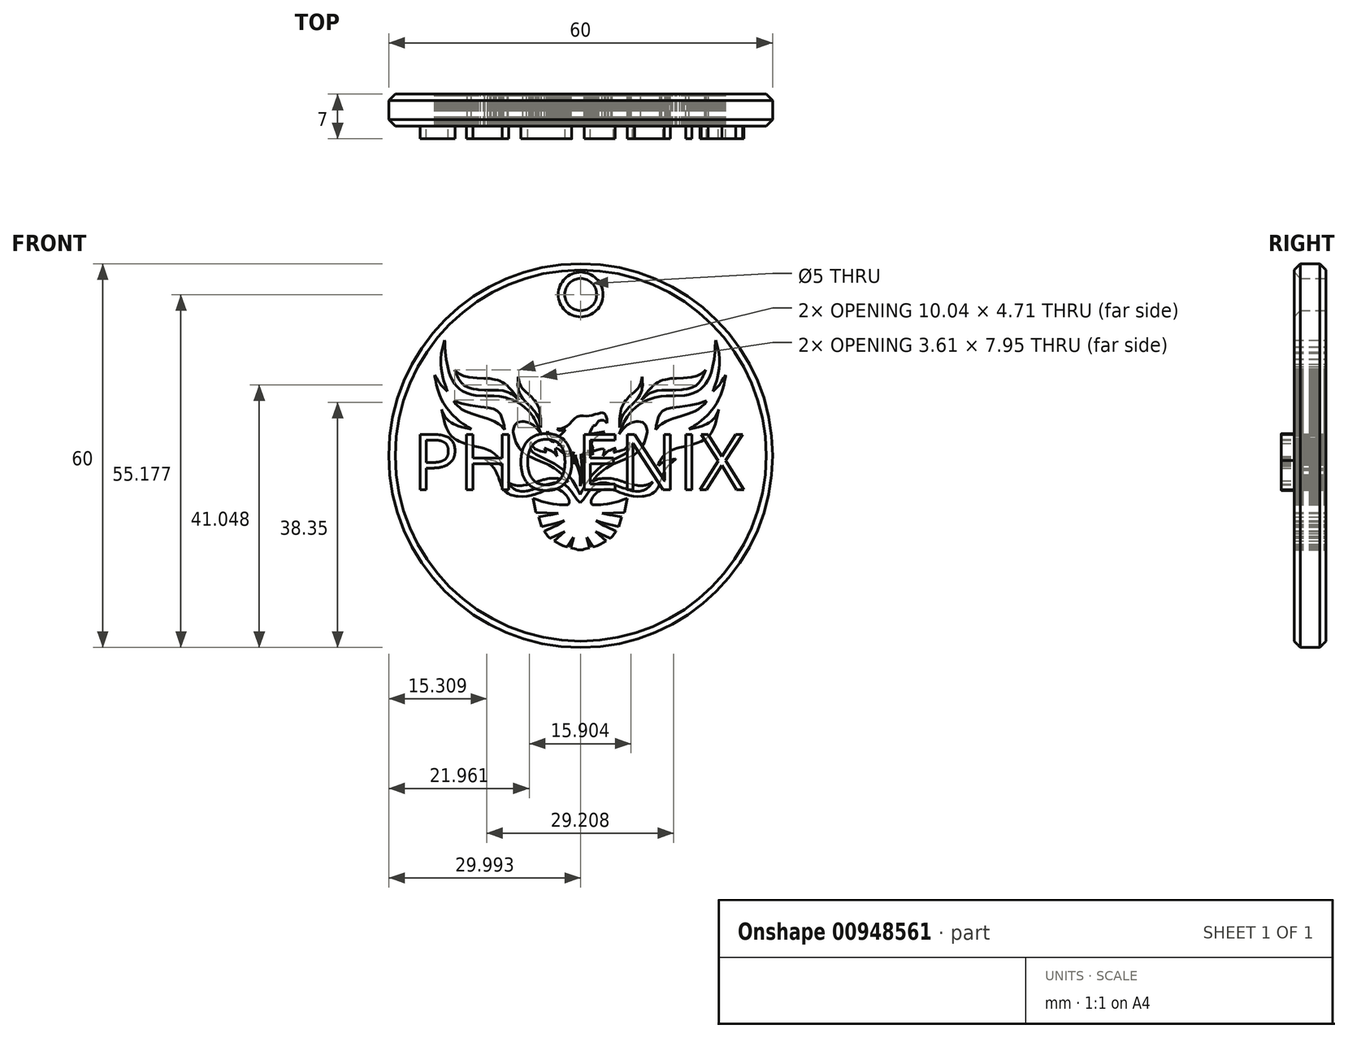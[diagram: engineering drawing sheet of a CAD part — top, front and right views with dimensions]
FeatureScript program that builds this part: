
annotation { "Feature Type Name" : "Feature", "Feature Type Description" : "" }
export const myFeature = defineFeature(function(context is Context, id is Id, definition is map)
    precondition{}
    {
        {
            var Q0;
            Q0=qCreatedBy(makeId("Front.planeOp"),FACE);
            var sketch = newSketch(context, id + "F0", { "sketchPlane" : qUnion([Q0])});
            skLineSegment(sketch, "E0", {"start": v(-23.96, 18.06) * mm, "end": v(23.17, -19.05) * mm});
            skLineSegment(sketch, "E1", {"start": v(-23.96, -19.05) * mm, "end": v(23.17, 18.06) * mm});
            skCircle(sketch, "E2", {"center": v(-0.4, -0.5) * mm, "radius": 30 * mm});
            skSolve(sketch);
        }
        {
            var Q0;
            Q0=makeQuery(id+"F0.imprint","IMPRINT",FACE,{"disambiguationData":[TD([[makeQuery(id+"F0.imprint","IMPRINT",EDGE,{"derivedFrom":sQuery(id+"F0.wireOp",EDGE,"E2")}),1.0]])]});
            extrude(context, id + "F1", {"entities" : qUnion([Q0]), "depth" : 5 * mm, "offsetDistance" : 25 * mm});
        }
        {
            var Q0;
            Q0=qCreatedBy(makeId("Front.planeOp"),FACE);
            var sketch = newSketch(context, id + "F2", { "sketchPlane" : qUnion([Q0])});
            skLineSegment(sketch, "E3", {"start": v(-6.6, 2.87) * mm, "end": v(-6.9, 3.33) * mm});
            skLineSegment(sketch, "E4", {"start": v(-6.9, 3.33) * mm, "end": v(-7.28, 3.78) * mm});
            skLineSegment(sketch, "E5", {"start": v(-7.28, 3.78) * mm, "end": v(-7.8, 4.25) * mm});
            skLineSegment(sketch, "E6", {"start": v(-7.8, 4.25) * mm, "end": v(-8.47, 4.62) * mm});
            skLineSegment(sketch, "E7", {"start": v(-8.47, 4.62) * mm, "end": v(-9.25, 4.84) * mm});
            skLineSegment(sketch, "E8", {"start": v(-9.25, 4.84) * mm, "end": v(-9.57, 4.84) * mm});
            skLineSegment(sketch, "E9", {"start": v(-9.57, 4.84) * mm, "end": v(-10.26, 4.7) * mm});
            skLineSegment(sketch, "E10", {"start": v(-10.26, 4.7) * mm, "end": v(-10.5, 4.48) * mm});
            skLineSegment(sketch, "E11", {"start": v(-10.5, 4.48) * mm, "end": v(-10.7, 4.24) * mm});
            skLineSegment(sketch, "E12", {"start": v(-10.7, 4.24) * mm, "end": v(-10.83, 3.89) * mm});
            skLineSegment(sketch, "E13", {"start": v(-10.83, 3.89) * mm, "end": v(-10.92, 3.46) * mm});
            skLineSegment(sketch, "E14", {"start": v(-10.92, 3.46) * mm, "end": v(-10.92, 3.18) * mm});
            skLineSegment(sketch, "E15", {"start": v(-10.92, 3.18) * mm, "end": v(-10.85, 2.63) * mm});
            skLineSegment(sketch, "E16", {"start": v(-10.85, 2.63) * mm, "end": v(-10.7, 2.18) * mm});
            skLineSegment(sketch, "E17", {"start": v(-10.7, 2.18) * mm, "end": v(-10.48, 1.53) * mm});
            skLineSegment(sketch, "E18", {"start": v(-10.48, 1.53) * mm, "end": v(-10.2, 1.03) * mm});
            skLineSegment(sketch, "E19", {"start": v(-10.2, 1.03) * mm, "end": v(-9.91, 0.57) * mm});
            skLineSegment(sketch, "E20", {"start": v(-9.91, 0.57) * mm, "end": v(-9.44, 0.05) * mm});
            skLineSegment(sketch, "E21", {"start": v(-9.44, 0.05) * mm, "end": v(-8.86, -0.41) * mm});
            skLineSegment(sketch, "E22", {"start": v(-8.86, -0.41) * mm, "end": v(-8.11, -0.78) * mm});
            skLineSegment(sketch, "E23", {"start": v(-8.11, -0.78) * mm, "end": v(-7.45, -1.05) * mm});
            skLineSegment(sketch, "E24", {"start": v(-7.45, -1.05) * mm, "end": v(-6.72, -1.37) * mm});
            skLineSegment(sketch, "E25", {"start": v(-6.72, -1.37) * mm, "end": v(-6.27, -1.55) * mm});
            skLineSegment(sketch, "E26", {"start": v(-6.27, -1.55) * mm, "end": v(-5.77, -1.8) * mm});
            skLineSegment(sketch, "E27", {"start": v(-5.77, -1.8) * mm, "end": v(-5.4, -1.98) * mm});
            skLineSegment(sketch, "E28", {"start": v(-5.4, -1.98) * mm, "end": v(-5, -2.2) * mm});
            skLineSegment(sketch, "E29", {"start": v(-5, -2.2) * mm, "end": v(-4.54, -2.46) * mm});
            skLineSegment(sketch, "E30", {"start": v(-4.54, -2.46) * mm, "end": v(-4.14, -2.74) * mm});
            skLineSegment(sketch, "E31", {"start": v(-4.14, -2.74) * mm, "end": v(-3.7, -3.09) * mm});
            skLineSegment(sketch, "E32", {"start": v(-3.7, -3.09) * mm, "end": v(-3.4, -3.34) * mm});
            skLineSegment(sketch, "E33", {"start": v(-3.4, -3.34) * mm, "end": v(-3.26, -3.48) * mm});
            skLineSegment(sketch, "E34", {"start": v(-3.26, -3.48) * mm, "end": v(-3.1, -3.64) * mm});
            skLineSegment(sketch, "E35", {"start": v(-3.1, -3.64) * mm, "end": v(-2.93, -3.84) * mm});
            skLineSegment(sketch, "E36", {"start": v(-2.93, -3.84) * mm, "end": v(-2.8, -4) * mm});
            skLineSegment(sketch, "E37", {"start": v(-2.8, -4) * mm, "end": v(-2.68, -4.14) * mm});
            skLineSegment(sketch, "E38", {"start": v(-2.68, -4.14) * mm, "end": v(-2.57, -4.28) * mm});
            skLineSegment(sketch, "E39", {"start": v(-2.57, -4.28) * mm, "end": v(-2.48, -4.4) * mm});
            skLineSegment(sketch, "E40", {"start": v(-2.48, -4.4) * mm, "end": v(-2.4, -4.52) * mm});
            skLineSegment(sketch, "E41", {"start": v(-2.4, -4.52) * mm, "end": v(-2.36, -4.59) * mm});
            skLineSegment(sketch, "E42", {"start": v(-2.36, -4.59) * mm, "end": v(-2.44, -4.54) * mm});
            skLineSegment(sketch, "E43", {"start": v(-2.44, -4.54) * mm, "end": v(-2.53, -4.48) * mm});
            skLineSegment(sketch, "E44", {"start": v(-2.53, -4.48) * mm, "end": v(-2.63, -4.44) * mm});
            skLineSegment(sketch, "E45", {"start": v(-2.63, -4.44) * mm, "end": v(-2.7, -4.4) * mm});
            skLineSegment(sketch, "E46", {"start": v(-2.7, -4.4) * mm, "end": v(-2.78, -4.37) * mm});
            skLineSegment(sketch, "E47", {"start": v(-2.78, -4.37) * mm, "end": v(-2.87, -4.33) * mm});
            skLineSegment(sketch, "E48", {"start": v(-2.87, -4.33) * mm, "end": v(-2.98, -4.28) * mm});
            skLineSegment(sketch, "E49", {"start": v(-2.98, -4.28) * mm, "end": v(-3.08, -4.25) * mm});
            skLineSegment(sketch, "E50", {"start": v(-3.08, -4.25) * mm, "end": v(-3.22, -4.2) * mm});
            skLineSegment(sketch, "E51", {"start": v(-3.22, -4.2) * mm, "end": v(-3.4, -4.15) * mm});
            skLineSegment(sketch, "E52", {"start": v(-3.4, -4.15) * mm, "end": v(-3.5, -4.13) * mm});
            skLineSegment(sketch, "E53", {"start": v(-3.5, -4.13) * mm, "end": v(-3.74, -4.1) * mm});
            skLineSegment(sketch, "E54", {"start": v(-3.74, -4.1) * mm, "end": v(-3.97, -4.06) * mm});
            skLineSegment(sketch, "E55", {"start": v(-3.97, -4.06) * mm, "end": v(-4.12, -4.04) * mm});
            skLineSegment(sketch, "E56", {"start": v(-4.12, -4.04) * mm, "end": v(-4.25, -4.03) * mm});
            skLineSegment(sketch, "E57", {"start": v(-4.25, -4.03) * mm, "end": v(-4.4, -4.03) * mm});
            skLineSegment(sketch, "E58", {"start": v(-4.4, -4.03) * mm, "end": v(-4.63, -4.04) * mm});
            skLineSegment(sketch, "E59", {"start": v(-4.63, -4.04) * mm, "end": v(-4.9, -4.06) * mm});
            skLineSegment(sketch, "E60", {"start": v(-4.9, -4.06) * mm, "end": v(-5.29, -4.08) * mm});
            skLineSegment(sketch, "E61", {"start": v(-5.29, -4.08) * mm, "end": v(-5.62, -4.13) * mm});
            skLineSegment(sketch, "E62", {"start": v(-5.62, -4.13) * mm, "end": v(-5.82, -4.18) * mm});
            skLineSegment(sketch, "E63", {"start": v(-5.82, -4.18) * mm, "end": v(-6.06, -4.23) * mm});
            skLineSegment(sketch, "E64", {"start": v(-6.06, -4.23) * mm, "end": v(-6.28, -4.28) * mm});
            skLineSegment(sketch, "E65", {"start": v(-6.28, -4.28) * mm, "end": v(-6.55, -4.37) * mm});
            skLineSegment(sketch, "E66", {"start": v(-6.55, -4.37) * mm, "end": v(-6.77, -4.42) * mm});
            skLineSegment(sketch, "E67", {"start": v(-6.77, -4.42) * mm, "end": v(-6.9, -4.47) * mm});
            skLineSegment(sketch, "E68", {"start": v(-6.9, -4.47) * mm, "end": v(-7.04, -4.5) * mm});
            skLineSegment(sketch, "E69", {"start": v(-7.04, -4.5) * mm, "end": v(-7.17, -4.55) * mm});
            skLineSegment(sketch, "E70", {"start": v(-7.17, -4.55) * mm, "end": v(-7.31, -4.6) * mm});
            skLineSegment(sketch, "E71", {"start": v(-7.31, -4.6) * mm, "end": v(-7.46, -4.66) * mm});
            skLineSegment(sketch, "E72", {"start": v(-7.46, -4.66) * mm, "end": v(-7.65, -4.71) * mm});
            skLineSegment(sketch, "E73", {"start": v(-7.65, -4.71) * mm, "end": v(-7.77, -4.75) * mm});
            skLineSegment(sketch, "E74", {"start": v(-7.77, -4.75) * mm, "end": v(-7.9, -4.79) * mm});
            skLineSegment(sketch, "E75", {"start": v(-7.9, -4.79) * mm, "end": v(-8.04, -4.84) * mm});
            skLineSegment(sketch, "E76", {"start": v(-8.04, -4.84) * mm, "end": v(-8.21, -4.89) * mm});
            skLineSegment(sketch, "E77", {"start": v(-8.21, -4.89) * mm, "end": v(-8.48, -4.97) * mm});
            skLineSegment(sketch, "E78", {"start": v(-8.48, -4.97) * mm, "end": v(-8.79, -5.05) * mm});
            skLineSegment(sketch, "E79", {"start": v(-8.79, -5.05) * mm, "end": v(-9.02, -5.1) * mm});
            skLineSegment(sketch, "E80", {"start": v(-9.02, -5.1) * mm, "end": v(-9.36, -5.15) * mm});
            skLineSegment(sketch, "E81", {"start": v(-9.36, -5.15) * mm, "end": v(-9.6, -5.18) * mm});
            skLineSegment(sketch, "E82", {"start": v(-9.6, -5.18) * mm, "end": v(-9.94, -5.2) * mm});
            skLineSegment(sketch, "E83", {"start": v(-9.94, -5.2) * mm, "end": v(-10.1, -5.2) * mm});
            skLineSegment(sketch, "E84", {"start": v(-10.1, -5.2) * mm, "end": v(-10.34, -5.19) * mm});
            skLineSegment(sketch, "E85", {"start": v(-10.34, -5.19) * mm, "end": v(-10.54, -5.17) * mm});
            skLineSegment(sketch, "E86", {"start": v(-10.54, -5.17) * mm, "end": v(-10.7, -5.13) * mm});
            skLineSegment(sketch, "E87", {"start": v(-10.7, -5.13) * mm, "end": v(-10.82, -5.1) * mm});
            skLineSegment(sketch, "E88", {"start": v(-10.82, -5.1) * mm, "end": v(-10.92, -5.07) * mm});
            skLineSegment(sketch, "E89", {"start": v(-10.92, -5.07) * mm, "end": v(-11.01, -5.03) * mm});
            skLineSegment(sketch, "E90", {"start": v(-11.01, -5.03) * mm, "end": v(-11.1, -5) * mm});
            skLineSegment(sketch, "E91", {"start": v(-11.1, -5) * mm, "end": v(-11.19, -4.97) * mm});
            skLineSegment(sketch, "E92", {"start": v(-11.19, -4.97) * mm, "end": v(-11.28, -4.93) * mm});
            skLineSegment(sketch, "E93", {"start": v(-11.28, -4.93) * mm, "end": v(-11.33, -4.9) * mm});
            skLineSegment(sketch, "E94", {"start": v(-11.33, -4.9) * mm, "end": v(-11.39, -4.87) * mm});
            skLineSegment(sketch, "E95", {"start": v(-11.39, -4.87) * mm, "end": v(-11.45, -4.84) * mm});
            skLineSegment(sketch, "E96", {"start": v(-11.45, -4.84) * mm, "end": v(-11.52, -4.8) * mm});
            skLineSegment(sketch, "E97", {"start": v(-11.52, -4.8) * mm, "end": v(-11.57, -4.77) * mm});
            skLineSegment(sketch, "E98", {"start": v(-11.57, -4.77) * mm, "end": v(-11.68, -4.7) * mm});
            skLineSegment(sketch, "E99", {"start": v(-11.68, -4.7) * mm, "end": v(-11.82, -4.63) * mm});
            skLineSegment(sketch, "E100", {"start": v(-11.82, -4.63) * mm, "end": v(-11.8, -4.69) * mm});
            skLineSegment(sketch, "E101", {"start": v(-11.8, -4.69) * mm, "end": v(-11.75, -4.75) * mm});
            skLineSegment(sketch, "E102", {"start": v(-11.75, -4.75) * mm, "end": v(-11.72, -4.8) * mm});
            skLineSegment(sketch, "E103", {"start": v(-11.72, -4.8) * mm, "end": v(-11.67, -4.86) * mm});
            skLineSegment(sketch, "E104", {"start": v(-11.67, -4.86) * mm, "end": v(-11.64, -4.9) * mm});
            skLineSegment(sketch, "E105", {"start": v(-11.64, -4.9) * mm, "end": v(-11.6, -4.94) * mm});
            skLineSegment(sketch, "E106", {"start": v(-11.6, -4.94) * mm, "end": v(-11.57, -4.98) * mm});
            skLineSegment(sketch, "E107", {"start": v(-11.57, -4.98) * mm, "end": v(-11.54, -5.02) * mm});
            skLineSegment(sketch, "E108", {"start": v(-11.54, -5.02) * mm, "end": v(-11.5, -5.06) * mm});
            skLineSegment(sketch, "E109", {"start": v(-11.5, -5.06) * mm, "end": v(-11.48, -5.1) * mm});
            skLineSegment(sketch, "E110", {"start": v(-11.48, -5.1) * mm, "end": v(-11.44, -5.15) * mm});
            skLineSegment(sketch, "E111", {"start": v(-11.44, -5.15) * mm, "end": v(-11.41, -5.18) * mm});
            skLineSegment(sketch, "E112", {"start": v(-11.41, -5.18) * mm, "end": v(-11.38, -5.2) * mm});
            skLineSegment(sketch, "E113", {"start": v(-11.38, -5.2) * mm, "end": v(-11.35, -5.24) * mm});
            skLineSegment(sketch, "E114", {"start": v(-11.35, -5.24) * mm, "end": v(-11.32, -5.27) * mm});
            skLineSegment(sketch, "E115", {"start": v(-11.32, -5.27) * mm, "end": v(-11.28, -5.3) * mm});
            skLineSegment(sketch, "E116", {"start": v(-11.28, -5.3) * mm, "end": v(-11.25, -5.34) * mm});
            skLineSegment(sketch, "E117", {"start": v(-11.25, -5.34) * mm, "end": v(-11.2, -5.37) * mm});
            skLineSegment(sketch, "E118", {"start": v(-11.2, -5.37) * mm, "end": v(-11.18, -5.4) * mm});
            skLineSegment(sketch, "E119", {"start": v(-11.18, -5.4) * mm, "end": v(-11.15, -5.43) * mm});
            skLineSegment(sketch, "E120", {"start": v(-11.15, -5.43) * mm, "end": v(-11.1, -5.46) * mm});
            skLineSegment(sketch, "E121", {"start": v(-11.1, -5.46) * mm, "end": v(-11.07, -5.5) * mm});
            skLineSegment(sketch, "E122", {"start": v(-11.07, -5.5) * mm, "end": v(-11.03, -5.53) * mm});
            skLineSegment(sketch, "E123", {"start": v(-11.03, -5.53) * mm, "end": v(-11, -5.56) * mm});
            skLineSegment(sketch, "E124", {"start": v(-11, -5.56) * mm, "end": v(-10.92, -5.6) * mm});
            skLineSegment(sketch, "E125", {"start": v(-10.92, -5.6) * mm, "end": v(-10.83, -5.68) * mm});
            skLineSegment(sketch, "E126", {"start": v(-10.83, -5.68) * mm, "end": v(-10.72, -5.75) * mm});
            skLineSegment(sketch, "E127", {"start": v(-10.72, -5.75) * mm, "end": v(-10.6, -5.82) * mm});
            skLineSegment(sketch, "E128", {"start": v(-10.6, -5.82) * mm, "end": v(-10.48, -5.89) * mm});
            skLineSegment(sketch, "E129", {"start": v(-10.48, -5.89) * mm, "end": v(-10.33, -5.94) * mm});
            skLineSegment(sketch, "E130", {"start": v(-10.33, -5.94) * mm, "end": v(-10.2, -5.99) * mm});
            skLineSegment(sketch, "E131", {"start": v(-10.2, -5.99) * mm, "end": v(-10, -6.03) * mm});
            skLineSegment(sketch, "E132", {"start": v(-10, -6.03) * mm, "end": v(-9.77, -6.07) * mm});
            skLineSegment(sketch, "E133", {"start": v(-9.77, -6.07) * mm, "end": v(-9.64, -6.08) * mm});
            skLineSegment(sketch, "E134", {"start": v(-9.64, -6.08) * mm, "end": v(-9.18, -6.07) * mm});
            skLineSegment(sketch, "E135", {"start": v(-9.18, -6.07) * mm, "end": v(-8.83, -6.04) * mm});
            skLineSegment(sketch, "E136", {"start": v(-8.83, -6.04) * mm, "end": v(-8.66, -6) * mm});
            skLineSegment(sketch, "E137", {"start": v(-8.66, -6) * mm, "end": v(-8.52, -5.97) * mm});
            skLineSegment(sketch, "E138", {"start": v(-8.52, -5.97) * mm, "end": v(-8.4, -5.94) * mm});
            skLineSegment(sketch, "E139", {"start": v(-8.4, -5.94) * mm, "end": v(-8.27, -5.91) * mm});
            skLineSegment(sketch, "E140", {"start": v(-8.27, -5.91) * mm, "end": v(-8.17, -5.88) * mm});
            skLineSegment(sketch, "E141", {"start": v(-8.17, -5.88) * mm, "end": v(-8.06, -5.84) * mm});
            skLineSegment(sketch, "E142", {"start": v(-8.06, -5.84) * mm, "end": v(-7.96, -5.8) * mm});
            skLineSegment(sketch, "E143", {"start": v(-7.96, -5.8) * mm, "end": v(-7.85, -5.78) * mm});
            skLineSegment(sketch, "E144", {"start": v(-7.85, -5.78) * mm, "end": v(-7.75, -5.75) * mm});
            skLineSegment(sketch, "E145", {"start": v(-7.75, -5.75) * mm, "end": v(-7.66, -5.72) * mm});
            skLineSegment(sketch, "E146", {"start": v(-7.66, -5.72) * mm, "end": v(-7.57, -5.68) * mm});
            skLineSegment(sketch, "E147", {"start": v(-7.57, -5.68) * mm, "end": v(-7.5, -5.66) * mm});
            skLineSegment(sketch, "E148", {"start": v(-7.5, -5.66) * mm, "end": v(-7.21, -5.56) * mm});
            skLineSegment(sketch, "E149", {"start": v(-7.21, -5.56) * mm, "end": v(-7, -5.49) * mm});
            skLineSegment(sketch, "E150", {"start": v(-7, -5.49) * mm, "end": v(-6.87, -5.43) * mm});
            skLineSegment(sketch, "E151", {"start": v(-6.87, -5.43) * mm, "end": v(-6.7, -5.37) * mm});
            skLineSegment(sketch, "E152", {"start": v(-6.7, -5.37) * mm, "end": v(-6.48, -5.3) * mm});
            skLineSegment(sketch, "E153", {"start": v(-6.48, -5.3) * mm, "end": v(-6.36, -5.25) * mm});
            skLineSegment(sketch, "E154", {"start": v(-6.36, -5.25) * mm, "end": v(-6.19, -5.18) * mm});
            skLineSegment(sketch, "E155", {"start": v(-6.19, -5.18) * mm, "end": v(-6.05, -5.13) * mm});
            skLineSegment(sketch, "E156", {"start": v(-6.05, -5.13) * mm, "end": v(-5.67, -5.02) * mm});
            skLineSegment(sketch, "E157", {"start": v(-5.67, -5.02) * mm, "end": v(-5.39, -4.93) * mm});
            skLineSegment(sketch, "E158", {"start": v(-5.39, -4.93) * mm, "end": v(-5.08, -4.85) * mm});
            skLineSegment(sketch, "E159", {"start": v(-5.08, -4.85) * mm, "end": v(-4.86, -4.8) * mm});
            skLineSegment(sketch, "E160", {"start": v(-4.86, -4.8) * mm, "end": v(-4.57, -4.76) * mm});
            skLineSegment(sketch, "E161", {"start": v(-4.57, -4.76) * mm, "end": v(-4.37, -4.73) * mm});
            skLineSegment(sketch, "E162", {"start": v(-4.37, -4.73) * mm, "end": v(-3.85, -4.74) * mm});
            skLineSegment(sketch, "E163", {"start": v(-3.85, -4.74) * mm, "end": v(-3.63, -4.77) * mm});
            skLineSegment(sketch, "E164", {"start": v(-3.63, -4.77) * mm, "end": v(-3.5, -4.8) * mm});
            skLineSegment(sketch, "E165", {"start": v(-3.5, -4.8) * mm, "end": v(-3.38, -4.84) * mm});
            skLineSegment(sketch, "E166", {"start": v(-3.38, -4.84) * mm, "end": v(-3.21, -4.9) * mm});
            skLineSegment(sketch, "E167", {"start": v(-3.21, -4.9) * mm, "end": v(-3.06, -4.97) * mm});
            skLineSegment(sketch, "E168", {"start": v(-3.06, -4.97) * mm, "end": v(-2.9, -5.06) * mm});
            skLineSegment(sketch, "E169", {"start": v(-2.9, -5.06) * mm, "end": v(-2.83, -5.1) * mm});
            skLineSegment(sketch, "E170", {"start": v(-2.83, -5.1) * mm, "end": v(-2.79, -5.13) * mm});
            skLineSegment(sketch, "E171", {"start": v(-2.79, -5.13) * mm, "end": v(-2.75, -5.16) * mm});
            skLineSegment(sketch, "E172", {"start": v(-2.75, -5.16) * mm, "end": v(-2.71, -5.2) * mm});
            skLineSegment(sketch, "E173", {"start": v(-2.71, -5.2) * mm, "end": v(-2.68, -5.22) * mm});
            skLineSegment(sketch, "E174", {"start": v(-2.68, -5.22) * mm, "end": v(-2.62, -5.26) * mm});
            skLineSegment(sketch, "E175", {"start": v(-2.62, -5.26) * mm, "end": v(-2.4, -5.48) * mm});
            skLineSegment(sketch, "E176", {"start": v(-2.4, -5.48) * mm, "end": v(-2.33, -5.55) * mm});
            skLineSegment(sketch, "E177", {"start": v(-2.33, -5.55) * mm, "end": v(-2.17, -5.73) * mm});
            skLineSegment(sketch, "E178", {"start": v(-2.17, -5.73) * mm, "end": v(-2.11, -5.79) * mm});
            skLineSegment(sketch, "E179", {"start": v(-2.11, -5.79) * mm, "end": v(-1.83, -6.14) * mm});
            skLineSegment(sketch, "E180", {"start": v(-1.83, -6.14) * mm, "end": v(-1.67, -6.36) * mm});
            skLineSegment(sketch, "E181", {"start": v(-1.67, -6.36) * mm, "end": v(-1.57, -6.5) * mm});
            skLineSegment(sketch, "E182", {"start": v(-1.57, -6.5) * mm, "end": v(-1.45, -6.7) * mm});
            skLineSegment(sketch, "E183", {"start": v(-1.45, -6.7) * mm, "end": v(-1.22, -6.99) * mm});
            skLineSegment(sketch, "E184", {"start": v(-1.22, -6.99) * mm, "end": v(-0.98, -7.33) * mm});
            skLineSegment(sketch, "E185", {"start": v(-0.98, -7.33) * mm, "end": v(-0.72, -7.63) * mm});
            skLineSegment(sketch, "E186", {"start": v(-0.72, -7.63) * mm, "end": v(-0.48, -7.87) * mm});
            skLineSegment(sketch, "E187", {"start": v(-0.48, -7.87) * mm, "end": v(-0.48, -15.24) * mm, "construction": true});
            skLineSegment(sketch, "E188", {"start": v(-0.48, -15.24) * mm, "end": v(-0.68, -15.24) * mm});
            skLineSegment(sketch, "E189", {"start": v(-0.68, -15.24) * mm, "end": v(-0.89, -15.2) * mm});
            skLineSegment(sketch, "E190", {"start": v(-0.89, -15.2) * mm, "end": v(-1.13, -15.12) * mm});
            skLineSegment(sketch, "E191", {"start": v(-1.13, -15.12) * mm, "end": v(-1.92, -14.9) * mm});
            skLineSegment(sketch, "E192", {"start": v(-1.92, -14.9) * mm, "end": v(-1.5, -13.24) * mm});
            skLineSegment(sketch, "E193", {"start": v(-1.5, -13.24) * mm, "end": v(-2.45, -14.74) * mm});
            skLineSegment(sketch, "E194", {"start": v(-2.45, -14.74) * mm, "end": v(-2.67, -14.74) * mm});
            skLineSegment(sketch, "E195", {"start": v(-2.67, -14.74) * mm, "end": v(-3.17, -14.6) * mm});
            skLineSegment(sketch, "E196", {"start": v(-3.17, -14.6) * mm, "end": v(-3.63, -14.37) * mm});
            skLineSegment(sketch, "E197", {"start": v(-3.63, -14.37) * mm, "end": v(-4.52, -13.83) * mm});
            skLineSegment(sketch, "E198", {"start": v(-4.52, -13.83) * mm, "end": v(-2.91, -12.4) * mm});
            skLineSegment(sketch, "E199", {"start": v(-2.91, -12.4) * mm, "end": v(-5.13, -13.36) * mm});
            skLineSegment(sketch, "E200", {"start": v(-5.13, -13.36) * mm, "end": v(-5.18, -13.38) * mm});
            skLineSegment(sketch, "E201", {"start": v(-5.18, -13.38) * mm, "end": v(-5.25, -13.36) * mm});
            skLineSegment(sketch, "E202", {"start": v(-5.25, -13.36) * mm, "end": v(-5.4, -13.23) * mm});
            skLineSegment(sketch, "E203", {"start": v(-5.4, -13.23) * mm, "end": v(-5.55, -13.07) * mm});
            skLineSegment(sketch, "E204", {"start": v(-5.55, -13.07) * mm, "end": v(-5.8, -12.72) * mm});
            skLineSegment(sketch, "E205", {"start": v(-5.8, -12.72) * mm, "end": v(-6.06, -12.34) * mm});
            skLineSegment(sketch, "E206", {"start": v(-6.06, -12.34) * mm, "end": v(-6.05, -12.31) * mm});
            skLineSegment(sketch, "E207", {"start": v(-6.05, -12.31) * mm, "end": v(-5.96, -12.28) * mm});
            skLineSegment(sketch, "E208", {"start": v(-5.96, -12.28) * mm, "end": v(-4.72, -11.7) * mm});
            skLineSegment(sketch, "E209", {"start": v(-4.72, -11.7) * mm, "end": v(-4.15, -11.41) * mm});
            skLineSegment(sketch, "E210", {"start": v(-4.15, -11.41) * mm, "end": v(-3.27, -10.87) * mm});
            skLineSegment(sketch, "E211", {"start": v(-3.27, -10.87) * mm, "end": v(-2.93, -10.63) * mm});
            skLineSegment(sketch, "E212", {"start": v(-2.93, -10.63) * mm, "end": v(-3.55, -10.87) * mm});
            skLineSegment(sketch, "E213", {"start": v(-3.55, -10.87) * mm, "end": v(-4.18, -11.05) * mm});
            skLineSegment(sketch, "E214", {"start": v(-4.18, -11.05) * mm, "end": v(-4.93, -11.25) * mm});
            skLineSegment(sketch, "E215", {"start": v(-4.93, -11.25) * mm, "end": v(-5.72, -11.44) * mm});
            skLineSegment(sketch, "E216", {"start": v(-5.72, -11.44) * mm, "end": v(-6.53, -11.64) * mm});
            skLineSegment(sketch, "E217", {"start": v(-6.53, -11.64) * mm, "end": v(-6.96, -10.1) * mm});
            skLineSegment(sketch, "E218", {"start": v(-6.96, -10.1) * mm, "end": v(-6.38, -9.99) * mm});
            skLineSegment(sketch, "E219", {"start": v(-6.38, -9.99) * mm, "end": v(-5.6, -9.85) * mm});
            skLineSegment(sketch, "E220", {"start": v(-5.6, -9.85) * mm, "end": v(-5.1, -9.76) * mm});
            skLineSegment(sketch, "E221", {"start": v(-5.1, -9.76) * mm, "end": v(-3.91, -9.55) * mm});
            skLineSegment(sketch, "E222", {"start": v(-3.91, -9.55) * mm, "end": v(-7.38, -9.41) * mm});
            skLineSegment(sketch, "E223", {"start": v(-7.38, -9.41) * mm, "end": v(-7.83, -7.14) * mm});
            skLineSegment(sketch, "E224", {"start": v(-7.83, -7.14) * mm, "end": v(-7.28, -7.37) * mm});
            skLineSegment(sketch, "E225", {"start": v(-7.28, -7.37) * mm, "end": v(-6.45, -7.67) * mm});
            skLineSegment(sketch, "E226", {"start": v(-6.45, -7.67) * mm, "end": v(-5.36, -7.91) * mm});
            skLineSegment(sketch, "E227", {"start": v(-5.36, -7.91) * mm, "end": v(-4.75, -8.04) * mm});
            skLineSegment(sketch, "E228", {"start": v(-4.75, -8.04) * mm, "end": v(-4.11, -8.14) * mm});
            skLineSegment(sketch, "E229", {"start": v(-4.11, -8.14) * mm, "end": v(-3.69, -8.19) * mm});
            skLineSegment(sketch, "E230", {"start": v(-3.69, -8.19) * mm, "end": v(-3.1, -8.21) * mm});
            skLineSegment(sketch, "E231", {"start": v(-3.1, -8.21) * mm, "end": v(-2.51, -8.2) * mm});
            skLineSegment(sketch, "E232", {"start": v(-2.51, -8.2) * mm, "end": v(-2.4, -8.2) * mm});
            skLineSegment(sketch, "E233", {"start": v(-2.4, -8.2) * mm, "end": v(-2.3, -8.12) * mm});
            skLineSegment(sketch, "E234", {"start": v(-2.3, -8.12) * mm, "end": v(-2.23, -7.98) * mm});
            skLineSegment(sketch, "E235", {"start": v(-2.23, -7.98) * mm, "end": v(-2.2, -7.9) * mm});
            skLineSegment(sketch, "E236", {"start": v(-2.2, -7.9) * mm, "end": v(-2.2, -7.5) * mm});
            skLineSegment(sketch, "E237", {"start": v(-2.2, -7.5) * mm, "end": v(-2.3, -7.2) * mm});
            skLineSegment(sketch, "E238", {"start": v(-2.3, -7.2) * mm, "end": v(-2.43, -6.99) * mm});
            skLineSegment(sketch, "E239", {"start": v(-2.43, -6.99) * mm, "end": v(-2.62, -6.73) * mm});
            skLineSegment(sketch, "E240", {"start": v(-2.62, -6.73) * mm, "end": v(-2.8, -6.52) * mm});
            skLineSegment(sketch, "E241", {"start": v(-2.8, -6.52) * mm, "end": v(-3, -6.33) * mm});
            skLineSegment(sketch, "E242", {"start": v(-3, -6.33) * mm, "end": v(-3.12, -6.23) * mm});
            skLineSegment(sketch, "E243", {"start": v(-3.12, -6.23) * mm, "end": v(-3.23, -6.16) * mm});
            skLineSegment(sketch, "E244", {"start": v(-3.23, -6.16) * mm, "end": v(-3.36, -6.07) * mm});
            skLineSegment(sketch, "E245", {"start": v(-3.36, -6.07) * mm, "end": v(-3.63, -5.9) * mm});
            skLineSegment(sketch, "E246", {"start": v(-3.63, -5.9) * mm, "end": v(-3.89, -5.78) * mm});
            skLineSegment(sketch, "E247", {"start": v(-3.89, -5.78) * mm, "end": v(-4.27, -5.66) * mm});
            skLineSegment(sketch, "E248", {"start": v(-4.27, -5.66) * mm, "end": v(-4.45, -5.63) * mm});
            skLineSegment(sketch, "E249", {"start": v(-4.45, -5.63) * mm, "end": v(-4.93, -5.61) * mm});
            skLineSegment(sketch, "E250", {"start": v(-4.93, -5.61) * mm, "end": v(-5.1, -5.66) * mm});
            skLineSegment(sketch, "E251", {"start": v(-5.1, -5.66) * mm, "end": v(-5.3, -5.73) * mm});
            skLineSegment(sketch, "E252", {"start": v(-5.3, -5.73) * mm, "end": v(-5.49, -5.8) * mm});
            skLineSegment(sketch, "E253", {"start": v(-5.49, -5.8) * mm, "end": v(-5.75, -5.89) * mm});
            skLineSegment(sketch, "E254", {"start": v(-5.75, -5.89) * mm, "end": v(-6.02, -5.99) * mm});
            skLineSegment(sketch, "E255", {"start": v(-6.02, -5.99) * mm, "end": v(-6.32, -6.1) * mm});
            skLineSegment(sketch, "E256", {"start": v(-6.32, -6.1) * mm, "end": v(-6.7, -6.25) * mm});
            skLineSegment(sketch, "E257", {"start": v(-6.7, -6.25) * mm, "end": v(-7.15, -6.4) * mm});
            skLineSegment(sketch, "E258", {"start": v(-7.15, -6.4) * mm, "end": v(-7.64, -6.57) * mm});
            skLineSegment(sketch, "E259", {"start": v(-7.64, -6.57) * mm, "end": v(-7.75, -6.6) * mm});
            skLineSegment(sketch, "E260", {"start": v(-7.75, -6.6) * mm, "end": v(-8.16, -6.72) * mm});
            skLineSegment(sketch, "E261", {"start": v(-8.16, -6.72) * mm, "end": v(-8.81, -6.85) * mm});
            skLineSegment(sketch, "E262", {"start": v(-8.81, -6.85) * mm, "end": v(-9.47, -6.9) * mm});
            skLineSegment(sketch, "E263", {"start": v(-9.47, -6.9) * mm, "end": v(-10.2, -6.87) * mm});
            skLineSegment(sketch, "E264", {"start": v(-10.2, -6.87) * mm, "end": v(-10.45, -6.83) * mm});
            skLineSegment(sketch, "E265", {"start": v(-10.45, -6.83) * mm, "end": v(-10.95, -6.74) * mm});
            skLineSegment(sketch, "E266", {"start": v(-10.95, -6.74) * mm, "end": v(-11.26, -6.65) * mm});
            skLineSegment(sketch, "E267", {"start": v(-11.26, -6.65) * mm, "end": v(-11.44, -6.58) * mm});
            skLineSegment(sketch, "E268", {"start": v(-11.44, -6.58) * mm, "end": v(-11.64, -6.49) * mm});
            skLineSegment(sketch, "E269", {"start": v(-11.64, -6.49) * mm, "end": v(-11.96, -6.3) * mm});
            skLineSegment(sketch, "E270", {"start": v(-11.96, -6.3) * mm, "end": v(-12.12, -6.17) * mm});
            skLineSegment(sketch, "E271", {"start": v(-12.12, -6.17) * mm, "end": v(-12.21, -6.08) * mm});
            skLineSegment(sketch, "E272", {"start": v(-12.21, -6.08) * mm, "end": v(-12.27, -6.01) * mm});
            skLineSegment(sketch, "E273", {"start": v(-12.27, -6.01) * mm, "end": v(-12.37, -5.9) * mm});
            skLineSegment(sketch, "E274", {"start": v(-12.37, -5.9) * mm, "end": v(-12.44, -5.82) * mm});
            skLineSegment(sketch, "E275", {"start": v(-12.44, -5.82) * mm, "end": v(-12.5, -5.72) * mm});
            skLineSegment(sketch, "E276", {"start": v(-12.5, -5.72) * mm, "end": v(-12.59, -5.57) * mm});
            skLineSegment(sketch, "E277", {"start": v(-12.59, -5.57) * mm, "end": v(-12.65, -5.44) * mm});
            skLineSegment(sketch, "E278", {"start": v(-12.65, -5.44) * mm, "end": v(-12.71, -5.32) * mm});
            skLineSegment(sketch, "E279", {"start": v(-12.71, -5.32) * mm, "end": v(-12.78, -5.18) * mm});
            skLineSegment(sketch, "E280", {"start": v(-12.78, -5.18) * mm, "end": v(-12.83, -5.04) * mm});
            skLineSegment(sketch, "E281", {"start": v(-12.83, -5.04) * mm, "end": v(-12.87, -4.92) * mm});
            skLineSegment(sketch, "E282", {"start": v(-12.87, -4.92) * mm, "end": v(-12.93, -4.76) * mm});
            skLineSegment(sketch, "E283", {"start": v(-12.93, -4.76) * mm, "end": v(-13.04, -4.5) * mm});
            skLineSegment(sketch, "E284", {"start": v(-13.04, -4.5) * mm, "end": v(-13.1, -4.3) * mm});
            skLineSegment(sketch, "E285", {"start": v(-13.1, -4.3) * mm, "end": v(-13.17, -4.13) * mm});
            skLineSegment(sketch, "E286", {"start": v(-13.17, -4.13) * mm, "end": v(-13.26, -3.9) * mm});
            skLineSegment(sketch, "E287", {"start": v(-13.26, -3.9) * mm, "end": v(-13.3, -3.82) * mm});
            skLineSegment(sketch, "E288", {"start": v(-13.3, -3.82) * mm, "end": v(-13.32, -3.74) * mm});
            skLineSegment(sketch, "E289", {"start": v(-13.32, -3.74) * mm, "end": v(-13.35, -3.67) * mm});
            skLineSegment(sketch, "E290", {"start": v(-13.35, -3.67) * mm, "end": v(-13.38, -3.58) * mm});
            skLineSegment(sketch, "E291", {"start": v(-13.38, -3.58) * mm, "end": v(-13.47, -3.36) * mm});
            skLineSegment(sketch, "E292", {"start": v(-13.47, -3.36) * mm, "end": v(-13.57, -3.16) * mm});
            skLineSegment(sketch, "E293", {"start": v(-13.57, -3.16) * mm, "end": v(-13.64, -3.03) * mm});
            skLineSegment(sketch, "E294", {"start": v(-13.64, -3.03) * mm, "end": v(-13.77, -2.79) * mm});
            skLineSegment(sketch, "E295", {"start": v(-13.77, -2.79) * mm, "end": v(-13.83, -2.68) * mm});
            skLineSegment(sketch, "E296", {"start": v(-13.83, -2.68) * mm, "end": v(-13.95, -2.49) * mm});
            skLineSegment(sketch, "E297", {"start": v(-13.95, -2.49) * mm, "end": v(-14.38, -1.96) * mm});
            skLineSegment(sketch, "E298", {"start": v(-14.38, -1.96) * mm, "end": v(-15.4, -1.04) * mm});
            skLineSegment(sketch, "E299", {"start": v(-15.4, -1.04) * mm, "end": v(-15.39, -1.03) * mm});
            skLineSegment(sketch, "E300", {"start": v(-15.39, -1.03) * mm, "end": v(-14.96, -1.06) * mm});
            skLineSegment(sketch, "E301", {"start": v(-14.96, -1.06) * mm, "end": v(-14.57, -1.13) * mm});
            skLineSegment(sketch, "E302", {"start": v(-14.57, -1.13) * mm, "end": v(-14.36, -1.18) * mm});
            skLineSegment(sketch, "E303", {"start": v(-14.36, -1.18) * mm, "end": v(-14, -1.27) * mm});
            skLineSegment(sketch, "E304", {"start": v(-14, -1.27) * mm, "end": v(-13.78, -1.36) * mm});
            skLineSegment(sketch, "E305", {"start": v(-13.78, -1.36) * mm, "end": v(-13.53, -1.48) * mm});
            skLineSegment(sketch, "E306", {"start": v(-13.53, -1.48) * mm, "end": v(-13.34, -1.59) * mm});
            skLineSegment(sketch, "E307", {"start": v(-13.34, -1.59) * mm, "end": v(-13.1, -1.72) * mm});
            skLineSegment(sketch, "E308", {"start": v(-13.1, -1.72) * mm, "end": v(-12.97, -1.8) * mm});
            skLineSegment(sketch, "E309", {"start": v(-12.97, -1.8) * mm, "end": v(-12.68, -2) * mm});
            skLineSegment(sketch, "E310", {"start": v(-12.68, -2) * mm, "end": v(-12.67, -1.95) * mm});
            skLineSegment(sketch, "E311", {"start": v(-12.67, -1.95) * mm, "end": v(-12.76, -1.77) * mm});
            skLineSegment(sketch, "E312", {"start": v(-12.76, -1.77) * mm, "end": v(-12.91, -1.43) * mm});
            skLineSegment(sketch, "E313", {"start": v(-12.91, -1.43) * mm, "end": v(-13.04, -1.18) * mm});
            skLineSegment(sketch, "E314", {"start": v(-13.04, -1.18) * mm, "end": v(-13.2, -0.95) * mm});
            skLineSegment(sketch, "E315", {"start": v(-13.2, -0.95) * mm, "end": v(-13.42, -0.64) * mm});
            skLineSegment(sketch, "E316", {"start": v(-13.42, -0.64) * mm, "end": v(-13.57, -0.48) * mm});
            skLineSegment(sketch, "E317", {"start": v(-13.57, -0.48) * mm, "end": v(-13.72, -0.35) * mm});
            skLineSegment(sketch, "E318", {"start": v(-13.72, -0.35) * mm, "end": v(-13.84, -0.25) * mm});
            skLineSegment(sketch, "E319", {"start": v(-13.84, -0.25) * mm, "end": v(-14.2, 0.02) * mm});
            skLineSegment(sketch, "E320", {"start": v(-14.2, 0.02) * mm, "end": v(-14.46, 0.19) * mm});
            skLineSegment(sketch, "E321", {"start": v(-14.46, 0.19) * mm, "end": v(-14.91, 0.4) * mm});
            skLineSegment(sketch, "E322", {"start": v(-14.91, 0.4) * mm, "end": v(-15.5, 0.63) * mm});
            skLineSegment(sketch, "E323", {"start": v(-15.5, 0.63) * mm, "end": v(-16.05, 0.78) * mm});
            skLineSegment(sketch, "E324", {"start": v(-16.05, 0.78) * mm, "end": v(-17.01, 0.99) * mm});
            skLineSegment(sketch, "E325", {"start": v(-17.01, 0.99) * mm, "end": v(-17.5, 1.11) * mm});
            skLineSegment(sketch, "E326", {"start": v(-17.5, 1.11) * mm, "end": v(-18.13, 1.27) * mm});
            skLineSegment(sketch, "E327", {"start": v(-18.13, 1.27) * mm, "end": v(-18.72, 1.45) * mm});
            skLineSegment(sketch, "E328", {"start": v(-18.72, 1.45) * mm, "end": v(-19.4, 1.71) * mm});
            skLineSegment(sketch, "E329", {"start": v(-19.4, 1.71) * mm, "end": v(-19.75, 1.9) * mm});
            skLineSegment(sketch, "E330", {"start": v(-19.75, 1.9) * mm, "end": v(-20, 2.05) * mm});
            skLineSegment(sketch, "E331", {"start": v(-20, 2.05) * mm, "end": v(-20.24, 2.24) * mm});
            skLineSegment(sketch, "E332", {"start": v(-20.24, 2.24) * mm, "end": v(-20.58, 2.52) * mm});
            skLineSegment(sketch, "E333", {"start": v(-20.58, 2.52) * mm, "end": v(-20.82, 2.8) * mm});
            skLineSegment(sketch, "E334", {"start": v(-20.82, 2.8) * mm, "end": v(-20.99, 3.06) * mm});
            skLineSegment(sketch, "E335", {"start": v(-20.99, 3.06) * mm, "end": v(-21.11, 3.3) * mm});
            skLineSegment(sketch, "E336", {"start": v(-21.11, 3.3) * mm, "end": v(-21.38, 3.82) * mm});
            skLineSegment(sketch, "E337", {"start": v(-21.38, 3.82) * mm, "end": v(-21.6, 4.43) * mm});
            skLineSegment(sketch, "E338", {"start": v(-21.6, 4.43) * mm, "end": v(-21.75, 5.02) * mm});
            skLineSegment(sketch, "E339", {"start": v(-21.75, 5.02) * mm, "end": v(-21.87, 5.51) * mm});
            skLineSegment(sketch, "E340", {"start": v(-21.87, 5.51) * mm, "end": v(-22.14, 6.74) * mm});
            skLineSegment(sketch, "E341", {"start": v(-22.14, 6.74) * mm, "end": v(-22.05, 6.5) * mm});
            skLineSegment(sketch, "E342", {"start": v(-22.05, 6.5) * mm, "end": v(-21.86, 6.08) * mm});
            skLineSegment(sketch, "E343", {"start": v(-21.86, 6.08) * mm, "end": v(-21.75, 5.83) * mm});
            skLineSegment(sketch, "E344", {"start": v(-21.75, 5.83) * mm, "end": v(-21.6, 5.6) * mm});
            skLineSegment(sketch, "E345", {"start": v(-21.6, 5.6) * mm, "end": v(-21.43, 5.33) * mm});
            skLineSegment(sketch, "E346", {"start": v(-21.43, 5.33) * mm, "end": v(-21.2, 5.08) * mm});
            skLineSegment(sketch, "E347", {"start": v(-21.2, 5.08) * mm, "end": v(-21, 4.91) * mm});
            skLineSegment(sketch, "E348", {"start": v(-21, 4.91) * mm, "end": v(-20.63, 4.63) * mm});
            skLineSegment(sketch, "E349", {"start": v(-20.63, 4.63) * mm, "end": v(-20.27, 4.42) * mm});
            skLineSegment(sketch, "E350", {"start": v(-20.27, 4.42) * mm, "end": v(-19.85, 4.23) * mm});
            skLineSegment(sketch, "E351", {"start": v(-19.85, 4.23) * mm, "end": v(-19.6, 4.14) * mm});
            skLineSegment(sketch, "E352", {"start": v(-19.6, 4.14) * mm, "end": v(-18.97, 3.93) * mm});
            skLineSegment(sketch, "E353", {"start": v(-18.97, 3.93) * mm, "end": v(-18.38, 3.8) * mm});
            skLineSegment(sketch, "E354", {"start": v(-18.38, 3.8) * mm, "end": v(-17.51, 3.61) * mm});
            skLineSegment(sketch, "E355", {"start": v(-17.51, 3.61) * mm, "end": v(-18.02, 3.95) * mm});
            skLineSegment(sketch, "E356", {"start": v(-18.02, 3.95) * mm, "end": v(-18.34, 4.17) * mm});
            skLineSegment(sketch, "E357", {"start": v(-18.34, 4.17) * mm, "end": v(-18.76, 4.46) * mm});
            skLineSegment(sketch, "E358", {"start": v(-18.76, 4.46) * mm, "end": v(-19.12, 4.72) * mm});
            skLineSegment(sketch, "E359", {"start": v(-19.12, 4.72) * mm, "end": v(-19.43, 4.97) * mm});
            skLineSegment(sketch, "E360", {"start": v(-19.43, 4.97) * mm, "end": v(-19.9, 5.38) * mm});
            skLineSegment(sketch, "E361", {"start": v(-19.9, 5.38) * mm, "end": v(-20.28, 5.72) * mm});
            skLineSegment(sketch, "E362", {"start": v(-20.28, 5.72) * mm, "end": v(-20.56, 6) * mm});
            skLineSegment(sketch, "E363", {"start": v(-20.56, 6) * mm, "end": v(-20.73, 6.2) * mm});
            skLineSegment(sketch, "E364", {"start": v(-20.73, 6.2) * mm, "end": v(-21.38, 6.98) * mm});
            skLineSegment(sketch, "E365", {"start": v(-21.38, 6.98) * mm, "end": v(-21.87, 7.75) * mm});
            skLineSegment(sketch, "E366", {"start": v(-21.87, 7.75) * mm, "end": v(-22.1, 8.18) * mm});
            skLineSegment(sketch, "E367", {"start": v(-22.1, 8.18) * mm, "end": v(-22.44, 8.94) * mm});
            skLineSegment(sketch, "E368", {"start": v(-22.44, 8.94) * mm, "end": v(-22.59, 9.34) * mm});
            skLineSegment(sketch, "E369", {"start": v(-22.59, 9.34) * mm, "end": v(-22.72, 9.75) * mm});
            skLineSegment(sketch, "E370", {"start": v(-22.72, 9.75) * mm, "end": v(-22.94, 10.56) * mm});
            skLineSegment(sketch, "E371", {"start": v(-22.94, 10.56) * mm, "end": v(-23.1, 11.32) * mm});
            skLineSegment(sketch, "E372", {"start": v(-23.1, 11.32) * mm, "end": v(-23.21, 11.89) * mm});
            skLineSegment(sketch, "E373", {"start": v(-23.21, 11.89) * mm, "end": v(-23.23, 12.1) * mm});
            skLineSegment(sketch, "E374", {"start": v(-23.23, 12.1) * mm, "end": v(-23.14, 12) * mm});
            skLineSegment(sketch, "E375", {"start": v(-23.14, 12) * mm, "end": v(-23, 11.77) * mm});
            skLineSegment(sketch, "E376", {"start": v(-23, 11.77) * mm, "end": v(-22.9, 11.6) * mm});
            skLineSegment(sketch, "E377", {"start": v(-22.9, 11.6) * mm, "end": v(-22.6, 11.12) * mm});
            skLineSegment(sketch, "E378", {"start": v(-22.6, 11.12) * mm, "end": v(-22.47, 10.89) * mm});
            skLineSegment(sketch, "E379", {"start": v(-22.47, 10.89) * mm, "end": v(-22.4, 10.74) * mm});
            skLineSegment(sketch, "E380", {"start": v(-22.4, 10.74) * mm, "end": v(-22.27, 10.58) * mm});
            skLineSegment(sketch, "E381", {"start": v(-22.27, 10.58) * mm, "end": v(-22.06, 10.34) * mm});
            skLineSegment(sketch, "E382", {"start": v(-22.06, 10.34) * mm, "end": v(-21.84, 10.12) * mm});
            skLineSegment(sketch, "E383", {"start": v(-21.84, 10.12) * mm, "end": v(-21.57, 9.83) * mm});
            skLineSegment(sketch, "E384", {"start": v(-21.57, 9.83) * mm, "end": v(-21.43, 9.7) * mm});
            skLineSegment(sketch, "E385", {"start": v(-21.43, 9.7) * mm, "end": v(-21.25, 9.5) * mm});
            skLineSegment(sketch, "E386", {"start": v(-21.25, 9.5) * mm, "end": v(-21.3, 9.73) * mm});
            skLineSegment(sketch, "E387", {"start": v(-21.3, 9.73) * mm, "end": v(-21.38, 9.92) * mm});
            skLineSegment(sketch, "E388", {"start": v(-21.38, 9.92) * mm, "end": v(-21.45, 10.17) * mm});
            skLineSegment(sketch, "E389", {"start": v(-21.45, 10.17) * mm, "end": v(-21.8, 11.16) * mm});
            skLineSegment(sketch, "E390", {"start": v(-21.8, 11.16) * mm, "end": v(-21.94, 11.67) * mm});
            skLineSegment(sketch, "E391", {"start": v(-21.94, 11.67) * mm, "end": v(-22.2, 13.07) * mm});
            skLineSegment(sketch, "E392", {"start": v(-22.2, 13.07) * mm, "end": v(-22.28, 13.81) * mm});
            skLineSegment(sketch, "E393", {"start": v(-22.28, 13.81) * mm, "end": v(-22.28, 14.63) * mm});
            skLineSegment(sketch, "E394", {"start": v(-22.28, 14.63) * mm, "end": v(-22.17, 15.47) * mm});
            skLineSegment(sketch, "E395", {"start": v(-22.17, 15.47) * mm, "end": v(-21.97, 16.42) * mm});
            skLineSegment(sketch, "E396", {"start": v(-21.97, 16.42) * mm, "end": v(-21.8, 17.04) * mm});
            skLineSegment(sketch, "E397", {"start": v(-21.8, 17.04) * mm, "end": v(-21.67, 17.54) * mm});
            skLineSegment(sketch, "E398", {"start": v(-21.67, 17.54) * mm, "end": v(-21.65, 17.26) * mm});
            skLineSegment(sketch, "E399", {"start": v(-21.65, 17.26) * mm, "end": v(-21.6, 16.52) * mm});
            skLineSegment(sketch, "E400", {"start": v(-21.6, 16.52) * mm, "end": v(-21.54, 15.72) * mm});
            skLineSegment(sketch, "E401", {"start": v(-21.54, 15.72) * mm, "end": v(-21.4, 14.57) * mm});
            skLineSegment(sketch, "E402", {"start": v(-21.4, 14.57) * mm, "end": v(-21.2, 13.39) * mm});
            skLineSegment(sketch, "E403", {"start": v(-21.2, 13.39) * mm, "end": v(-20.96, 12.52) * mm});
            skLineSegment(sketch, "E404", {"start": v(-20.96, 12.52) * mm, "end": v(-20.78, 12.03) * mm});
            skLineSegment(sketch, "E405", {"start": v(-20.78, 12.03) * mm, "end": v(-20.64, 11.7) * mm});
            skLineSegment(sketch, "E406", {"start": v(-20.64, 11.7) * mm, "end": v(-20.4, 11.23) * mm});
            skLineSegment(sketch, "E407", {"start": v(-20.4, 11.23) * mm, "end": v(-20.1, 10.74) * mm});
            skLineSegment(sketch, "E408", {"start": v(-20.1, 10.74) * mm, "end": v(-19.87, 10.44) * mm});
            skLineSegment(sketch, "E409", {"start": v(-19.87, 10.44) * mm, "end": v(-19.55, 10.1) * mm});
            skLineSegment(sketch, "E410", {"start": v(-19.55, 10.1) * mm, "end": v(-19.27, 9.86) * mm});
            skLineSegment(sketch, "E411", {"start": v(-19.27, 9.86) * mm, "end": v(-18.9, 9.59) * mm});
            skLineSegment(sketch, "E412", {"start": v(-18.9, 9.59) * mm, "end": v(-18.2, 9.25) * mm});
            skLineSegment(sketch, "E413", {"start": v(-18.2, 9.25) * mm, "end": v(-17.45, 9.02) * mm});
            skLineSegment(sketch, "E414", {"start": v(-17.45, 9.02) * mm, "end": v(-16.77, 8.93) * mm});
            skLineSegment(sketch, "E415", {"start": v(-16.77, 8.93) * mm, "end": v(-15.31, 8.86) * mm});
            skLineSegment(sketch, "E416", {"start": v(-15.31, 8.86) * mm, "end": v(-13.93, 8.83) * mm});
            skLineSegment(sketch, "E417", {"start": v(-13.93, 8.83) * mm, "end": v(-13.1, 8.76) * mm});
            skLineSegment(sketch, "E418", {"start": v(-13.1, 8.76) * mm, "end": v(-12.17, 8.57) * mm});
            skLineSegment(sketch, "E419", {"start": v(-12.17, 8.57) * mm, "end": v(-11.43, 8.35) * mm});
            skLineSegment(sketch, "E420", {"start": v(-11.43, 8.35) * mm, "end": v(-11, 8.2) * mm});
            skLineSegment(sketch, "E421", {"start": v(-11, 8.2) * mm, "end": v(-10.6, 8) * mm});
            skLineSegment(sketch, "E422", {"start": v(-10.6, 8) * mm, "end": v(-10.11, 7.73) * mm});
            skLineSegment(sketch, "E423", {"start": v(-10.11, 7.73) * mm, "end": v(-9.53, 7.38) * mm});
            skLineSegment(sketch, "E424", {"start": v(-9.53, 7.38) * mm, "end": v(-9.19, 7.08) * mm});
            skLineSegment(sketch, "E425", {"start": v(-9.19, 7.08) * mm, "end": v(-8.62, 6.55) * mm});
            skLineSegment(sketch, "E426", {"start": v(-8.62, 6.55) * mm, "end": v(-8.23, 6.1) * mm});
            skLineSegment(sketch, "E427", {"start": v(-8.23, 6.1) * mm, "end": v(-8.03, 5.84) * mm});
            skLineSegment(sketch, "E428", {"start": v(-8.03, 5.84) * mm, "end": v(-7.86, 5.58) * mm});
            skLineSegment(sketch, "E429", {"start": v(-7.86, 5.58) * mm, "end": v(-7.68, 5.28) * mm});
            skLineSegment(sketch, "E430", {"start": v(-7.68, 5.28) * mm, "end": v(-7.37, 4.74) * mm});
            skLineSegment(sketch, "E431", {"start": v(-7.37, 4.74) * mm, "end": v(-7.09, 4.1) * mm});
            skLineSegment(sketch, "E432", {"start": v(-7.09, 4.1) * mm, "end": v(-6.84, 3.5) * mm});
            skLineSegment(sketch, "E433", {"start": v(-6.84, 3.5) * mm, "end": v(-6.6, 2.87) * mm});
            skLineSegment(sketch, "E434", {"start": v(-12.28, 3.56) * mm, "end": v(-12.38, 4.19) * mm});
            skLineSegment(sketch, "E435", {"start": v(-12.38, 4.19) * mm, "end": v(-12.52, 4.86) * mm});
            skLineSegment(sketch, "E436", {"start": v(-12.52, 4.86) * mm, "end": v(-12.7, 5.43) * mm});
            skLineSegment(sketch, "E437", {"start": v(-12.7, 5.43) * mm, "end": v(-12.94, 5.97) * mm});
            skLineSegment(sketch, "E438", {"start": v(-12.94, 5.97) * mm, "end": v(-13.4, 6.47) * mm});
            skLineSegment(sketch, "E439", {"start": v(-13.4, 6.47) * mm, "end": v(-14.01, 6.8) * mm});
            skLineSegment(sketch, "E440", {"start": v(-14.01, 6.8) * mm, "end": v(-14.87, 6.99) * mm});
            skLineSegment(sketch, "E441", {"start": v(-14.87, 6.99) * mm, "end": v(-16.03, 7.12) * mm});
            skLineSegment(sketch, "E442", {"start": v(-16.03, 7.12) * mm, "end": v(-17.68, 7.35) * mm});
            skLineSegment(sketch, "E443", {"start": v(-17.68, 7.35) * mm, "end": v(-18.93, 7.6) * mm});
            skLineSegment(sketch, "E444", {"start": v(-18.93, 7.6) * mm, "end": v(-20.23, 8.1) * mm});
            skLineSegment(sketch, "E445", {"start": v(-20.23, 8.1) * mm, "end": v(-19.88, 7.6) * mm});
            skLineSegment(sketch, "E446", {"start": v(-19.88, 7.6) * mm, "end": v(-19.43, 7.17) * mm});
            skLineSegment(sketch, "E447", {"start": v(-19.43, 7.17) * mm, "end": v(-18.98, 6.76) * mm});
            skLineSegment(sketch, "E448", {"start": v(-18.98, 6.76) * mm, "end": v(-18.4, 6.43) * mm});
            skLineSegment(sketch, "E449", {"start": v(-18.4, 6.43) * mm, "end": v(-17.88, 6.2) * mm});
            skLineSegment(sketch, "E450", {"start": v(-17.88, 6.2) * mm, "end": v(-17.38, 6.01) * mm});
            skLineSegment(sketch, "E451", {"start": v(-17.38, 6.01) * mm, "end": v(-16.8, 5.83) * mm});
            skLineSegment(sketch, "E452", {"start": v(-16.8, 5.83) * mm, "end": v(-16.2, 5.66) * mm});
            skLineSegment(sketch, "E453", {"start": v(-16.2, 5.66) * mm, "end": v(-15.61, 5.5) * mm});
            skLineSegment(sketch, "E454", {"start": v(-15.61, 5.5) * mm, "end": v(-14.93, 5.29) * mm});
            skLineSegment(sketch, "E455", {"start": v(-14.93, 5.29) * mm, "end": v(-14.32, 5.05) * mm});
            skLineSegment(sketch, "E456", {"start": v(-14.32, 5.05) * mm, "end": v(-13.87, 4.83) * mm});
            skLineSegment(sketch, "E457", {"start": v(-13.87, 4.83) * mm, "end": v(-13.56, 4.65) * mm});
            skLineSegment(sketch, "E458", {"start": v(-13.56, 4.65) * mm, "end": v(-13.26, 4.46) * mm});
            skLineSegment(sketch, "E459", {"start": v(-13.26, 4.46) * mm, "end": v(-12.83, 4.12) * mm});
            skLineSegment(sketch, "E460", {"start": v(-12.83, 4.12) * mm, "end": v(-12.54, 3.83) * mm});
            skLineSegment(sketch, "E461", {"start": v(-12.54, 3.83) * mm, "end": v(-12.28, 3.56) * mm});
            skLineSegment(sketch, "E462.MirrorCS", {"start": v(7.52, -4.97) * mm, "end": v(7.83, -5.05) * mm});
            skLineSegment(sketch, "E463.MirrorCS", {"start": v(10.8, -4.75) * mm, "end": v(10.76, -4.8) * mm});
            skLineSegment(sketch, "E464.MirrorCS", {"start": v(10.25, -5.37) * mm, "end": v(10.23, -5.4) * mm});
            skLineSegment(sketch, "E465.MirrorCS", {"start": v(11, -6.3) * mm, "end": v(11.16, -6.17) * mm});
            skLineSegment(sketch, "E466.MirrorCS", {"start": v(10.48, -5.15) * mm, "end": v(10.46, -5.18) * mm});
            skLineSegment(sketch, "E467.MirrorCS", {"start": v(9.97, -5.07) * mm, "end": v(10.06, -5.03) * mm});
            skLineSegment(sketch, "E468.MirrorCS", {"start": v(10.12, -5.5) * mm, "end": v(10.07, -5.53) * mm});
            skLineSegment(sketch, "E469.MirrorCS", {"start": v(10.15, -5.46) * mm, "end": v(10.12, -5.5) * mm});
            skLineSegment(sketch, "E470.MirrorCS", {"start": v(10.76, -4.8) * mm, "end": v(10.71, -4.86) * mm});
            skLineSegment(sketch, "E471.MirrorCS", {"start": v(11.16, -6.17) * mm, "end": v(11.26, -6.08) * mm});
            skLineSegment(sketch, "E472.MirrorCS", {"start": v(9.25, -5.99) * mm, "end": v(9.04, -6.03) * mm});
            skLineSegment(sketch, "E473.MirrorCS", {"start": v(10.06, -5.03) * mm, "end": v(10.15, -5) * mm});
            skLineSegment(sketch, "E474.MirrorCS", {"start": v(10.15, -5) * mm, "end": v(10.23, -4.97) * mm});
            skLineSegment(sketch, "E475.MirrorCS", {"start": v(9.86, -5.1) * mm, "end": v(9.97, -5.07) * mm});
            skLineSegment(sketch, "E476.MirrorCS", {"start": v(9.97, -5.6) * mm, "end": v(9.88, -5.68) * mm});
            skLineSegment(sketch, "E477.MirrorCS", {"start": v(10.73, -4.7) * mm, "end": v(10.86, -4.63) * mm});
            skLineSegment(sketch, "E478.MirrorCS", {"start": v(8.99, -5.2) * mm, "end": v(9.15, -5.2) * mm});
            skLineSegment(sketch, "E479.MirrorCS", {"start": v(9.88, -5.68) * mm, "end": v(9.77, -5.75) * mm});
            skLineSegment(sketch, "E480.MirrorCS", {"start": v(10.71, -4.86) * mm, "end": v(10.68, -4.9) * mm});
            skLineSegment(sketch, "E481.MirrorCS", {"start": v(10.3, -5.34) * mm, "end": v(10.25, -5.37) * mm});
            skLineSegment(sketch, "E482.MirrorCS", {"start": v(10.68, -4.9) * mm, "end": v(10.65, -4.94) * mm});
            skLineSegment(sketch, "E483.MirrorCS", {"start": v(11.26, -6.08) * mm, "end": v(11.32, -6.01) * mm});
            skLineSegment(sketch, "E484.MirrorCS", {"start": v(10.46, -5.18) * mm, "end": v(10.42, -5.2) * mm});
            skLineSegment(sketch, "E485.MirrorCS", {"start": v(7.7, -6) * mm, "end": v(7.57, -5.97) * mm});
            skLineSegment(sketch, "E486.MirrorCS", {"start": v(10.84, -4.69) * mm, "end": v(10.8, -4.75) * mm});
            skLineSegment(sketch, "E487.MirrorCS", {"start": v(10.55, -5.06) * mm, "end": v(10.52, -5.1) * mm});
            skLineSegment(sketch, "E488.MirrorCS", {"start": v(10.62, -4.77) * mm, "end": v(10.73, -4.7) * mm});
            skLineSegment(sketch, "E489.MirrorCS", {"start": v(10.56, -4.8) * mm, "end": v(10.62, -4.77) * mm});
            skLineSegment(sketch, "E490.MirrorCS", {"start": v(10.42, -5.2) * mm, "end": v(10.4, -5.24) * mm});
            skLineSegment(sketch, "E491.MirrorCS", {"start": v(10.23, -5.4) * mm, "end": v(10.2, -5.43) * mm});
            skLineSegment(sketch, "E492.MirrorCS", {"start": v(9.77, -5.75) * mm, "end": v(9.64, -5.82) * mm});
            skLineSegment(sketch, "E493.MirrorCS", {"start": v(10.23, -4.97) * mm, "end": v(10.32, -4.93) * mm});
            skLineSegment(sketch, "E494.MirrorCS", {"start": v(10.52, -5.1) * mm, "end": v(10.48, -5.15) * mm});
            skLineSegment(sketch, "E495.MirrorCS", {"start": v(10.07, -5.53) * mm, "end": v(10.04, -5.56) * mm});
            skLineSegment(sketch, "E496.MirrorCS", {"start": v(9.64, -5.82) * mm, "end": v(9.52, -5.89) * mm});
            skLineSegment(sketch, "E497.MirrorCS", {"start": v(10.33, -5.3) * mm, "end": v(10.3, -5.34) * mm});
            skLineSegment(sketch, "E498.MirrorCS", {"start": v(10.4, -5.24) * mm, "end": v(10.36, -5.27) * mm});
            skLineSegment(sketch, "E499.MirrorCS", {"start": v(10.04, -5.56) * mm, "end": v(9.97, -5.6) * mm});
            skLineSegment(sketch, "E500.MirrorCS", {"start": v(10.58, -5.02) * mm, "end": v(10.55, -5.06) * mm});
            skLineSegment(sketch, "E501.MirrorCS", {"start": v(9.74, -5.13) * mm, "end": v(9.86, -5.1) * mm});
            skLineSegment(sketch, "E502.MirrorCS", {"start": v(10.2, -5.43) * mm, "end": v(10.15, -5.46) * mm});
            skLineSegment(sketch, "E503.MirrorCS", {"start": v(8.81, -6.07) * mm, "end": v(8.68, -6.08) * mm});
            skLineSegment(sketch, "E504.MirrorCS", {"start": v(10.5, -4.84) * mm, "end": v(10.56, -4.8) * mm});
            skLineSegment(sketch, "E505.MirrorCS", {"start": v(9.59, -5.17) * mm, "end": v(9.74, -5.13) * mm});
            skLineSegment(sketch, "E506.MirrorCS", {"start": v(10.32, -4.93) * mm, "end": v(10.38, -4.9) * mm});
            skLineSegment(sketch, "E507.MirrorCS", {"start": v(7.57, -5.97) * mm, "end": v(7.45, -5.94) * mm});
            skLineSegment(sketch, "E508.MirrorCS", {"start": v(10.43, -4.87) * mm, "end": v(10.5, -4.84) * mm});
            skLineSegment(sketch, "E509.MirrorCS", {"start": v(9.39, -5.19) * mm, "end": v(9.59, -5.17) * mm});
            skLineSegment(sketch, "E510.MirrorCS", {"start": v(10.62, -4.98) * mm, "end": v(10.58, -5.02) * mm});
            skLineSegment(sketch, "E511.MirrorCS", {"start": v(10.36, -5.27) * mm, "end": v(10.33, -5.3) * mm});
            skLineSegment(sketch, "E512.MirrorCS", {"start": v(10.86, -4.63) * mm, "end": v(10.84, -4.69) * mm});
            skLineSegment(sketch, "E513.MirrorCS", {"start": v(7.88, -6.04) * mm, "end": v(7.7, -6) * mm});
            skLineSegment(sketch, "E514.MirrorCS", {"start": v(10.38, -4.9) * mm, "end": v(10.43, -4.87) * mm});
            skLineSegment(sketch, "E515.MirrorCS", {"start": v(10.65, -4.94) * mm, "end": v(10.62, -4.98) * mm});
            skLineSegment(sketch, "E516.MirrorCS", {"start": v(9.04, -6.03) * mm, "end": v(8.81, -6.07) * mm});
            skLineSegment(sketch, "E517.MirrorCS", {"start": v(8.68, -6.08) * mm, "end": v(8.22, -6.07) * mm});
            skLineSegment(sketch, "E518.MirrorCS", {"start": v(7.83, -5.05) * mm, "end": v(8.06, -5.1) * mm});
            skLineSegment(sketch, "E519.MirrorCS", {"start": v(8.06, -5.1) * mm, "end": v(8.4, -5.15) * mm});
            skLineSegment(sketch, "E520.MirrorCS", {"start": v(8.4, -5.15) * mm, "end": v(8.64, -5.18) * mm});
            skLineSegment(sketch, "E521.MirrorCS", {"start": v(8.22, -6.07) * mm, "end": v(7.88, -6.04) * mm});
            skLineSegment(sketch, "E522.MirrorCS", {"start": v(9.15, -5.2) * mm, "end": v(9.39, -5.19) * mm});
            skLineSegment(sketch, "E523.MirrorCS", {"start": v(9.38, -5.94) * mm, "end": v(9.25, -5.99) * mm});
            skLineSegment(sketch, "E524.MirrorCS", {"start": v(8.64, -5.18) * mm, "end": v(8.99, -5.2) * mm});
            skLineSegment(sketch, "E525.MirrorCS", {"start": v(1.8, -5.16) * mm, "end": v(1.76, -5.2) * mm});
            skLineSegment(sketch, "E526.MirrorCS", {"start": v(11.32, -6.01) * mm, "end": v(11.42, -5.9) * mm});
            skLineSegment(sketch, "E527.MirrorCS", {"start": v(1.68, -4.44) * mm, "end": v(1.74, -4.4) * mm});
            skLineSegment(sketch, "E528.MirrorCS", {"start": v(1.83, -5.13) * mm, "end": v(1.8, -5.16) * mm});
            skLineSegment(sketch, "E529.MirrorCS", {"start": v(1.73, -4.14) * mm, "end": v(1.61, -4.28) * mm});
            skLineSegment(sketch, "E530.MirrorCS", {"start": v(11.42, -5.9) * mm, "end": v(11.49, -5.82) * mm});
            skLineSegment(sketch, "E531.MirrorCS", {"start": v(1.44, -5.48) * mm, "end": v(1.37, -5.55) * mm});
            skLineSegment(sketch, "E532.MirrorCS", {"start": v(2.03, -4.28) * mm, "end": v(2.13, -4.25) * mm});
            skLineSegment(sketch, "E533.MirrorCS", {"start": v(2.1, -4.97) * mm, "end": v(1.94, -5.06) * mm});
            skLineSegment(sketch, "E534.MirrorCS", {"start": v(1.61, -4.28) * mm, "end": v(1.53, -4.4) * mm});
            skLineSegment(sketch, "E535.MirrorCS", {"start": v(2.15, -3.64) * mm, "end": v(1.98, -3.84) * mm});
            skLineSegment(sketch, "E536.MirrorCS", {"start": v(1.76, -5.2) * mm, "end": v(1.73, -5.22) * mm});
            skLineSegment(sketch, "E537.MirrorCS", {"start": v(1.82, -4.37) * mm, "end": v(1.91, -4.33) * mm});
            skLineSegment(sketch, "E538.MirrorCS", {"start": v(1.4, -4.59) * mm, "end": v(1.49, -4.54) * mm});
            skLineSegment(sketch, "E539.MirrorCS", {"start": v(1.57, -4.48) * mm, "end": v(1.68, -4.44) * mm});
            skLineSegment(sketch, "E540.MirrorCS", {"start": v(1.37, -5.55) * mm, "end": v(1.21, -5.73) * mm});
            skLineSegment(sketch, "E541.MirrorCS", {"start": v(2.43, -4.84) * mm, "end": v(2.26, -4.9) * mm});
            skLineSegment(sketch, "E542.MirrorCS", {"start": v(1.21, -5.73) * mm, "end": v(1.16, -5.79) * mm});
            skLineSegment(sketch, "E543.MirrorCS", {"start": v(1.73, -5.22) * mm, "end": v(1.67, -5.26) * mm});
            skLineSegment(sketch, "E544.MirrorCS", {"start": v(2.3, -3.48) * mm, "end": v(2.15, -3.64) * mm});
            skLineSegment(sketch, "E545.MirrorCS", {"start": v(1.74, -4.4) * mm, "end": v(1.82, -4.37) * mm});
            skLineSegment(sketch, "E546.MirrorCS", {"start": v(2.13, -4.25) * mm, "end": v(2.27, -4.2) * mm});
            skLineSegment(sketch, "E547.MirrorCS", {"start": v(1.94, -5.06) * mm, "end": v(1.88, -5.1) * mm});
            skLineSegment(sketch, "E548.MirrorCS", {"start": v(1.45, -4.52) * mm, "end": v(1.4, -4.59) * mm});
            skLineSegment(sketch, "E549.MirrorCS", {"start": v(2.4, -6.07) * mm, "end": v(2.68, -5.9) * mm});
            skLineSegment(sketch, "E550.MirrorCS", {"start": v(9.52, -5.89) * mm, "end": v(9.38, -5.94) * mm});
            skLineSegment(sketch, "E551.MirrorCS", {"start": v(1.49, -4.54) * mm, "end": v(1.57, -4.48) * mm});
            skLineSegment(sketch, "E552.MirrorCS", {"start": v(1.88, -5.1) * mm, "end": v(1.83, -5.13) * mm});
            skLineSegment(sketch, "E553.MirrorCS", {"start": v(11.7, -5.44) * mm, "end": v(11.76, -5.32) * mm});
            skLineSegment(sketch, "E554.MirrorCS", {"start": v(1.53, -4.4) * mm, "end": v(1.45, -4.52) * mm});
            skLineSegment(sketch, "E555.MirrorCS", {"start": v(1.98, -3.84) * mm, "end": v(1.85, -4) * mm});
            skLineSegment(sketch, "E556.MirrorCS", {"start": v(2.44, -4.15) * mm, "end": v(2.55, -4.13) * mm});
            skLineSegment(sketch, "E557.MirrorCS", {"start": v(2.55, -4.8) * mm, "end": v(2.43, -4.84) * mm});
            skLineSegment(sketch, "E558.MirrorCS", {"start": v(2.68, -4.77) * mm, "end": v(2.55, -4.8) * mm});
            skLineSegment(sketch, "E559.MirrorCS", {"start": v(1.85, -4) * mm, "end": v(1.73, -4.14) * mm});
            skLineSegment(sketch, "E560.MirrorCS", {"start": v(1.91, -4.33) * mm, "end": v(2.03, -4.28) * mm});
            skLineSegment(sketch, "E561.MirrorCS", {"start": v(2.27, -4.2) * mm, "end": v(2.44, -4.15) * mm});
            skLineSegment(sketch, "E562.MirrorCS", {"start": v(1.67, -5.26) * mm, "end": v(1.44, -5.48) * mm});
            skLineSegment(sketch, "E563.MirrorCS", {"start": v(2.26, -4.9) * mm, "end": v(2.1, -4.97) * mm});
            skLineSegment(sketch, "E564.MirrorCS", {"start": v(11.76, -5.32) * mm, "end": v(11.83, -5.18) * mm});
            skLineSegment(sketch, "E565.MirrorCS", {"start": v(11.55, -5.72) * mm, "end": v(11.63, -5.57) * mm});
            skLineSegment(sketch, "E566.MirrorCS", {"start": v(11.87, -5.04) * mm, "end": v(11.92, -4.92) * mm});
            skLineSegment(sketch, "E567.MirrorCS", {"start": v(11.63, -5.57) * mm, "end": v(11.7, -5.44) * mm});
            skLineSegment(sketch, "E568.MirrorCS", {"start": v(2.55, -4.13) * mm, "end": v(2.78, -4.1) * mm});
            skLineSegment(sketch, "E569.MirrorCS", {"start": v(11.83, -5.18) * mm, "end": v(11.87, -5.04) * mm});
            skLineSegment(sketch, "E570.MirrorCS", {"start": v(3.01, -4.06) * mm, "end": v(3.17, -4.04) * mm});
            skLineSegment(sketch, "E571.MirrorCS", {"start": v(2.9, -4.74) * mm, "end": v(2.68, -4.77) * mm});
            skLineSegment(sketch, "E572.MirrorCS", {"start": v(3.41, -4.73) * mm, "end": v(2.9, -4.74) * mm});
            skLineSegment(sketch, "E573.MirrorCS", {"start": v(3.3, -4.03) * mm, "end": v(3.45, -4.03) * mm});
            skLineSegment(sketch, "E574.MirrorCS", {"start": v(4.35, -5.73) * mm, "end": v(4.53, -5.8) * mm});
            skLineSegment(sketch, "E575.MirrorCS", {"start": v(2.78, -4.1) * mm, "end": v(3.01, -4.06) * mm});
            skLineSegment(sketch, "E576.MirrorCS", {"start": v(3.17, -4.04) * mm, "end": v(3.3, -4.03) * mm});
            skLineSegment(sketch, "E577.MirrorCS", {"start": v(7.22, -5.88) * mm, "end": v(7.1, -5.84) * mm});
            skLineSegment(sketch, "E578.MirrorCS", {"start": v(5.81, -4.42) * mm, "end": v(5.95, -4.47) * mm});
            skLineSegment(sketch, "E579.MirrorCS", {"start": v(4.8, -5.89) * mm, "end": v(5.06, -5.99) * mm});
            skLineSegment(sketch, "E580.MirrorCS", {"start": v(5.6, -4.37) * mm, "end": v(5.81, -4.42) * mm});
            skLineSegment(sketch, "E581.MirrorCS", {"start": v(5.53, -5.3) * mm, "end": v(5.4, -5.25) * mm});
            skLineSegment(sketch, "E582.MirrorCS", {"start": v(6.05, -5.49) * mm, "end": v(5.91, -5.43) * mm});
            skLineSegment(sketch, "E583.MirrorCS", {"start": v(5.91, -5.43) * mm, "end": v(5.74, -5.37) * mm});
            skLineSegment(sketch, "E584.MirrorCS", {"start": v(12.3, -3.9) * mm, "end": v(12.34, -3.82) * mm});
            skLineSegment(sketch, "E585.MirrorCS", {"start": v(4.53, -5.8) * mm, "end": v(4.8, -5.89) * mm});
            skLineSegment(sketch, "E586.MirrorCS", {"start": v(4.72, -5.02) * mm, "end": v(4.44, -4.93) * mm});
            skLineSegment(sketch, "E587.MirrorCS", {"start": v(6.08, -4.5) * mm, "end": v(6.22, -4.55) * mm});
            skLineSegment(sketch, "E588.MirrorCS", {"start": v(6.36, -4.6) * mm, "end": v(6.5, -4.66) * mm});
            skLineSegment(sketch, "E589.MirrorCS", {"start": v(6.8, -5.75) * mm, "end": v(6.7, -5.72) * mm});
            skLineSegment(sketch, "E590.MirrorCS", {"start": v(5.32, -4.28) * mm, "end": v(5.6, -4.37) * mm});
            skLineSegment(sketch, "E591.MirrorCS", {"start": v(5.4, -5.25) * mm, "end": v(5.23, -5.18) * mm});
            skLineSegment(sketch, "E592.MirrorCS", {"start": v(7, -5.8) * mm, "end": v(6.9, -5.78) * mm});
            skLineSegment(sketch, "E593.MirrorCS", {"start": v(6.81, -4.75) * mm, "end": v(6.95, -4.79) * mm});
            skLineSegment(sketch, "E594.MirrorCS", {"start": v(4.14, -5.66) * mm, "end": v(4.35, -5.73) * mm});
            skLineSegment(sketch, "E595.MirrorCS", {"start": v(5.1, -5.13) * mm, "end": v(4.72, -5.02) * mm});
            skLineSegment(sketch, "E596.MirrorCS", {"start": v(5.74, -5.37) * mm, "end": v(5.53, -5.3) * mm});
            skLineSegment(sketch, "E597.MirrorCS", {"start": v(5.95, -4.47) * mm, "end": v(6.08, -4.5) * mm});
            skLineSegment(sketch, "E598.MirrorCS", {"start": v(7.32, -5.91) * mm, "end": v(7.22, -5.88) * mm});
            skLineSegment(sketch, "E599.MirrorCS", {"start": v(5.1, -4.23) * mm, "end": v(5.32, -4.28) * mm});
            skLineSegment(sketch, "E600.MirrorCS", {"start": v(3.45, -4.03) * mm, "end": v(3.67, -4.04) * mm});
            skLineSegment(sketch, "E601.MirrorCS", {"start": v(6.62, -5.68) * mm, "end": v(6.54, -5.66) * mm});
            skLineSegment(sketch, "E602.MirrorCS", {"start": v(5.23, -5.18) * mm, "end": v(5.1, -5.13) * mm});
            skLineSegment(sketch, "E603.MirrorCS", {"start": v(6.7, -5.72) * mm, "end": v(6.62, -5.68) * mm});
            skLineSegment(sketch, "E604.MirrorCS", {"start": v(7.1, -5.84) * mm, "end": v(7, -5.8) * mm});
            skLineSegment(sketch, "E605.MirrorCS", {"start": v(4.44, -4.93) * mm, "end": v(4.12, -4.85) * mm});
            skLineSegment(sketch, "E606.MirrorCS", {"start": v(3.5, -5.63) * mm, "end": v(3.98, -5.61) * mm});
            skLineSegment(sketch, "E607.MirrorCS", {"start": v(3.98, -5.61) * mm, "end": v(4.14, -5.66) * mm});
            skLineSegment(sketch, "E608.MirrorCS", {"start": v(12.68, -3.03) * mm, "end": v(12.81, -2.79) * mm});
            skLineSegment(sketch, "E609.MirrorCS", {"start": v(12.34, -3.82) * mm, "end": v(12.36, -3.74) * mm});
            skLineSegment(sketch, "E610.MirrorCS", {"start": v(6.54, -5.66) * mm, "end": v(6.26, -5.56) * mm});
            skLineSegment(sketch, "E611.MirrorCS", {"start": v(6.9, -5.78) * mm, "end": v(6.8, -5.75) * mm});
            skLineSegment(sketch, "E612.MirrorCS", {"start": v(11.72, -2) * mm, "end": v(11.71, -1.95) * mm});
            skLineSegment(sketch, "E613.MirrorCS", {"start": v(6.22, -4.55) * mm, "end": v(6.36, -4.6) * mm});
            skLineSegment(sketch, "E614.MirrorCS", {"start": v(6.68, -6.57) * mm, "end": v(6.8, -6.6) * mm});
            skLineSegment(sketch, "E615.MirrorCS", {"start": v(7.09, -4.84) * mm, "end": v(7.26, -4.89) * mm});
            skLineSegment(sketch, "E616.MirrorCS", {"start": v(12.08, -4.5) * mm, "end": v(12.15, -4.3) * mm});
            skLineSegment(sketch, "E617.MirrorCS", {"start": v(3.9, -4.8) * mm, "end": v(3.62, -4.76) * mm});
            skLineSegment(sketch, "E618.MirrorCS", {"start": v(4.12, -4.85) * mm, "end": v(3.9, -4.8) * mm});
            skLineSegment(sketch, "E619.MirrorCS", {"start": v(3.62, -4.76) * mm, "end": v(3.41, -4.73) * mm});
            skLineSegment(sketch, "E620.MirrorCS", {"start": v(3.31, -5.66) * mm, "end": v(3.5, -5.63) * mm});
            skLineSegment(sketch, "E621.MirrorCS", {"start": v(6.26, -5.56) * mm, "end": v(6.05, -5.49) * mm});
            skLineSegment(sketch, "E622.MirrorCS", {"start": v(3.67, -4.04) * mm, "end": v(3.94, -4.06) * mm});
            skLineSegment(sketch, "E623.MirrorCS", {"start": v(7.45, -5.94) * mm, "end": v(7.32, -5.91) * mm});
            skLineSegment(sketch, "E624.MirrorCS", {"start": v(5.06, -5.99) * mm, "end": v(5.37, -6.1) * mm});
            skLineSegment(sketch, "E625.MirrorCS", {"start": v(3.94, -4.06) * mm, "end": v(4.33, -4.08) * mm});
            skLineSegment(sketch, "E626.MirrorCS", {"start": v(6.5, -4.66) * mm, "end": v(6.7, -4.71) * mm});
            skLineSegment(sketch, "E627.MirrorCS", {"start": v(4.33, -4.08) * mm, "end": v(4.66, -4.13) * mm});
            skLineSegment(sketch, "E628.MirrorCS", {"start": v(6.2, -6.4) * mm, "end": v(6.68, -6.57) * mm});
            skLineSegment(sketch, "E629.MirrorCS", {"start": v(6.7, -4.71) * mm, "end": v(6.81, -4.75) * mm});
            skLineSegment(sketch, "E630.MirrorCS", {"start": v(10.48, -6.58) * mm, "end": v(10.69, -6.49) * mm});
            skLineSegment(sketch, "E631.MirrorCS", {"start": v(12.15, -4.3) * mm, "end": v(12.22, -4.13) * mm});
            skLineSegment(sketch, "E632.MirrorCS", {"start": v(12.52, -3.36) * mm, "end": v(12.61, -3.16) * mm});
            skLineSegment(sketch, "E633.MirrorCS", {"start": v(12.43, -3.58) * mm, "end": v(12.52, -3.36) * mm});
            skLineSegment(sketch, "E634.MirrorCS", {"start": v(12.4, -3.67) * mm, "end": v(12.43, -3.58) * mm});
            skLineSegment(sketch, "E635.MirrorCS", {"start": v(12.36, -3.74) * mm, "end": v(12.4, -3.67) * mm});
            skLineSegment(sketch, "E636.MirrorCS", {"start": v(6.95, -4.79) * mm, "end": v(7.09, -4.84) * mm});
            skLineSegment(sketch, "E637.MirrorCS", {"start": v(10.3, -6.65) * mm, "end": v(10.48, -6.58) * mm});
            skLineSegment(sketch, "E638.MirrorCS", {"start": v(2.68, -5.9) * mm, "end": v(2.93, -5.78) * mm});
            skLineSegment(sketch, "E639.MirrorCS", {"start": v(12.15, -1.72) * mm, "end": v(12.01, -1.8) * mm});
            skLineSegment(sketch, "E640.MirrorCS", {"start": v(4.87, -4.18) * mm, "end": v(5.1, -4.23) * mm});
            skLineSegment(sketch, "E641.MirrorCS", {"start": v(12.81, -2.79) * mm, "end": v(12.87, -2.68) * mm});
            skLineSegment(sketch, "E642.MirrorCS", {"start": v(11.71, -1.95) * mm, "end": v(11.8, -1.77) * mm});
            skLineSegment(sketch, "E643.MirrorCS", {"start": v(12.22, -4.13) * mm, "end": v(12.3, -3.9) * mm});
            skLineSegment(sketch, "E644.MirrorCS", {"start": v(5.37, -6.1) * mm, "end": v(5.75, -6.25) * mm});
            skLineSegment(sketch, "E645.MirrorCS", {"start": v(11.98, -4.76) * mm, "end": v(12.08, -4.5) * mm});
            skLineSegment(sketch, "E646.MirrorCS", {"start": v(2.45, -3.34) * mm, "end": v(2.3, -3.48) * mm});
            skLineSegment(sketch, "E647.MirrorCS", {"start": v(12.61, -3.16) * mm, "end": v(12.68, -3.03) * mm});
            skLineSegment(sketch, "E648.MirrorCS", {"start": v(4.66, -4.13) * mm, "end": v(4.87, -4.18) * mm});
            skLineSegment(sketch, "E649.MirrorCS", {"start": v(9.5, -6.83) * mm, "end": v(10, -6.74) * mm});
            skLineSegment(sketch, "E650.MirrorCS", {"start": v(12.01, -1.8) * mm, "end": v(11.72, -2) * mm});
            skLineSegment(sketch, "E651.MirrorCS", {"start": v(5.75, -6.25) * mm, "end": v(6.2, -6.4) * mm});
            skLineSegment(sketch, "E652.MirrorCS", {"start": v(8.51, -6.9) * mm, "end": v(9.24, -6.87) * mm});
            skLineSegment(sketch, "E653.MirrorCS", {"start": v(21.32, 10.58) * mm, "end": v(21.1, 10.34) * mm});
            skLineSegment(sketch, "E654.MirrorCS", {"start": v(20.35, 9.73) * mm, "end": v(20.42, 9.92) * mm});
            skLineSegment(sketch, "E655.MirrorCS", {"start": v(13.05, -1.27) * mm, "end": v(12.82, -1.36) * mm});
            skLineSegment(sketch, "E656.MirrorCS", {"start": v(12.82, -1.36) * mm, "end": v(12.58, -1.48) * mm});
            skLineSegment(sketch, "E657.MirrorCS", {"start": v(1.67, -6.73) * mm, "end": v(1.85, -6.52) * mm});
            skLineSegment(sketch, "E658.MirrorCS", {"start": v(11.92, -4.92) * mm, "end": v(11.98, -4.76) * mm});
            skLineSegment(sketch, "E659.MirrorCS", {"start": v(11.96, -1.43) * mm, "end": v(12.08, -1.18) * mm});
            skLineSegment(sketch, "E660.MirrorCS", {"start": v(1.16, -5.79) * mm, "end": v(0.87, -6.14) * mm});
            skLineSegment(sketch, "E661.MirrorCS", {"start": v(12.39, -1.59) * mm, "end": v(12.15, -1.72) * mm});
            skLineSegment(sketch, "E662.MirrorCS", {"start": v(12.08, -1.18) * mm, "end": v(12.24, -0.95) * mm});
            skLineSegment(sketch, "E663.MirrorCS", {"start": v(2.93, -5.78) * mm, "end": v(3.31, -5.66) * mm});
            skLineSegment(sketch, "E664.MirrorCS", {"start": v(12.58, -1.48) * mm, "end": v(12.39, -1.59) * mm});
            skLineSegment(sketch, "E665.MirrorCS", {"start": v(10, -6.74) * mm, "end": v(10.3, -6.65) * mm});
            skLineSegment(sketch, "E666.MirrorCS", {"start": v(20.61, 9.83) * mm, "end": v(20.48, 9.7) * mm});
            skLineSegment(sketch, "E667.MirrorCS", {"start": v(9.24, -6.87) * mm, "end": v(9.5, -6.83) * mm});
            skLineSegment(sketch, "E668.MirrorCS", {"start": v(22.26, 11.89) * mm, "end": v(22.27, 12.1) * mm});
            skLineSegment(sketch, "E669.MirrorCS", {"start": v(22.27, 12.1) * mm, "end": v(22.19, 12) * mm});
            skLineSegment(sketch, "E670.MirrorCS", {"start": v(2.17, -6.23) * mm, "end": v(2.28, -6.16) * mm});
            skLineSegment(sketch, "E671.MirrorCS", {"start": v(12.87, -2.68) * mm, "end": v(13, -2.49) * mm});
            skLineSegment(sketch, "E672.MirrorCS", {"start": v(11.8, -1.77) * mm, "end": v(11.96, -1.43) * mm});
            skLineSegment(sketch, "E673.MirrorCS", {"start": v(11.49, -5.82) * mm, "end": v(11.55, -5.72) * mm});
            skLineSegment(sketch, "E674.MirrorCS", {"start": v(4.3, -13.36) * mm, "end": v(4.45, -13.23) * mm});
            skLineSegment(sketch, "E675.MirrorCS", {"start": v(2.05, -6.33) * mm, "end": v(2.17, -6.23) * mm});
            skLineSegment(sketch, "E676.MirrorCS", {"start": v(4.23, -13.38) * mm, "end": v(4.3, -13.36) * mm});
            skLineSegment(sketch, "E677.MirrorCS", {"start": v(21.94, 11.6) * mm, "end": v(21.65, 11.12) * mm});
            skLineSegment(sketch, "E678.MirrorCS", {"start": v(20.89, 10.12) * mm, "end": v(20.61, 9.83) * mm});
            skLineSegment(sketch, "E679.MirrorCS", {"start": v(21.76, 9.75) * mm, "end": v(21.98, 10.56) * mm});
            skLineSegment(sketch, "E680.MirrorCS", {"start": v(4.17, -13.36) * mm, "end": v(4.23, -13.38) * mm});
            skLineSegment(sketch, "E681.MirrorCS", {"start": v(20.5, 10.17) * mm, "end": v(20.84, 11.16) * mm});
            skLineSegment(sketch, "E682.MirrorCS", {"start": v(22.15, 11.32) * mm, "end": v(22.26, 11.89) * mm});
            skLineSegment(sketch, "E683.MirrorCS", {"start": v(1.35, -8.12) * mm, "end": v(1.27, -7.98) * mm});
            skLineSegment(sketch, "E684.MirrorCS", {"start": v(20.42, 9.92) * mm, "end": v(20.5, 10.17) * mm});
            skLineSegment(sketch, "E685.MirrorCS", {"start": v(21.44, 10.74) * mm, "end": v(21.32, 10.58) * mm});
            skLineSegment(sketch, "E686.MirrorCS", {"start": v(2.28, -6.16) * mm, "end": v(2.4, -6.07) * mm});
            skLineSegment(sketch, "E687.MirrorCS", {"start": v(4.6, -13.07) * mm, "end": v(4.84, -12.72) * mm});
            skLineSegment(sketch, "E688.MirrorCS", {"start": v(12.47, -0.64) * mm, "end": v(12.62, -0.48) * mm});
            skLineSegment(sketch, "E689.MirrorCS", {"start": v(20.84, 11.16) * mm, "end": v(20.98, 11.67) * mm});
            skLineSegment(sketch, "E690.MirrorCS", {"start": v(21.98, 10.56) * mm, "end": v(22.15, 11.32) * mm});
            skLineSegment(sketch, "E691.MirrorCS", {"start": v(18.9, 4.23) * mm, "end": v(18.65, 4.14) * mm});
            skLineSegment(sketch, "E692.MirrorCS", {"start": v(21.65, 11.12) * mm, "end": v(21.51, 10.89) * mm});
            skLineSegment(sketch, "E693.MirrorCS", {"start": v(20.3, 9.5) * mm, "end": v(20.35, 9.73) * mm});
            skLineSegment(sketch, "E694.MirrorCS", {"start": v(22.04, 11.77) * mm, "end": v(21.94, 11.6) * mm});
            skLineSegment(sketch, "E695.MirrorCS", {"start": v(10.69, -6.49) * mm, "end": v(11, -6.3) * mm});
            skLineSegment(sketch, "E696.MirrorCS", {"start": v(4.45, -13.23) * mm, "end": v(4.6, -13.07) * mm});
            skLineSegment(sketch, "E697.MirrorCS", {"start": v(21.1, 10.34) * mm, "end": v(20.89, 10.12) * mm});
            skLineSegment(sketch, "E698.MirrorCS", {"start": v(0.72, -6.36) * mm, "end": v(0.61, -6.5) * mm});
            skLineSegment(sketch, "E699.MirrorCS", {"start": v(21.51, 10.89) * mm, "end": v(21.44, 10.74) * mm});
            skLineSegment(sketch, "E700.MirrorCS", {"start": v(1.85, -6.52) * mm, "end": v(2.05, -6.33) * mm});
            skLineSegment(sketch, "E701.MirrorCS", {"start": v(13.4, -1.18) * mm, "end": v(13.05, -1.27) * mm});
            skLineSegment(sketch, "E702.MirrorCS", {"start": v(0.87, -6.14) * mm, "end": v(0.72, -6.36) * mm});
            skLineSegment(sketch, "E703.MirrorCS", {"start": v(20.48, 9.7) * mm, "end": v(20.3, 9.5) * mm});
            skLineSegment(sketch, "E704.MirrorCS", {"start": v(20.65, 5.6) * mm, "end": v(20.48, 5.33) * mm});
            skLineSegment(sketch, "E705.MirrorCS", {"start": v(7.26, -4.89) * mm, "end": v(7.52, -4.97) * mm});
            skLineSegment(sketch, "E706.MirrorCS", {"start": v(22.19, 12) * mm, "end": v(22.04, 11.77) * mm});
            skLineSegment(sketch, "E707.MirrorCS", {"start": v(1.35, -7.2) * mm, "end": v(1.48, -6.99) * mm});
            skLineSegment(sketch, "E708.MirrorCS", {"start": v(13, -2.49) * mm, "end": v(13.42, -1.96) * mm});
            skLineSegment(sketch, "E709.MirrorCS", {"start": v(20.42, 3.82) * mm, "end": v(20.65, 4.43) * mm});
            skLineSegment(sketch, "E710.MirrorCS", {"start": v(12.76, -0.35) * mm, "end": v(12.89, -0.25) * mm});
            skLineSegment(sketch, "E711.MirrorCS", {"start": v(20.03, 3.06) * mm, "end": v(20.16, 3.3) * mm});
            skLineSegment(sketch, "E712.MirrorCS", {"start": v(20.65, 4.43) * mm, "end": v(20.8, 5.02) * mm});
            skLineSegment(sketch, "E713.MirrorCS", {"start": v(20.8, 5.83) * mm, "end": v(20.65, 5.6) * mm});
            skLineSegment(sketch, "E714.MirrorCS", {"start": v(7.2, -6.72) * mm, "end": v(7.86, -6.85) * mm});
            skLineSegment(sketch, "E715.MirrorCS", {"start": v(19.68, 4.63) * mm, "end": v(19.31, 4.42) * mm});
            skLineSegment(sketch, "E716.MirrorCS", {"start": v(12.62, -0.48) * mm, "end": v(12.76, -0.35) * mm});
            skLineSegment(sketch, "E717.MirrorCS", {"start": v(20.24, 5.08) * mm, "end": v(20.04, 4.91) * mm});
            skLineSegment(sketch, "E718.MirrorCS", {"start": v(6.8, -6.6) * mm, "end": v(7.2, -6.72) * mm});
            skLineSegment(sketch, "E719.MirrorCS", {"start": v(20.8, 5.02) * mm, "end": v(20.91, 5.51) * mm});
            skLineSegment(sketch, "E720.MirrorCS", {"start": v(20.9, 6.08) * mm, "end": v(20.8, 5.83) * mm});
            skLineSegment(sketch, "E721.MirrorCS", {"start": v(20.04, 4.91) * mm, "end": v(19.68, 4.63) * mm});
            skLineSegment(sketch, "E722.MirrorCS", {"start": v(19.33, 5.72) * mm, "end": v(19.6, 6) * mm});
            skLineSegment(sketch, "E723.MirrorCS", {"start": v(19.31, 4.42) * mm, "end": v(18.9, 4.23) * mm});
            skLineSegment(sketch, "E724.MirrorCS", {"start": v(12.24, -0.95) * mm, "end": v(12.47, -0.64) * mm});
            skLineSegment(sketch, "E725.MirrorCS", {"start": v(19.6, 6) * mm, "end": v(19.78, 6.2) * mm});
            skLineSegment(sketch, "E726.MirrorCS", {"start": v(1.24, -7.5) * mm, "end": v(1.35, -7.2) * mm});
            skLineSegment(sketch, "E727.MirrorCS", {"start": v(5.1, -12.31) * mm, "end": v(5, -12.28) * mm});
            skLineSegment(sketch, "E728.MirrorCS", {"start": v(18.95, 5.38) * mm, "end": v(19.33, 5.72) * mm});
            skLineSegment(sketch, "E729.MirrorCS", {"start": v(1.48, -6.99) * mm, "end": v(1.67, -6.73) * mm});
            skLineSegment(sketch, "E730.MirrorCS", {"start": v(1.24, -7.9) * mm, "end": v(1.24, -7.5) * mm});
            skLineSegment(sketch, "E731.MirrorCS", {"start": v(0.61, -6.5) * mm, "end": v(0.5, -6.7) * mm});
            skLineSegment(sketch, "E732.MirrorCS", {"start": v(-0.48, -15.24) * mm, "end": v(-0.27, -15.24) * mm});
            skLineSegment(sketch, "E733.MirrorCS", {"start": v(13.62, -1.13) * mm, "end": v(13.4, -1.18) * mm});
            skLineSegment(sketch, "E734.MirrorCS", {"start": v(1.27, -7.98) * mm, "end": v(1.24, -7.9) * mm});
            skLineSegment(sketch, "E735.MirrorCS", {"start": v(20.48, 5.33) * mm, "end": v(20.24, 5.08) * mm});
            skLineSegment(sketch, "E736.MirrorCS", {"start": v(7.86, -6.85) * mm, "end": v(8.51, -6.9) * mm});
            skLineSegment(sketch, "E737.MirrorCS", {"start": v(12.89, -0.25) * mm, "end": v(13.24, 0.02) * mm});
            skLineSegment(sketch, "E738.MirrorCS", {"start": v(13.24, 0.02) * mm, "end": v(13.5, 0.19) * mm});
            skLineSegment(sketch, "E739.MirrorCS", {"start": v(5.1, -12.34) * mm, "end": v(5.1, -12.31) * mm});
            skLineSegment(sketch, "E740.MirrorCS", {"start": v(-0.07, -15.2) * mm, "end": v(0.18, -15.12) * mm});
            skLineSegment(sketch, "E741.MirrorCS", {"start": v(1.44, -8.2) * mm, "end": v(1.35, -8.12) * mm});
            skLineSegment(sketch, "E742.MirrorCS", {"start": v(6.72, 5.28) * mm, "end": v(6.41, 4.74) * mm});
            skLineSegment(sketch, "E743.MirrorCS", {"start": v(21.63, 9.34) * mm, "end": v(21.76, 9.75) * mm});
            skLineSegment(sketch, "E744.MirrorCS", {"start": v(2.16, -8.21) * mm, "end": v(1.56, -8.2) * mm});
            skLineSegment(sketch, "E745.MirrorCS", {"start": v(17.8, 4.46) * mm, "end": v(18.16, 4.72) * mm});
            skLineSegment(sketch, "E746.MirrorCS", {"start": v(18.02, 3.93) * mm, "end": v(17.43, 3.8) * mm});
            skLineSegment(sketch, "E747.MirrorCS", {"start": v(20.91, 5.51) * mm, "end": v(21.19, 6.74) * mm});
            skLineSegment(sketch, "E748.MirrorCS", {"start": v(18.16, 4.72) * mm, "end": v(18.47, 4.97) * mm});
            skLineSegment(sketch, "E749.MirrorCS", {"start": v(4.84, -12.72) * mm, "end": v(5.1, -12.34) * mm});
            skLineSegment(sketch, "E750.MirrorCS", {"start": v(7.27, 6.1) * mm, "end": v(7.08, 5.84) * mm});
            skLineSegment(sketch, "E751.MirrorCS", {"start": v(21.1, 6.5) * mm, "end": v(20.9, 6.08) * mm});
            skLineSegment(sketch, "E752.MirrorCS", {"start": v(6.33, 3.78) * mm, "end": v(6.85, 4.25) * mm});
            skLineSegment(sketch, "E753.MirrorCS", {"start": v(19.04, 2.05) * mm, "end": v(19.29, 2.24) * mm});
            skLineSegment(sketch, "E754.MirrorCS", {"start": v(18.47, 4.97) * mm, "end": v(18.95, 5.38) * mm});
            skLineSegment(sketch, "E755.MirrorCS", {"start": v(6.41, 4.74) * mm, "end": v(6.13, 4.1) * mm});
            skLineSegment(sketch, "E756.MirrorCS", {"start": v(6.13, 4.1) * mm, "end": v(5.89, 3.5) * mm});
            skLineSegment(sketch, "E757.MirrorCS", {"start": v(19.29, 2.24) * mm, "end": v(19.62, 2.52) * mm});
            skLineSegment(sketch, "E758.MirrorCS", {"start": v(1.56, -8.2) * mm, "end": v(1.44, -8.2) * mm});
            skLineSegment(sketch, "E759.MirrorCS", {"start": v(19.86, 2.8) * mm, "end": v(20.03, 3.06) * mm});
            skLineSegment(sketch, "E760.MirrorCS", {"start": v(18.92, 10.44) * mm, "end": v(18.6, 10.1) * mm});
            skLineSegment(sketch, "E761.MirrorCS", {"start": v(19.62, 2.52) * mm, "end": v(19.86, 2.8) * mm});
            skLineSegment(sketch, "E762.MirrorCS", {"start": v(7.66, 6.55) * mm, "end": v(7.27, 6.1) * mm});
            skLineSegment(sketch, "E763.MirrorCS", {"start": v(0.5, -6.7) * mm, "end": v(0.27, -6.99) * mm});
            skLineSegment(sketch, "E764.MirrorCS", {"start": v(5.95, 3.33) * mm, "end": v(6.33, 3.78) * mm});
            skLineSegment(sketch, "E765.MirrorCS", {"start": v(18.6, 10.1) * mm, "end": v(18.32, 9.86) * mm});
            skLineSegment(sketch, "E766.MirrorCS", {"start": v(-0.27, -15.24) * mm, "end": v(-0.07, -15.2) * mm});
            skLineSegment(sketch, "E767.MirrorCS", {"start": v(18.32, 9.86) * mm, "end": v(17.95, 9.59) * mm});
            skLineSegment(sketch, "E768.MirrorCS", {"start": v(19.15, 10.74) * mm, "end": v(18.92, 10.44) * mm});
            skLineSegment(sketch, "E769.MirrorCS", {"start": v(7.08, 5.84) * mm, "end": v(6.9, 5.58) * mm});
            skLineSegment(sketch, "E770.MirrorCS", {"start": v(6.87, -7.14) * mm, "end": v(6.32, -7.37) * mm});
            skLineSegment(sketch, "E771.MirrorCS", {"start": v(18.65, 4.14) * mm, "end": v(18.02, 3.93) * mm});
            skLineSegment(sketch, "E772.MirrorCS", {"start": v(0.27, -6.99) * mm, "end": v(0.02, -7.33) * mm});
            skLineSegment(sketch, "E773.MirrorCS", {"start": v(6.9, 5.58) * mm, "end": v(6.72, 5.28) * mm});
            skLineSegment(sketch, "E774.MirrorCS", {"start": v(2.31, -10.87) * mm, "end": v(1.98, -10.63) * mm});
            skLineSegment(sketch, "E775.MirrorCS", {"start": v(20.16, 3.3) * mm, "end": v(20.42, 3.82) * mm});
            skLineSegment(sketch, "E776.MirrorCS", {"start": v(3.2, -11.41) * mm, "end": v(2.31, -10.87) * mm});
            skLineSegment(sketch, "E777.MirrorCS", {"start": v(1.5, -14.74) * mm, "end": v(1.72, -14.74) * mm});
            skLineSegment(sketch, "E778.MirrorCS", {"start": v(0.02, -7.33) * mm, "end": v(-0.24, -7.63) * mm});
            skLineSegment(sketch, "E779.MirrorCS", {"start": v(5.57, -11.64) * mm, "end": v(6, -10.1) * mm});
            skLineSegment(sketch, "E780.MirrorCS", {"start": v(11.32, 3.56) * mm, "end": v(11.42, 4.19) * mm});
            skLineSegment(sketch, "E781.MirrorCS", {"start": v(16.93, 6.2) * mm, "end": v(16.43, 6.01) * mm});
            skLineSegment(sketch, "E782.MirrorCS", {"start": v(4.76, -11.44) * mm, "end": v(5.57, -11.64) * mm});
            skLineSegment(sketch, "E783.MirrorCS", {"start": v(20.85, 17.04) * mm, "end": v(20.71, 17.54) * mm});
            skLineSegment(sketch, "E784.MirrorCS", {"start": v(1.98, -10.63) * mm, "end": v(2.6, -10.87) * mm});
            skLineSegment(sketch, "E785.MirrorCS", {"start": v(5, -12.28) * mm, "end": v(3.77, -11.7) * mm});
            skLineSegment(sketch, "E786.MirrorCS", {"start": v(3.19, -2.74) * mm, "end": v(2.75, -3.09) * mm});
            skLineSegment(sketch, "E787.MirrorCS", {"start": v(19.78, 6.2) * mm, "end": v(20.43, 6.98) * mm});
            skLineSegment(sketch, "E788.MirrorCS", {"start": v(2.75, -3.09) * mm, "end": v(2.45, -3.34) * mm});
            skLineSegment(sketch, "E789.MirrorCS", {"start": v(17.45, 6.43) * mm, "end": v(16.93, 6.2) * mm});
            skLineSegment(sketch, "E790.MirrorCS", {"start": v(9.3, 4.7) * mm, "end": v(9.54, 4.48) * mm});
            skLineSegment(sketch, "E791.MirrorCS", {"start": v(16.56, 3.61) * mm, "end": v(17.06, 3.95) * mm});
            skLineSegment(sketch, "E792.MirrorCS", {"start": v(21.32, 14.63) * mm, "end": v(21.22, 15.47) * mm});
            skLineSegment(sketch, "E793.MirrorCS", {"start": v(11.42, 4.19) * mm, "end": v(11.57, 4.86) * mm});
            skLineSegment(sketch, "E794.MirrorCS", {"start": v(3.98, -11.25) * mm, "end": v(4.76, -11.44) * mm});
            skLineSegment(sketch, "E795.MirrorCS", {"start": v(9.88, 3.89) * mm, "end": v(9.97, 3.46) * mm});
            skLineSegment(sketch, "E796.MirrorCS", {"start": v(9.75, 4.24) * mm, "end": v(9.88, 3.89) * mm});
            skLineSegment(sketch, "E797.MirrorCS", {"start": v(11.87, 4.12) * mm, "end": v(11.6, 3.83) * mm});
            skLineSegment(sketch, "E798.MirrorCS", {"start": v(-0.24, -7.63) * mm, "end": v(-0.48, -7.87) * mm});
            skLineSegment(sketch, "E799.MirrorCS", {"start": v(20.64, 16.52) * mm, "end": v(20.58, 15.72) * mm});
            skLineSegment(sketch, "E800.MirrorCS", {"start": v(12.3, 4.46) * mm, "end": v(11.87, 4.12) * mm});
            skLineSegment(sketch, "E801.MirrorCS", {"start": v(6.85, 4.25) * mm, "end": v(7.52, 4.62) * mm});
            skLineSegment(sketch, "E802.MirrorCS", {"start": v(5.43, -9.99) * mm, "end": v(4.65, -9.85) * mm});
            skLineSegment(sketch, "E803.MirrorCS", {"start": v(9.54, 4.48) * mm, "end": v(9.75, 4.24) * mm});
            skLineSegment(sketch, "E804.MirrorCS", {"start": v(20.58, 15.72) * mm, "end": v(20.45, 14.57) * mm});
            skLineSegment(sketch, "E805.MirrorCS", {"start": v(18.03, 6.76) * mm, "end": v(17.45, 6.43) * mm});
            skLineSegment(sketch, "E806.MirrorCS", {"start": v(3.23, -11.05) * mm, "end": v(3.98, -11.25) * mm});
            skLineSegment(sketch, "E807.MirrorCS", {"start": v(8.62, 4.84) * mm, "end": v(9.3, 4.7) * mm});
            skLineSegment(sketch, "E808.MirrorCS", {"start": v(13.36, 5.05) * mm, "end": v(12.91, 4.83) * mm});
            skLineSegment(sketch, "E809.MirrorCS", {"start": v(0.18, -15.12) * mm, "end": v(0.96, -14.9) * mm});
            skLineSegment(sketch, "E810.MirrorCS", {"start": v(11.6, 3.83) * mm, "end": v(11.32, 3.56) * mm});
            skLineSegment(sketch, "E811.MirrorCS", {"start": v(17.43, 3.8) * mm, "end": v(16.56, 3.61) * mm});
            skLineSegment(sketch, "E812.MirrorCS", {"start": v(20.98, 11.67) * mm, "end": v(21.25, 13.07) * mm});
            skLineSegment(sketch, "E813.MirrorCS", {"start": v(12.91, 4.83) * mm, "end": v(12.6, 4.65) * mm});
            skLineSegment(sketch, "E814.MirrorCS", {"start": v(21.22, 15.47) * mm, "end": v(21.01, 16.42) * mm});
            skLineSegment(sketch, "E815.MirrorCS", {"start": v(6, -10.1) * mm, "end": v(5.43, -9.99) * mm});
            skLineSegment(sketch, "E816.MirrorCS", {"start": v(12.6, 4.65) * mm, "end": v(12.3, 4.46) * mm});
            skLineSegment(sketch, "E817.MirrorCS", {"start": v(8.3, 4.84) * mm, "end": v(8.62, 4.84) * mm});
            skLineSegment(sketch, "E818.MirrorCS", {"start": v(11.57, 4.86) * mm, "end": v(11.75, 5.43) * mm});
            skLineSegment(sketch, "E819.MirrorCS", {"start": v(21.25, 13.07) * mm, "end": v(21.32, 13.81) * mm});
            skLineSegment(sketch, "E820.MirrorCS", {"start": v(9.97, 3.18) * mm, "end": v(9.9, 2.63) * mm});
            skLineSegment(sketch, "E821.MirrorCS", {"start": v(7.52, 4.62) * mm, "end": v(8.3, 4.84) * mm});
            skLineSegment(sketch, "E822.MirrorCS", {"start": v(9.9, 2.63) * mm, "end": v(9.75, 2.18) * mm});
            skLineSegment(sketch, "E823.MirrorCS", {"start": v(21.14, 8.18) * mm, "end": v(21.49, 8.94) * mm});
            skLineSegment(sketch, "E824.MirrorCS", {"start": v(20, 12.52) * mm, "end": v(19.83, 12.03) * mm});
            skLineSegment(sketch, "E825.MirrorCS", {"start": v(17.06, 3.95) * mm, "end": v(17.38, 4.17) * mm});
            skLineSegment(sketch, "E826.MirrorCS", {"start": v(9.97, 3.46) * mm, "end": v(9.97, 3.18) * mm});
            skLineSegment(sketch, "E827.MirrorCS", {"start": v(21.19, 6.74) * mm, "end": v(21.1, 6.5) * mm});
            skLineSegment(sketch, "E828.MirrorCS", {"start": v(20.7, 17.26) * mm, "end": v(20.64, 16.52) * mm});
            skLineSegment(sketch, "E829.MirrorCS", {"start": v(21.32, 13.81) * mm, "end": v(21.32, 14.63) * mm});
            skLineSegment(sketch, "E830.MirrorCS", {"start": v(21.01, 16.42) * mm, "end": v(20.85, 17.04) * mm});
            skLineSegment(sketch, "E831.MirrorCS", {"start": v(5.64, 2.87) * mm, "end": v(5.95, 3.33) * mm});
            skLineSegment(sketch, "E832.MirrorCS", {"start": v(20.43, 6.98) * mm, "end": v(20.92, 7.75) * mm});
            skLineSegment(sketch, "E833.MirrorCS", {"start": v(20.25, 13.39) * mm, "end": v(20, 12.52) * mm});
            skLineSegment(sketch, "E834.MirrorCS", {"start": v(3.77, -11.7) * mm, "end": v(3.2, -11.41) * mm});
            skLineSegment(sketch, "E835.MirrorCS", {"start": v(2.6, -10.87) * mm, "end": v(3.23, -11.05) * mm});
            skLineSegment(sketch, "E836.MirrorCS", {"start": v(17.38, 4.17) * mm, "end": v(17.8, 4.46) * mm});
            skLineSegment(sketch, "E837.MirrorCS", {"start": v(15.85, 5.83) * mm, "end": v(15.25, 5.66) * mm});
            skLineSegment(sketch, "E838.MirrorCS", {"start": v(20.92, 7.75) * mm, "end": v(21.14, 8.18) * mm});
            skLineSegment(sketch, "E839.MirrorCS", {"start": v(16.43, 6.01) * mm, "end": v(15.85, 5.83) * mm});
            skLineSegment(sketch, "E840.MirrorCS", {"start": v(11.75, 5.43) * mm, "end": v(11.98, 5.97) * mm});
            skLineSegment(sketch, "E841.MirrorCS", {"start": v(5.5, -7.67) * mm, "end": v(4.4, -7.91) * mm});
            skLineSegment(sketch, "E842.MirrorCS", {"start": v(2.96, -9.55) * mm, "end": v(6.43, -9.41) * mm});
            skLineSegment(sketch, "E843.MirrorCS", {"start": v(9.53, 1.53) * mm, "end": v(9.25, 1.03) * mm});
            skLineSegment(sketch, "E844.MirrorCS", {"start": v(3.59, -2.46) * mm, "end": v(3.19, -2.74) * mm});
            skLineSegment(sketch, "E845.MirrorCS", {"start": v(18.93, 7.6) * mm, "end": v(18.48, 7.17) * mm});
            skLineSegment(sketch, "E846.MirrorCS", {"start": v(5.77, -1.37) * mm, "end": v(5.31, -1.55) * mm});
            skLineSegment(sketch, "E847.MirrorCS", {"start": v(12.15, 8.76) * mm, "end": v(11.22, 8.57) * mm});
            skLineSegment(sketch, "E848.MirrorCS", {"start": v(20.45, 14.57) * mm, "end": v(20.25, 13.39) * mm});
            skLineSegment(sketch, "E849.MirrorCS", {"start": v(4.15, -9.76) * mm, "end": v(2.96, -9.55) * mm});
            skLineSegment(sketch, "E850.MirrorCS", {"start": v(6.43, -9.41) * mm, "end": v(6.87, -7.14) * mm});
            skLineSegment(sketch, "E851.MirrorCS", {"start": v(8.58, 7.38) * mm, "end": v(8.23, 7.08) * mm});
            skLineSegment(sketch, "E852.MirrorCS", {"start": v(18.8, 1.9) * mm, "end": v(19.04, 2.05) * mm});
            skLineSegment(sketch, "E853.MirrorCS", {"start": v(19.27, 8.1) * mm, "end": v(18.93, 7.6) * mm});
            skLineSegment(sketch, "E854.MirrorCS", {"start": v(4.44, -1.98) * mm, "end": v(4.05, -2.2) * mm});
            skLineSegment(sketch, "E855.MirrorCS", {"start": v(5.89, 3.5) * mm, "end": v(5.64, 2.87) * mm});
            skLineSegment(sketch, "E856.MirrorCS", {"start": v(13.06, 6.8) * mm, "end": v(13.92, 6.99) * mm});
            skLineSegment(sketch, "E857.MirrorCS", {"start": v(18.44, 1.71) * mm, "end": v(18.8, 1.9) * mm});
            skLineSegment(sketch, "E858.MirrorCS", {"start": v(15.81, 8.93) * mm, "end": v(14.36, 8.86) * mm});
            skLineSegment(sketch, "E859.MirrorCS", {"start": v(8.23, 7.08) * mm, "end": v(7.66, 6.55) * mm});
            skLineSegment(sketch, "E860.MirrorCS", {"start": v(14.45, -1.04) * mm, "end": v(14.43, -1.03) * mm});
            skLineSegment(sketch, "E861.MirrorCS", {"start": v(17.18, 1.27) * mm, "end": v(17.77, 1.45) * mm});
            skLineSegment(sketch, "E862.MirrorCS", {"start": v(2.22, -14.6) * mm, "end": v(2.67, -14.37) * mm});
            skLineSegment(sketch, "E863.MirrorCS", {"start": v(13.97, 5.29) * mm, "end": v(13.36, 5.05) * mm});
            skLineSegment(sketch, "E864.MirrorCS", {"start": v(3.16, -8.14) * mm, "end": v(2.73, -8.19) * mm});
            skLineSegment(sketch, "E865.MirrorCS", {"start": v(4.82, -1.8) * mm, "end": v(4.44, -1.98) * mm});
            skLineSegment(sketch, "E866.MirrorCS", {"start": v(19.45, 11.23) * mm, "end": v(19.15, 10.74) * mm});
            skLineSegment(sketch, "E867.MirrorCS", {"start": v(17.95, 9.59) * mm, "end": v(17.24, 9.25) * mm});
            skLineSegment(sketch, "E868.MirrorCS", {"start": v(14.36, 8.86) * mm, "end": v(12.97, 8.83) * mm});
            skLineSegment(sketch, "E869.MirrorCS", {"start": v(17.24, 9.25) * mm, "end": v(16.5, 9.02) * mm});
            skLineSegment(sketch, "E870.MirrorCS", {"start": v(11.98, 5.97) * mm, "end": v(12.45, 6.47) * mm});
            skLineSegment(sketch, "E871.MirrorCS", {"start": v(8.49, 0.05) * mm, "end": v(7.9, -0.41) * mm});
            skLineSegment(sketch, "E872.MirrorCS", {"start": v(9.75, 2.18) * mm, "end": v(9.53, 1.53) * mm});
            skLineSegment(sketch, "E873.MirrorCS", {"start": v(6.32, -7.37) * mm, "end": v(5.5, -7.67) * mm});
            skLineSegment(sketch, "E874.MirrorCS", {"start": v(18.48, 7.17) * mm, "end": v(18.03, 6.76) * mm});
            skLineSegment(sketch, "E875.MirrorCS", {"start": v(19.83, 12.03) * mm, "end": v(19.69, 11.7) * mm});
            skLineSegment(sketch, "E876.MirrorCS", {"start": v(20.71, 17.54) * mm, "end": v(20.7, 17.26) * mm});
            skLineSegment(sketch, "E877.MirrorCS", {"start": v(13.42, -1.96) * mm, "end": v(14.45, -1.04) * mm});
            skLineSegment(sketch, "E878.MirrorCS", {"start": v(1.72, -14.74) * mm, "end": v(2.22, -14.6) * mm});
            skLineSegment(sketch, "E879.MirrorCS", {"start": v(10.47, 8.35) * mm, "end": v(10.05, 8.2) * mm});
            skLineSegment(sketch, "E880.MirrorCS", {"start": v(2.73, -8.19) * mm, "end": v(2.16, -8.21) * mm});
            skLineSegment(sketch, "E881.MirrorCS", {"start": v(12.45, 6.47) * mm, "end": v(13.06, 6.8) * mm});
            skLineSegment(sketch, "E882.MirrorCS", {"start": v(14, -1.06) * mm, "end": v(13.62, -1.13) * mm});
            skLineSegment(sketch, "E883.MirrorCS", {"start": v(7.9, -0.41) * mm, "end": v(7.16, -0.78) * mm});
            skLineSegment(sketch, "E884.MirrorCS", {"start": v(13.92, 6.99) * mm, "end": v(15.07, 7.12) * mm});
            skLineSegment(sketch, "E885.MirrorCS", {"start": v(14.43, -1.03) * mm, "end": v(14, -1.06) * mm});
            skLineSegment(sketch, "E886.MirrorCS", {"start": v(11.22, 8.57) * mm, "end": v(10.47, 8.35) * mm});
            skLineSegment(sketch, "E887.MirrorCS", {"start": v(12.97, 8.83) * mm, "end": v(12.15, 8.76) * mm});
            skLineSegment(sketch, "E888.MirrorCS", {"start": v(15.07, 7.12) * mm, "end": v(16.72, 7.35) * mm});
            skLineSegment(sketch, "E889.MirrorCS", {"start": v(16.54, 1.11) * mm, "end": v(17.18, 1.27) * mm});
            skLineSegment(sketch, "E890.MirrorCS", {"start": v(6.5, -1.05) * mm, "end": v(5.77, -1.37) * mm});
            skLineSegment(sketch, "E891.MirrorCS", {"start": v(15.25, 5.66) * mm, "end": v(14.66, 5.5) * mm});
            skLineSegment(sketch, "E892.MirrorCS", {"start": v(10.05, 8.2) * mm, "end": v(9.64, 8) * mm});
            skLineSegment(sketch, "E893.MirrorCS", {"start": v(4.4, -7.91) * mm, "end": v(3.8, -8.04) * mm});
            skLineSegment(sketch, "E894.MirrorCS", {"start": v(13.96, 0.4) * mm, "end": v(14.54, 0.63) * mm});
            skLineSegment(sketch, "E895.MirrorCS", {"start": v(4.05, -2.2) * mm, "end": v(3.59, -2.46) * mm});
            skLineSegment(sketch, "E896.MirrorCS", {"start": v(21.49, 8.94) * mm, "end": v(21.63, 9.34) * mm});
            skLineSegment(sketch, "E897.MirrorCS", {"start": v(7.16, -0.78) * mm, "end": v(6.5, -1.05) * mm});
            skLineSegment(sketch, "E898.MirrorCS", {"start": v(13.5, 0.19) * mm, "end": v(13.96, 0.4) * mm});
            skLineSegment(sketch, "E899.MirrorCS", {"start": v(5.31, -1.55) * mm, "end": v(4.82, -1.8) * mm});
            skLineSegment(sketch, "E900.MirrorCS", {"start": v(16.72, 7.35) * mm, "end": v(17.97, 7.6) * mm});
            skLineSegment(sketch, "E901.MirrorCS", {"start": v(1.96, -12.4) * mm, "end": v(4.17, -13.36) * mm});
            skLineSegment(sketch, "E902.MirrorCS", {"start": v(9.64, 8) * mm, "end": v(9.16, 7.73) * mm});
            skLineSegment(sketch, "E903.MirrorCS", {"start": v(14.66, 5.5) * mm, "end": v(13.97, 5.29) * mm});
            skLineSegment(sketch, "E904.MirrorCS", {"start": v(8.96, 0.57) * mm, "end": v(8.49, 0.05) * mm});
            skLineSegment(sketch, "E905.MirrorCS", {"start": v(17.97, 7.6) * mm, "end": v(19.27, 8.1) * mm});
            skLineSegment(sketch, "E906.MirrorCS", {"start": v(4.65, -9.85) * mm, "end": v(4.15, -9.76) * mm});
            skLineSegment(sketch, "E907.MirrorCS", {"start": v(9.16, 7.73) * mm, "end": v(8.58, 7.38) * mm});
            skLineSegment(sketch, "E908.MirrorCS", {"start": v(15.1, 0.78) * mm, "end": v(16.06, 0.99) * mm});
            skLineSegment(sketch, "E909.MirrorCS", {"start": v(16.5, 9.02) * mm, "end": v(15.81, 8.93) * mm});
            skLineSegment(sketch, "E910.MirrorCS", {"start": v(3.8, -8.04) * mm, "end": v(3.16, -8.14) * mm});
            skLineSegment(sketch, "E911.MirrorCS", {"start": v(17.77, 1.45) * mm, "end": v(18.44, 1.71) * mm});
            skLineSegment(sketch, "E912.MirrorCS", {"start": v(14.54, 0.63) * mm, "end": v(15.1, 0.78) * mm});
            skLineSegment(sketch, "E913.MirrorCS", {"start": v(19.69, 11.7) * mm, "end": v(19.45, 11.23) * mm});
            skLineSegment(sketch, "E914.MirrorCS", {"start": v(16.06, 0.99) * mm, "end": v(16.54, 1.11) * mm});
            skLineSegment(sketch, "E915.MirrorCS", {"start": v(9.25, 1.03) * mm, "end": v(8.96, 0.57) * mm});
            skLineSegment(sketch, "E916.MirrorCS", {"start": v(3.57, -13.83) * mm, "end": v(1.96, -12.4) * mm});
            skLineSegment(sketch, "E917.MirrorCS", {"start": v(2.67, -14.37) * mm, "end": v(3.57, -13.83) * mm});
            skLineSegment(sketch, "E918.MirrorCS", {"start": v(0.55, -13.24) * mm, "end": v(1.5, -14.74) * mm});
            skLineSegment(sketch, "E919.MirrorCS", {"start": v(0.96, -14.9) * mm, "end": v(0.55, -13.24) * mm});
            skLineSegment(sketch, "E920", {"start": v(-6.62, 3.88) * mm, "end": v(-6.74, 4.72) * mm});
            skLineSegment(sketch, "E921", {"start": v(-6.74, 4.72) * mm, "end": v(-6.96, 5.39) * mm});
            skLineSegment(sketch, "E922", {"start": v(-6.96, 5.39) * mm, "end": v(-7.3, 6.02) * mm});
            skLineSegment(sketch, "E923", {"start": v(-7.3, 6.02) * mm, "end": v(-7.6, 6.44) * mm});
            skLineSegment(sketch, "E924", {"start": v(-7.6, 6.44) * mm, "end": v(-7.81, 6.69) * mm});
            skLineSegment(sketch, "E925", {"start": v(-7.81, 6.69) * mm, "end": v(-8.18, 7.1) * mm});
            skLineSegment(sketch, "E926", {"start": v(-8.18, 7.1) * mm, "end": v(-8.47, 7.4) * mm});
            skLineSegment(sketch, "E927", {"start": v(-8.47, 7.4) * mm, "end": v(-8.91, 7.83) * mm});
            skLineSegment(sketch, "E928", {"start": v(-8.91, 7.83) * mm, "end": v(-9.48, 8.47) * mm});
            skLineSegment(sketch, "E929", {"start": v(-9.48, 8.47) * mm, "end": v(-9.8, 8.93) * mm});
            skLineSegment(sketch, "E930", {"start": v(-9.8, 8.93) * mm, "end": v(-10, 9.42) * mm});
            skLineSegment(sketch, "E931", {"start": v(-10, 9.42) * mm, "end": v(-10.1, 9.73) * mm});
            skLineSegment(sketch, "E932", {"start": v(-10.1, 9.73) * mm, "end": v(-10.16, 9.96) * mm});
            skLineSegment(sketch, "E933", {"start": v(-10.16, 9.96) * mm, "end": v(-10.24, 10.52) * mm});
            skLineSegment(sketch, "E934", {"start": v(-10.24, 10.52) * mm, "end": v(-10.22, 11.18) * mm});
            skLineSegment(sketch, "E935", {"start": v(-10.22, 11.18) * mm, "end": v(-10.16, 11.67) * mm});
            skLineSegment(sketch, "E936", {"start": v(-10.16, 11.67) * mm, "end": v(-10.12, 11.83) * mm});
            skLineSegment(sketch, "E937", {"start": v(-10.12, 11.83) * mm, "end": v(-10.08, 11.3) * mm});
            skLineSegment(sketch, "E938", {"start": v(-10.08, 11.3) * mm, "end": v(-10.02, 10.99) * mm});
            skLineSegment(sketch, "E939", {"start": v(-10.02, 10.99) * mm, "end": v(-9.91, 10.69) * mm});
            skLineSegment(sketch, "E940", {"start": v(-9.91, 10.69) * mm, "end": v(-9.78, 10.39) * mm});
            skLineSegment(sketch, "E941", {"start": v(-9.78, 10.39) * mm, "end": v(-9.5, 10) * mm});
            skLineSegment(sketch, "E942", {"start": v(-9.5, 10) * mm, "end": v(-9.28, 9.77) * mm});
            skLineSegment(sketch, "E943", {"start": v(-9.28, 9.77) * mm, "end": v(-8.92, 9.44) * mm});
            skLineSegment(sketch, "E944", {"start": v(-8.92, 9.44) * mm, "end": v(-8.65, 9.18) * mm});
            skLineSegment(sketch, "E945", {"start": v(-8.65, 9.18) * mm, "end": v(-8.38, 8.94) * mm});
            skLineSegment(sketch, "E946", {"start": v(-8.38, 8.94) * mm, "end": v(-8.12, 8.68) * mm});
            skLineSegment(sketch, "E947", {"start": v(-8.12, 8.68) * mm, "end": v(-7.9, 8.45) * mm});
            skLineSegment(sketch, "E948", {"start": v(-7.9, 8.45) * mm, "end": v(-7.75, 8.27) * mm});
            skLineSegment(sketch, "E949", {"start": v(-7.75, 8.27) * mm, "end": v(-7.6, 8.11) * mm});
            skLineSegment(sketch, "E950", {"start": v(-7.6, 8.11) * mm, "end": v(-7.42, 7.83) * mm});
            skLineSegment(sketch, "E951", {"start": v(-7.42, 7.83) * mm, "end": v(-7.28, 7.61) * mm});
            skLineSegment(sketch, "E952", {"start": v(-7.28, 7.61) * mm, "end": v(-7.14, 7.4) * mm});
            skLineSegment(sketch, "E953", {"start": v(-7.14, 7.4) * mm, "end": v(-7, 7.1) * mm});
            skLineSegment(sketch, "E954", {"start": v(-7, 7.1) * mm, "end": v(-6.91, 6.84) * mm});
            skLineSegment(sketch, "E955", {"start": v(-6.91, 6.84) * mm, "end": v(-6.81, 6.46) * mm});
            skLineSegment(sketch, "E956", {"start": v(-6.81, 6.46) * mm, "end": v(-6.75, 6.1) * mm});
            skLineSegment(sketch, "E957", {"start": v(-6.75, 6.1) * mm, "end": v(-6.7, 5.66) * mm});
            skLineSegment(sketch, "E958", {"start": v(-6.7, 5.66) * mm, "end": v(-6.66, 5.3) * mm});
            skLineSegment(sketch, "E959", {"start": v(-6.66, 5.3) * mm, "end": v(-6.63, 4.77) * mm});
            skLineSegment(sketch, "E960", {"start": v(-6.63, 4.77) * mm, "end": v(-6.62, 3.88) * mm});
            skLineSegment(sketch, "E961", {"start": v(-20.1, 12.9) * mm, "end": v(-19.97, 12.58) * mm});
            skLineSegment(sketch, "E962", {"start": v(-19.97, 12.58) * mm, "end": v(-19.9, 12.37) * mm});
            skLineSegment(sketch, "E963", {"start": v(-19.9, 12.37) * mm, "end": v(-19.79, 12.13) * mm});
            skLineSegment(sketch, "E964", {"start": v(-19.79, 12.13) * mm, "end": v(-19.68, 11.89) * mm});
            skLineSegment(sketch, "E965", {"start": v(-19.68, 11.89) * mm, "end": v(-19.52, 11.58) * mm});
            skLineSegment(sketch, "E966", {"start": v(-19.52, 11.58) * mm, "end": v(-19.39, 11.36) * mm});
            skLineSegment(sketch, "E967", {"start": v(-19.39, 11.36) * mm, "end": v(-19.22, 11.1) * mm});
            skLineSegment(sketch, "E968", {"start": v(-19.22, 11.1) * mm, "end": v(-19.02, 10.84) * mm});
            skLineSegment(sketch, "E969", {"start": v(-19.02, 10.84) * mm, "end": v(-18.84, 10.67) * mm});
            skLineSegment(sketch, "E970", {"start": v(-18.84, 10.67) * mm, "end": v(-18.68, 10.53) * mm});
            skLineSegment(sketch, "E971", {"start": v(-18.68, 10.53) * mm, "end": v(-18.55, 10.45) * mm});
            skLineSegment(sketch, "E972", {"start": v(-18.55, 10.45) * mm, "end": v(-18.41, 10.37) * mm});
            skLineSegment(sketch, "E973", {"start": v(-18.41, 10.37) * mm, "end": v(-18.25, 10.29) * mm});
            skLineSegment(sketch, "E974", {"start": v(-18.25, 10.29) * mm, "end": v(-18.03, 10.18) * mm});
            skLineSegment(sketch, "E975", {"start": v(-18.03, 10.18) * mm, "end": v(-17.8, 10.1) * mm});
            skLineSegment(sketch, "E976", {"start": v(-17.8, 10.1) * mm, "end": v(-17.42, 9.97) * mm});
            skLineSegment(sketch, "E977", {"start": v(-17.42, 9.97) * mm, "end": v(-17.17, 9.92) * mm});
            skLineSegment(sketch, "E978", {"start": v(-17.17, 9.92) * mm, "end": v(-16.63, 9.83) * mm});
            skLineSegment(sketch, "E979", {"start": v(-16.63, 9.83) * mm, "end": v(-16.35, 9.8) * mm});
            skLineSegment(sketch, "E980", {"start": v(-16.35, 9.8) * mm, "end": v(-15.4, 9.75) * mm});
            skLineSegment(sketch, "E981", {"start": v(-15.4, 9.75) * mm, "end": v(-13.69, 9.75) * mm});
            skLineSegment(sketch, "E982", {"start": v(-13.69, 9.75) * mm, "end": v(-13.23, 9.72) * mm});
            skLineSegment(sketch, "E983", {"start": v(-13.23, 9.72) * mm, "end": v(-12.56, 9.63) * mm});
            skLineSegment(sketch, "E984", {"start": v(-12.56, 9.63) * mm, "end": v(-12.14, 9.53) * mm});
            skLineSegment(sketch, "E985", {"start": v(-12.14, 9.53) * mm, "end": v(-11.77, 9.4) * mm});
            skLineSegment(sketch, "E986", {"start": v(-11.77, 9.4) * mm, "end": v(-11.43, 9.25) * mm});
            skLineSegment(sketch, "E987", {"start": v(-11.43, 9.25) * mm, "end": v(-11.15, 9.08) * mm});
            skLineSegment(sketch, "E988", {"start": v(-11.15, 9.08) * mm, "end": v(-10.95, 8.94) * mm});
            skLineSegment(sketch, "E989", {"start": v(-10.95, 8.94) * mm, "end": v(-10.71, 8.76) * mm});
            skLineSegment(sketch, "E990", {"start": v(-10.71, 8.76) * mm, "end": v(-10.6, 8.66) * mm});
            skLineSegment(sketch, "E991", {"start": v(-10.6, 8.66) * mm, "end": v(-10.38, 8.48) * mm});
            skLineSegment(sketch, "E992", {"start": v(-10.38, 8.48) * mm, "end": v(-10.06, 8.2) * mm});
            skLineSegment(sketch, "E993", {"start": v(-10.06, 8.2) * mm, "end": v(-10.11, 8.3) * mm});
            skLineSegment(sketch, "E994", {"start": v(-10.11, 8.3) * mm, "end": v(-10.3, 8.55) * mm});
            skLineSegment(sketch, "E995", {"start": v(-10.3, 8.55) * mm, "end": v(-10.53, 8.85) * mm});
            skLineSegment(sketch, "E996", {"start": v(-10.53, 8.85) * mm, "end": v(-10.75, 9.18) * mm});
            skLineSegment(sketch, "E997", {"start": v(-10.75, 9.18) * mm, "end": v(-10.9, 9.37) * mm});
            skLineSegment(sketch, "E998", {"start": v(-10.9, 9.37) * mm, "end": v(-11.06, 9.58) * mm});
            skLineSegment(sketch, "E999", {"start": v(-11.06, 9.58) * mm, "end": v(-11.2, 9.75) * mm});
            skLineSegment(sketch, "E1000", {"start": v(-11.2, 9.75) * mm, "end": v(-11.45, 10) * mm});
            skLineSegment(sketch, "E1001", {"start": v(-11.45, 10) * mm, "end": v(-11.63, 10.19) * mm});
            skLineSegment(sketch, "E1002", {"start": v(-11.63, 10.19) * mm, "end": v(-11.87, 10.41) * mm});
            skLineSegment(sketch, "E1003", {"start": v(-11.87, 10.41) * mm, "end": v(-12.1, 10.6) * mm});
            skLineSegment(sketch, "E1004", {"start": v(-12.1, 10.6) * mm, "end": v(-12.3, 10.76) * mm});
            skLineSegment(sketch, "E1005", {"start": v(-12.3, 10.76) * mm, "end": v(-12.62, 10.96) * mm});
            skLineSegment(sketch, "E1006", {"start": v(-12.62, 10.96) * mm, "end": v(-13.03, 11.16) * mm});
            skLineSegment(sketch, "E1007", {"start": v(-13.03, 11.16) * mm, "end": v(-13.34, 11.28) * mm});
            skLineSegment(sketch, "E1008", {"start": v(-13.34, 11.28) * mm, "end": v(-13.8, 11.4) * mm});
            skLineSegment(sketch, "E1009", {"start": v(-13.8, 11.4) * mm, "end": v(-14.1, 11.46) * mm});
            skLineSegment(sketch, "E1010", {"start": v(-14.1, 11.46) * mm, "end": v(-14.65, 11.54) * mm});
            skLineSegment(sketch, "E1011", {"start": v(-14.65, 11.54) * mm, "end": v(-15.55, 11.6) * mm});
            skLineSegment(sketch, "E1012", {"start": v(-15.55, 11.6) * mm, "end": v(-16.62, 11.64) * mm});
            skLineSegment(sketch, "E1013", {"start": v(-16.62, 11.64) * mm, "end": v(-17.86, 11.78) * mm});
            skLineSegment(sketch, "E1014", {"start": v(-17.86, 11.78) * mm, "end": v(-18.7, 11.96) * mm});
            skLineSegment(sketch, "E1015", {"start": v(-18.7, 11.96) * mm, "end": v(-18.97, 12.08) * mm});
            skLineSegment(sketch, "E1016", {"start": v(-18.97, 12.08) * mm, "end": v(-19.32, 12.26) * mm});
            skLineSegment(sketch, "E1017", {"start": v(-19.32, 12.26) * mm, "end": v(-19.6, 12.47) * mm});
            skLineSegment(sketch, "E1018", {"start": v(-19.6, 12.47) * mm, "end": v(-19.93, 12.73) * mm});
            skLineSegment(sketch, "E1019", {"start": v(-19.93, 12.73) * mm, "end": v(-20.1, 12.9) * mm});
            skLineSegment(sketch, "E1020.MirrorCS", {"start": v(5.7, 5.3) * mm, "end": v(5.67, 4.77) * mm});
            skLineSegment(sketch, "E1021.MirrorCS", {"start": v(5.74, 5.66) * mm, "end": v(5.7, 5.3) * mm});
            skLineSegment(sketch, "E1022.MirrorCS", {"start": v(5.79, 4.72) * mm, "end": v(6.01, 5.39) * mm});
            skLineSegment(sketch, "E1023.MirrorCS", {"start": v(5.67, 4.77) * mm, "end": v(5.67, 3.88) * mm});
            skLineSegment(sketch, "E1024.MirrorCS", {"start": v(5.67, 3.88) * mm, "end": v(5.79, 4.72) * mm});
            skLineSegment(sketch, "E1025.MirrorCS", {"start": v(5.8, 6.1) * mm, "end": v(5.74, 5.66) * mm});
            skLineSegment(sketch, "E1026.MirrorCS", {"start": v(5.86, 6.46) * mm, "end": v(5.8, 6.1) * mm});
            skLineSegment(sketch, "E1027.MirrorCS", {"start": v(9.2, 11.67) * mm, "end": v(9.17, 11.83) * mm});
            skLineSegment(sketch, "E1028.MirrorCS", {"start": v(10.91, 10.41) * mm, "end": v(11.14, 10.6) * mm});
            skLineSegment(sketch, "E1029.MirrorCS", {"start": v(10.82, 9.4) * mm, "end": v(10.48, 9.25) * mm});
            skLineSegment(sketch, "E1030.MirrorCS", {"start": v(10.25, 9.75) * mm, "end": v(10.5, 10) * mm});
            skLineSegment(sketch, "E1031.MirrorCS", {"start": v(11.6, 9.63) * mm, "end": v(11.19, 9.53) * mm});
            skLineSegment(sketch, "E1032.MirrorCS", {"start": v(11.67, 10.96) * mm, "end": v(12.07, 11.16) * mm});
            skLineSegment(sketch, "E1033.MirrorCS", {"start": v(9.05, 9.42) * mm, "end": v(9.15, 9.73) * mm});
            skLineSegment(sketch, "E1034.MirrorCS", {"start": v(12.84, 11.4) * mm, "end": v(13.15, 11.46) * mm});
            skLineSegment(sketch, "E1035.MirrorCS", {"start": v(9.2, 9.96) * mm, "end": v(9.28, 10.52) * mm});
            skLineSegment(sketch, "E1036.MirrorCS", {"start": v(9.17, 11.83) * mm, "end": v(9.13, 11.3) * mm});
            skLineSegment(sketch, "E1037.MirrorCS", {"start": v(10.1, 9.58) * mm, "end": v(10.25, 9.75) * mm});
            skLineSegment(sketch, "E1038.MirrorCS", {"start": v(9.94, 9.37) * mm, "end": v(10.1, 9.58) * mm});
            skLineSegment(sketch, "E1039.MirrorCS", {"start": v(11.19, 9.53) * mm, "end": v(10.82, 9.4) * mm});
            skLineSegment(sketch, "E1040.MirrorCS", {"start": v(8.54, 10) * mm, "end": v(8.32, 9.77) * mm});
            skLineSegment(sketch, "E1041.MirrorCS", {"start": v(11.14, 10.6) * mm, "end": v(11.35, 10.76) * mm});
            skLineSegment(sketch, "E1042.MirrorCS", {"start": v(9.15, 9.73) * mm, "end": v(9.2, 9.96) * mm});
            skLineSegment(sketch, "E1043.MirrorCS", {"start": v(9.27, 11.18) * mm, "end": v(9.2, 11.67) * mm});
            skLineSegment(sketch, "E1044.MirrorCS", {"start": v(9.06, 10.99) * mm, "end": v(8.96, 10.69) * mm});
            skLineSegment(sketch, "E1045.MirrorCS", {"start": v(10.67, 10.19) * mm, "end": v(10.91, 10.41) * mm});
            skLineSegment(sketch, "E1046.MirrorCS", {"start": v(8.82, 10.39) * mm, "end": v(8.54, 10) * mm});
            skLineSegment(sketch, "E1047.MirrorCS", {"start": v(11.35, 10.76) * mm, "end": v(11.67, 10.96) * mm});
            skLineSegment(sketch, "E1048.MirrorCS", {"start": v(8.96, 10.69) * mm, "end": v(8.82, 10.39) * mm});
            skLineSegment(sketch, "E1049.MirrorCS", {"start": v(12.07, 11.16) * mm, "end": v(12.38, 11.28) * mm});
            skLineSegment(sketch, "E1050.MirrorCS", {"start": v(10.5, 10) * mm, "end": v(10.67, 10.19) * mm});
            skLineSegment(sketch, "E1051.MirrorCS", {"start": v(12.38, 11.28) * mm, "end": v(12.84, 11.4) * mm});
            skLineSegment(sketch, "E1052.MirrorCS", {"start": v(8.32, 9.77) * mm, "end": v(7.97, 9.44) * mm});
            skLineSegment(sketch, "E1053.MirrorCS", {"start": v(12.73, 9.75) * mm, "end": v(12.27, 9.72) * mm});
            skLineSegment(sketch, "E1054.MirrorCS", {"start": v(9.28, 10.52) * mm, "end": v(9.27, 11.18) * mm});
            skLineSegment(sketch, "E1055.MirrorCS", {"start": v(9.13, 11.3) * mm, "end": v(9.06, 10.99) * mm});
            skLineSegment(sketch, "E1056.MirrorCS", {"start": v(12.27, 9.72) * mm, "end": v(11.6, 9.63) * mm});
            skLineSegment(sketch, "E1057.MirrorCS", {"start": v(9.1, 8.2) * mm, "end": v(9.16, 8.3) * mm});
            skLineSegment(sketch, "E1058.MirrorCS", {"start": v(6.8, 8.27) * mm, "end": v(6.66, 8.11) * mm});
            skLineSegment(sketch, "E1059.MirrorCS", {"start": v(6.94, 8.45) * mm, "end": v(6.8, 8.27) * mm});
            skLineSegment(sketch, "E1060.MirrorCS", {"start": v(9.16, 8.3) * mm, "end": v(9.34, 8.55) * mm});
            skLineSegment(sketch, "E1061.MirrorCS", {"start": v(7.43, 8.94) * mm, "end": v(7.17, 8.68) * mm});
            skLineSegment(sketch, "E1062.MirrorCS", {"start": v(9.43, 8.48) * mm, "end": v(9.1, 8.2) * mm});
            skLineSegment(sketch, "E1063.MirrorCS", {"start": v(7.7, 9.18) * mm, "end": v(7.43, 8.94) * mm});
            skLineSegment(sketch, "E1064.MirrorCS", {"start": v(8.84, 8.93) * mm, "end": v(9.05, 9.42) * mm});
            skLineSegment(sketch, "E1065.MirrorCS", {"start": v(9.34, 8.55) * mm, "end": v(9.57, 8.85) * mm});
            skLineSegment(sketch, "E1066.MirrorCS", {"start": v(7.17, 8.68) * mm, "end": v(6.94, 8.45) * mm});
            skLineSegment(sketch, "E1067.MirrorCS", {"start": v(8.53, 8.47) * mm, "end": v(8.84, 8.93) * mm});
            skLineSegment(sketch, "E1068.MirrorCS", {"start": v(7.97, 9.44) * mm, "end": v(7.7, 9.18) * mm});
            skLineSegment(sketch, "E1069.MirrorCS", {"start": v(10, 8.94) * mm, "end": v(9.76, 8.76) * mm});
            skLineSegment(sketch, "E1070.MirrorCS", {"start": v(9.64, 8.66) * mm, "end": v(9.43, 8.48) * mm});
            skLineSegment(sketch, "E1071.MirrorCS", {"start": v(9.76, 8.76) * mm, "end": v(9.64, 8.66) * mm});
            skLineSegment(sketch, "E1072.MirrorCS", {"start": v(18.65, 12.47) * mm, "end": v(18.97, 12.73) * mm});
            skLineSegment(sketch, "E1073.MirrorCS", {"start": v(19.15, 12.9) * mm, "end": v(19.02, 12.58) * mm});
            skLineSegment(sketch, "E1074.MirrorCS", {"start": v(19.02, 12.58) * mm, "end": v(18.94, 12.37) * mm});
            skLineSegment(sketch, "E1075.MirrorCS", {"start": v(18.94, 12.37) * mm, "end": v(18.83, 12.13) * mm});
            skLineSegment(sketch, "E1076.MirrorCS", {"start": v(18.97, 12.73) * mm, "end": v(19.15, 12.9) * mm});
            skLineSegment(sketch, "E1077.MirrorCS", {"start": v(9.57, 8.85) * mm, "end": v(9.8, 9.18) * mm});
            skLineSegment(sketch, "E1078.MirrorCS", {"start": v(17.46, 10.37) * mm, "end": v(17.3, 10.29) * mm});
            skLineSegment(sketch, "E1079.MirrorCS", {"start": v(6.35, 6.02) * mm, "end": v(6.65, 6.44) * mm});
            skLineSegment(sketch, "E1080.MirrorCS", {"start": v(13.7, 11.54) * mm, "end": v(14.6, 11.6) * mm});
            skLineSegment(sketch, "E1081.MirrorCS", {"start": v(6.19, 7.4) * mm, "end": v(6.05, 7.1) * mm});
            skLineSegment(sketch, "E1082.MirrorCS", {"start": v(5.96, 6.84) * mm, "end": v(5.86, 6.46) * mm});
            skLineSegment(sketch, "E1083.MirrorCS", {"start": v(16.85, 10.1) * mm, "end": v(16.47, 9.97) * mm});
            skLineSegment(sketch, "E1084.MirrorCS", {"start": v(18.01, 12.08) * mm, "end": v(18.37, 12.26) * mm});
            skLineSegment(sketch, "E1085.MirrorCS", {"start": v(15.68, 9.83) * mm, "end": v(15.4, 9.8) * mm});
            skLineSegment(sketch, "E1086.MirrorCS", {"start": v(18.72, 11.89) * mm, "end": v(18.57, 11.58) * mm});
            skLineSegment(sketch, "E1087.MirrorCS", {"start": v(9.8, 9.18) * mm, "end": v(9.94, 9.37) * mm});
            skLineSegment(sketch, "E1088.MirrorCS", {"start": v(16.22, 9.92) * mm, "end": v(15.68, 9.83) * mm});
            skLineSegment(sketch, "E1089.MirrorCS", {"start": v(17.75, 11.96) * mm, "end": v(18.01, 12.08) * mm});
            skLineSegment(sketch, "E1090.MirrorCS", {"start": v(7.96, 7.83) * mm, "end": v(8.53, 8.47) * mm});
            skLineSegment(sketch, "E1091.MirrorCS", {"start": v(13.15, 11.46) * mm, "end": v(13.7, 11.54) * mm});
            skLineSegment(sketch, "E1092.MirrorCS", {"start": v(6.01, 5.39) * mm, "end": v(6.35, 6.02) * mm});
            skLineSegment(sketch, "E1093.MirrorCS", {"start": v(18.27, 11.1) * mm, "end": v(18.06, 10.84) * mm});
            skLineSegment(sketch, "E1094.MirrorCS", {"start": v(17.07, 10.18) * mm, "end": v(16.85, 10.1) * mm});
            skLineSegment(sketch, "E1095.MirrorCS", {"start": v(18.06, 10.84) * mm, "end": v(17.89, 10.67) * mm});
            skLineSegment(sketch, "E1096.MirrorCS", {"start": v(17.73, 10.53) * mm, "end": v(17.6, 10.45) * mm});
            skLineSegment(sketch, "E1097.MirrorCS", {"start": v(6.86, 6.69) * mm, "end": v(7.23, 7.1) * mm});
            skLineSegment(sketch, "E1098.MirrorCS", {"start": v(17.89, 10.67) * mm, "end": v(17.73, 10.53) * mm});
            skLineSegment(sketch, "E1099.MirrorCS", {"start": v(16.47, 9.97) * mm, "end": v(16.22, 9.92) * mm});
            skLineSegment(sketch, "E1100.MirrorCS", {"start": v(17.3, 10.29) * mm, "end": v(17.07, 10.18) * mm});
            skLineSegment(sketch, "E1101.MirrorCS", {"start": v(6.66, 8.11) * mm, "end": v(6.47, 7.83) * mm});
            skLineSegment(sketch, "E1102.MirrorCS", {"start": v(10.48, 9.25) * mm, "end": v(10.2, 9.08) * mm});
            skLineSegment(sketch, "E1103.MirrorCS", {"start": v(6.05, 7.1) * mm, "end": v(5.96, 6.84) * mm});
            skLineSegment(sketch, "E1104.MirrorCS", {"start": v(7.23, 7.1) * mm, "end": v(7.52, 7.4) * mm});
            skLineSegment(sketch, "E1105.MirrorCS", {"start": v(18.43, 11.36) * mm, "end": v(18.27, 11.1) * mm});
            skLineSegment(sketch, "E1106.MirrorCS", {"start": v(10.2, 9.08) * mm, "end": v(10, 8.94) * mm});
            skLineSegment(sketch, "E1107.MirrorCS", {"start": v(6.65, 6.44) * mm, "end": v(6.86, 6.69) * mm});
            skLineSegment(sketch, "E1108.MirrorCS", {"start": v(18.83, 12.13) * mm, "end": v(18.72, 11.89) * mm});
            skLineSegment(sketch, "E1109.MirrorCS", {"start": v(18.57, 11.58) * mm, "end": v(18.43, 11.36) * mm});
            skLineSegment(sketch, "E1110.MirrorCS", {"start": v(7.52, 7.4) * mm, "end": v(7.96, 7.83) * mm});
            skLineSegment(sketch, "E1111.MirrorCS", {"start": v(6.32, 7.61) * mm, "end": v(6.19, 7.4) * mm});
            skLineSegment(sketch, "E1112.MirrorCS", {"start": v(16.9, 11.78) * mm, "end": v(17.75, 11.96) * mm});
            skLineSegment(sketch, "E1113.MirrorCS", {"start": v(6.47, 7.83) * mm, "end": v(6.32, 7.61) * mm});
            skLineSegment(sketch, "E1114.MirrorCS", {"start": v(18.37, 12.26) * mm, "end": v(18.65, 12.47) * mm});
            skLineSegment(sketch, "E1115.MirrorCS", {"start": v(17.6, 10.45) * mm, "end": v(17.46, 10.37) * mm});
            skLineSegment(sketch, "E1116.MirrorCS", {"start": v(14.45, 9.75) * mm, "end": v(12.73, 9.75) * mm});
            skLineSegment(sketch, "E1117.MirrorCS", {"start": v(14.6, 11.6) * mm, "end": v(15.67, 11.64) * mm});
            skLineSegment(sketch, "E1118.MirrorCS", {"start": v(15.4, 9.8) * mm, "end": v(14.45, 9.75) * mm});
            skLineSegment(sketch, "E1119.MirrorCS", {"start": v(15.67, 11.64) * mm, "end": v(16.9, 11.78) * mm});
            skLineSegment(sketch, "E1120", {"start": v(-0.5, -6.58) * mm, "end": v(-1.07, -5.43) * mm});
            skLineSegment(sketch, "E1121", {"start": v(-1.07, -5.43) * mm, "end": v(-1.7, -4.38) * mm});
            skLineSegment(sketch, "E1122", {"start": v(-1.7, -4.38) * mm, "end": v(-2.37, -3.49) * mm});
            skLineSegment(sketch, "E1123", {"start": v(-2.37, -3.49) * mm, "end": v(-3.21, -2.66) * mm});
            skLineSegment(sketch, "E1124", {"start": v(-3.21, -2.66) * mm, "end": v(-4.5, -1.75) * mm});
            skLineSegment(sketch, "E1125", {"start": v(-4.5, -1.75) * mm, "end": v(-6.38, -0.8) * mm});
            skLineSegment(sketch, "E1126", {"start": v(-6.38, -0.8) * mm, "end": v(-7.36, -0.33) * mm});
            skLineSegment(sketch, "E1127", {"start": v(-7.36, -0.33) * mm, "end": v(-7.76, -0.09) * mm});
            skLineSegment(sketch, "E1128", {"start": v(-7.76, -0.09) * mm, "end": v(-8, 0.16) * mm});
            skLineSegment(sketch, "E1129", {"start": v(-8, 0.16) * mm, "end": v(-8.11, 0.31) * mm});
            skLineSegment(sketch, "E1130", {"start": v(-8.11, 0.31) * mm, "end": v(-8.2, 0.52) * mm});
            skLineSegment(sketch, "E1131", {"start": v(-8.2, 0.52) * mm, "end": v(-8.23, 0.65) * mm});
            skLineSegment(sketch, "E1132", {"start": v(-8.23, 0.65) * mm, "end": v(-8.27, 0.81) * mm});
            skLineSegment(sketch, "E1133", {"start": v(-8.27, 0.81) * mm, "end": v(-8.28, 1.21) * mm});
            skLineSegment(sketch, "E1134", {"start": v(-8.28, 1.21) * mm, "end": v(-8.2, 1.66) * mm});
            skLineSegment(sketch, "E1135", {"start": v(-8.2, 1.66) * mm, "end": v(-8.1, 1.44) * mm});
            skLineSegment(sketch, "E1136", {"start": v(-8.1, 1.44) * mm, "end": v(-7.94, 1.08) * mm});
            skLineSegment(sketch, "E1137", {"start": v(-7.94, 1.08) * mm, "end": v(-7.8, 0.86) * mm});
            skLineSegment(sketch, "E1138", {"start": v(-7.8, 0.86) * mm, "end": v(-7.67, 0.69) * mm});
            skLineSegment(sketch, "E1139", {"start": v(-7.67, 0.69) * mm, "end": v(-7.53, 0.54) * mm});
            skLineSegment(sketch, "E1140", {"start": v(-7.53, 0.54) * mm, "end": v(-7.3, 0.42) * mm});
            skLineSegment(sketch, "E1141", {"start": v(-7.3, 0.42) * mm, "end": v(-6.72, 0.23) * mm});
            skLineSegment(sketch, "E1142", {"start": v(-6.72, 0.23) * mm, "end": v(-5.77, 0.02) * mm});
            skLineSegment(sketch, "E1143", {"start": v(-5.77, 0.02) * mm, "end": v(-5.85, 0.18) * mm});
            skLineSegment(sketch, "E1144", {"start": v(-5.85, 0.18) * mm, "end": v(-5.92, 0.34) * mm});
            skLineSegment(sketch, "E1145", {"start": v(-5.92, 0.34) * mm, "end": v(-6.01, 0.49) * mm});
            skLineSegment(sketch, "E1146", {"start": v(-6.01, 0.49) * mm, "end": v(-6.1, 0.64) * mm});
            skLineSegment(sketch, "E1147", {"start": v(-6.1, 0.64) * mm, "end": v(-5.96, 0.62) * mm});
            skLineSegment(sketch, "E1148", {"start": v(-5.96, 0.62) * mm, "end": v(-5.66, 0.5) * mm});
            skLineSegment(sketch, "E1149", {"start": v(-5.66, 0.5) * mm, "end": v(-5.15, 0.32) * mm});
            skLineSegment(sketch, "E1150", {"start": v(-5.15, 0.32) * mm, "end": v(-4.9, 0.2) * mm});
            skLineSegment(sketch, "E1151", {"start": v(-4.9, 0.2) * mm, "end": v(-4.72, 0.06) * mm});
            skLineSegment(sketch, "E1152", {"start": v(-4.72, 0.06) * mm, "end": v(-4.5, -0.14) * mm});
            skLineSegment(sketch, "E1153", {"start": v(-4.5, -0.14) * mm, "end": v(-4.27, -0.37) * mm});
            skLineSegment(sketch, "E1154", {"start": v(-4.27, -0.37) * mm, "end": v(-4.07, -0.62) * mm});
            skLineSegment(sketch, "E1155", {"start": v(-4.07, -0.62) * mm, "end": v(-4.14, -0.32) * mm});
            skLineSegment(sketch, "E1156", {"start": v(-4.14, -0.32) * mm, "end": v(-4.23, 0.02) * mm});
            skLineSegment(sketch, "E1157", {"start": v(-4.23, 0.02) * mm, "end": v(-4.32, 0.33) * mm});
            skLineSegment(sketch, "E1158", {"start": v(-4.32, 0.33) * mm, "end": v(-4.34, 0.54) * mm});
            skLineSegment(sketch, "E1159", {"start": v(-4.34, 0.54) * mm, "end": v(-4.28, 0.62) * mm});
            skLineSegment(sketch, "E1160", {"start": v(-4.28, 0.62) * mm, "end": v(-4.11, 0.62) * mm});
            skLineSegment(sketch, "E1161", {"start": v(-4.11, 0.62) * mm, "end": v(-3.9, 0.51) * mm});
            skLineSegment(sketch, "E1162", {"start": v(-3.9, 0.51) * mm, "end": v(-3.74, 0.4) * mm});
            skLineSegment(sketch, "E1163", {"start": v(-3.74, 0.4) * mm, "end": v(-3.6, 0.27) * mm});
            skLineSegment(sketch, "E1164", {"start": v(-3.6, 0.27) * mm, "end": v(-3.39, 0.07) * mm});
            skLineSegment(sketch, "E1165", {"start": v(-3.39, 0.07) * mm, "end": v(-3.22, -0.03) * mm});
            skLineSegment(sketch, "E1166", {"start": v(-3.22, -0.03) * mm, "end": v(-3, -0.12) * mm});
            skLineSegment(sketch, "E1167", {"start": v(-3, -0.12) * mm, "end": v(-2.68, -0.15) * mm});
            skLineSegment(sketch, "E1168", {"start": v(-2.68, -0.15) * mm, "end": v(-2.56, -0.14) * mm});
            skLineSegment(sketch, "E1169", {"start": v(-2.56, -0.14) * mm, "end": v(-2.68, -0.26) * mm});
            skLineSegment(sketch, "E1170", {"start": v(-2.68, -0.26) * mm, "end": v(-3.02, -0.65) * mm});
            skLineSegment(sketch, "E1171", {"start": v(-3.02, -0.65) * mm, "end": v(-2.29, -0.59) * mm});
            skLineSegment(sketch, "E1172", {"start": v(-2.29, -0.59) * mm, "end": v(-1.87, -0.5) * mm});
            skLineSegment(sketch, "E1173", {"start": v(-1.87, -0.5) * mm, "end": v(-1.76, -0.45) * mm});
            skLineSegment(sketch, "E1174", {"start": v(-1.76, -0.45) * mm, "end": v(-1.78, -0.62) * mm});
            skLineSegment(sketch, "E1175", {"start": v(-1.78, -0.62) * mm, "end": v(-1.77, -0.85) * mm});
            skLineSegment(sketch, "E1176", {"start": v(-1.77, -0.85) * mm, "end": v(-1.73, -1.13) * mm});
            skLineSegment(sketch, "E1177", {"start": v(-1.73, -1.13) * mm, "end": v(-1.63, -1.4) * mm});
            skLineSegment(sketch, "E1178", {"start": v(-1.63, -1.4) * mm, "end": v(-1.45, -1.82) * mm});
            skLineSegment(sketch, "E1179", {"start": v(-1.45, -1.82) * mm, "end": v(-1.25, -1.22) * mm});
            skLineSegment(sketch, "E1180", {"start": v(-1.25, -1.22) * mm, "end": v(-1.22, -1.27) * mm});
            skLineSegment(sketch, "E1181", {"start": v(-1.22, -1.27) * mm, "end": v(-1.1, -1.77) * mm});
            skLineSegment(sketch, "E1182", {"start": v(-1.1, -1.77) * mm, "end": v(-0.86, -2.33) * mm});
            skLineSegment(sketch, "E1183", {"start": v(-0.86, -2.33) * mm, "end": v(-0.69, -2.88) * mm});
            skLineSegment(sketch, "E1184", {"start": v(-0.69, -2.88) * mm, "end": v(-0.57, -3.37) * mm});
            skLineSegment(sketch, "E1185", {"start": v(-0.57, -3.37) * mm, "end": v(-0.5, -3.83) * mm});
            skLineSegment(sketch, "E1186", {"start": v(-0.5, -3.83) * mm, "end": v(-0.49, -4.37) * mm});
            skLineSegment(sketch, "E1187", {"start": v(-0.49, -4.37) * mm, "end": v(-0.49, -5.24) * mm});
            skLineSegment(sketch, "E1188", {"start": v(-0.49, -5.24) * mm, "end": v(-0.3, -4.67) * mm});
            skLineSegment(sketch, "E1189", {"start": v(-0.3, -4.67) * mm, "end": v(-0.12, -4) * mm});
            skLineSegment(sketch, "E1190", {"start": v(-0.12, -4) * mm, "end": v(-0.01, -3.47) * mm});
            skLineSegment(sketch, "E1191", {"start": v(-0.01, -3.47) * mm, "end": v(0.03, -3.18) * mm});
            skLineSegment(sketch, "E1192", {"start": v(0.03, -3.18) * mm, "end": v(0.05, -2.7) * mm});
            skLineSegment(sketch, "E1193", {"start": v(0.05, -2.7) * mm, "end": v(-0.04, -1.62) * mm});
            skLineSegment(sketch, "E1194", {"start": v(-0.04, -1.62) * mm, "end": v(-0.08, -1) * mm});
            skLineSegment(sketch, "E1195", {"start": v(-0.08, -1) * mm, "end": v(0.06, -1.16) * mm});
            skLineSegment(sketch, "E1196", {"start": v(0.06, -1.16) * mm, "end": v(0.18, -1.35) * mm});
            skLineSegment(sketch, "E1197", {"start": v(0.18, -1.35) * mm, "end": v(0.4, -1.65) * mm});
            skLineSegment(sketch, "E1198", {"start": v(0.4, -1.65) * mm, "end": v(0.38, -1) * mm});
            skLineSegment(sketch, "E1199", {"start": v(0.38, -1) * mm, "end": v(0.33, -0.33) * mm});
            skLineSegment(sketch, "E1200", {"start": v(0.33, -0.33) * mm, "end": v(0.8, -0.4) * mm});
            skLineSegment(sketch, "E1201", {"start": v(0.8, -0.4) * mm, "end": v(1.17, -0.34) * mm});
            skLineSegment(sketch, "E1202", {"start": v(1.17, -0.34) * mm, "end": v(1.47, -0.22) * mm});
            skLineSegment(sketch, "E1203", {"start": v(1.47, -0.22) * mm, "end": v(1.63, -0.12) * mm});
            skLineSegment(sketch, "E1204", {"start": v(1.63, -0.12) * mm, "end": v(1.3, 0.07) * mm});
            skLineSegment(sketch, "E1205", {"start": v(1.3, 0.07) * mm, "end": v(1.8, 0.26) * mm});
            skLineSegment(sketch, "E1206", {"start": v(1.8, 0.26) * mm, "end": v(2.19, 0.4) * mm});
            skLineSegment(sketch, "E1207", {"start": v(2.19, 0.4) * mm, "end": v(2.67, 0.53) * mm});
            skLineSegment(sketch, "E1208", {"start": v(2.67, 0.53) * mm, "end": v(2.97, 0.56) * mm});
            skLineSegment(sketch, "E1209", {"start": v(2.97, 0.56) * mm, "end": v(3.2, 0.51) * mm});
            skLineSegment(sketch, "E1210", {"start": v(3.2, 0.51) * mm, "end": v(3.28, 0.4) * mm});
            skLineSegment(sketch, "E1211", {"start": v(3.28, 0.4) * mm, "end": v(3.3, 0.24) * mm});
            skLineSegment(sketch, "E1212", {"start": v(3.3, 0.24) * mm, "end": v(3.28, 0.04) * mm});
            skLineSegment(sketch, "E1213", {"start": v(3.28, 0.04) * mm, "end": v(3.18, -0.25) * mm});
            skLineSegment(sketch, "E1214", {"start": v(3.18, -0.25) * mm, "end": v(3.07, -0.58) * mm});
            skLineSegment(sketch, "E1215", {"start": v(3.07, -0.58) * mm, "end": v(3.26, -0.35) * mm});
            skLineSegment(sketch, "E1216", {"start": v(3.26, -0.35) * mm, "end": v(3.5, -0.1) * mm});
            skLineSegment(sketch, "E1217", {"start": v(3.5, -0.1) * mm, "end": v(3.76, 0.11) * mm});
            skLineSegment(sketch, "E1218", {"start": v(3.76, 0.11) * mm, "end": v(4, 0.26) * mm});
            skLineSegment(sketch, "E1219", {"start": v(4, 0.26) * mm, "end": v(4.2, 0.35) * mm});
            skLineSegment(sketch, "E1220", {"start": v(4.2, 0.35) * mm, "end": v(4.58, 0.5) * mm});
            skLineSegment(sketch, "E1221", {"start": v(4.58, 0.5) * mm, "end": v(4.93, 0.61) * mm});
            skLineSegment(sketch, "E1222", {"start": v(4.93, 0.61) * mm, "end": v(5.08, 0.67) * mm});
            skLineSegment(sketch, "E1223", {"start": v(5.08, 0.67) * mm, "end": v(5.03, 0.55) * mm});
            skLineSegment(sketch, "E1224", {"start": v(5.03, 0.55) * mm, "end": v(4.96, 0.41) * mm});
            skLineSegment(sketch, "E1225", {"start": v(4.96, 0.41) * mm, "end": v(4.8, 0.12) * mm});
            skLineSegment(sketch, "E1226", {"start": v(4.8, 0.12) * mm, "end": v(4.74, 0.02) * mm});
            skLineSegment(sketch, "E1227", {"start": v(4.74, 0.02) * mm, "end": v(4.89, 0.03) * mm});
            skLineSegment(sketch, "E1228", {"start": v(4.89, 0.03) * mm, "end": v(5.05, 0.08) * mm});
            skLineSegment(sketch, "E1229", {"start": v(5.05, 0.08) * mm, "end": v(5.23, 0.1) * mm});
            skLineSegment(sketch, "E1230", {"start": v(5.23, 0.1) * mm, "end": v(5.62, 0.2) * mm});
            skLineSegment(sketch, "E1231", {"start": v(5.62, 0.2) * mm, "end": v(6, 0.33) * mm});
            skLineSegment(sketch, "E1232", {"start": v(6, 0.33) * mm, "end": v(6.42, 0.48) * mm});
            skLineSegment(sketch, "E1233", {"start": v(6.42, 0.48) * mm, "end": v(6.64, 0.66) * mm});
            skLineSegment(sketch, "E1234", {"start": v(6.64, 0.66) * mm, "end": v(6.83, 0.93) * mm});
            skLineSegment(sketch, "E1235", {"start": v(6.83, 0.93) * mm, "end": v(7, 1.26) * mm});
            skLineSegment(sketch, "E1236", {"start": v(7, 1.26) * mm, "end": v(7.14, 1.66) * mm});
            skLineSegment(sketch, "E1237", {"start": v(7.14, 1.66) * mm, "end": v(7.2, 1.5) * mm});
            skLineSegment(sketch, "E1238", {"start": v(7.2, 1.5) * mm, "end": v(7.24, 1.26) * mm});
            skLineSegment(sketch, "E1239", {"start": v(7.24, 1.26) * mm, "end": v(7.25, 0.92) * mm});
            skLineSegment(sketch, "E1240", {"start": v(7.25, 0.92) * mm, "end": v(7.18, 0.5) * mm});
            skLineSegment(sketch, "E1241", {"start": v(7.18, 0.5) * mm, "end": v(7.1, 0.32) * mm});
            skLineSegment(sketch, "E1242", {"start": v(7.1, 0.32) * mm, "end": v(6.98, 0.15) * mm});
            skLineSegment(sketch, "E1243", {"start": v(6.98, 0.15) * mm, "end": v(6.86, 0.03) * mm});
            skLineSegment(sketch, "E1244", {"start": v(6.86, 0.03) * mm, "end": v(6.7, -0.11) * mm});
            skLineSegment(sketch, "E1245", {"start": v(6.7, -0.11) * mm, "end": v(6.28, -0.35) * mm});
            skLineSegment(sketch, "E1246", {"start": v(6.28, -0.35) * mm, "end": v(5.74, -0.62) * mm});
            skLineSegment(sketch, "E1247", {"start": v(5.74, -0.62) * mm, "end": v(5.09, -0.93) * mm});
            skLineSegment(sketch, "E1248", {"start": v(5.09, -0.93) * mm, "end": v(4.57, -1.18) * mm});
            skLineSegment(sketch, "E1249", {"start": v(4.57, -1.18) * mm, "end": v(3.81, -1.56) * mm});
            skLineSegment(sketch, "E1250", {"start": v(3.81, -1.56) * mm, "end": v(3.22, -1.92) * mm});
            skLineSegment(sketch, "E1251", {"start": v(3.22, -1.92) * mm, "end": v(2.78, -2.24) * mm});
            skLineSegment(sketch, "E1252", {"start": v(2.78, -2.24) * mm, "end": v(2.24, -2.65) * mm});
            skLineSegment(sketch, "E1253", {"start": v(2.24, -2.65) * mm, "end": v(2, -2.88) * mm});
            skLineSegment(sketch, "E1254", {"start": v(2, -2.88) * mm, "end": v(1.66, -3.23) * mm});
            skLineSegment(sketch, "E1255", {"start": v(1.66, -3.23) * mm, "end": v(1.46, -3.48) * mm});
            skLineSegment(sketch, "E1256", {"start": v(1.46, -3.48) * mm, "end": v(1.2, -3.78) * mm});
            skLineSegment(sketch, "E1257", {"start": v(1.2, -3.78) * mm, "end": v(0.77, -4.37) * mm});
            skLineSegment(sketch, "E1258", {"start": v(0.77, -4.37) * mm, "end": v(0.5, -4.77) * mm});
            skLineSegment(sketch, "E1259", {"start": v(0.5, -4.77) * mm, "end": v(0.16, -5.36) * mm});
            skLineSegment(sketch, "E1260", {"start": v(0.16, -5.36) * mm, "end": v(0.02, -5.64) * mm});
            skLineSegment(sketch, "E1261", {"start": v(0.02, -5.64) * mm, "end": v(-0.13, -5.9) * mm});
            skLineSegment(sketch, "E1262", {"start": v(-0.13, -5.9) * mm, "end": v(-0.47, -6.59) * mm});
            skLineSegment(sketch, "E1263", {"start": v(-0.47, -6.59) * mm, "end": v(-0.5, -6.58) * mm});
            skLineSegment(sketch, "E1264", {"start": v(-0.3, -3.72) * mm, "end": v(-0.35, -3.41) * mm});
            skLineSegment(sketch, "E1265", {"start": v(-0.35, -3.41) * mm, "end": v(-0.4, -3.08) * mm});
            skLineSegment(sketch, "E1266", {"start": v(-0.4, -3.08) * mm, "end": v(-0.49, -2.77) * mm});
            skLineSegment(sketch, "E1267", {"start": v(-0.49, -2.77) * mm, "end": v(-0.6, -2.44) * mm});
            skLineSegment(sketch, "E1268", {"start": v(-0.6, -2.44) * mm, "end": v(-0.72, -2.12) * mm});
            skLineSegment(sketch, "E1269", {"start": v(-0.72, -2.12) * mm, "end": v(-0.83, -1.86) * mm});
            skLineSegment(sketch, "E1270", {"start": v(-0.83, -1.86) * mm, "end": v(-0.92, -1.56) * mm});
            skLineSegment(sketch, "E1271", {"start": v(-0.92, -1.56) * mm, "end": v(-1.01, -1.26) * mm});
            skLineSegment(sketch, "E1272", {"start": v(-1.01, -1.26) * mm, "end": v(-1.1, -0.92) * mm});
            skLineSegment(sketch, "E1273", {"start": v(-1.1, -0.92) * mm, "end": v(-1.15, -0.58) * mm});
            skLineSegment(sketch, "E1274", {"start": v(-1.15, -0.58) * mm, "end": v(-1.2, -0.38) * mm});
            skLineSegment(sketch, "E1275", {"start": v(-1.2, -0.38) * mm, "end": v(-1.28, -0.65) * mm});
            skLineSegment(sketch, "E1276", {"start": v(-1.28, -0.65) * mm, "end": v(-1.35, -0.87) * mm});
            skLineSegment(sketch, "E1277", {"start": v(-1.35, -0.87) * mm, "end": v(-1.44, -1.12) * mm});
            skLineSegment(sketch, "E1278", {"start": v(-1.44, -1.12) * mm, "end": v(-1.49, -1.17) * mm});
            skLineSegment(sketch, "E1279", {"start": v(-1.49, -1.17) * mm, "end": v(-1.56, -0.96) * mm});
            skLineSegment(sketch, "E1280", {"start": v(-1.56, -0.96) * mm, "end": v(-1.56, -0.45) * mm});
            skLineSegment(sketch, "E1281", {"start": v(-1.56, -0.45) * mm, "end": v(-1.51, 0.07) * mm});
            skLineSegment(sketch, "E1282", {"start": v(-1.51, 0.07) * mm, "end": v(-1.68, -0.1) * mm});
            skLineSegment(sketch, "E1283", {"start": v(-1.68, -0.1) * mm, "end": v(-2, -0.29) * mm});
            skLineSegment(sketch, "E1284", {"start": v(-2, -0.29) * mm, "end": v(-2.44, -0.36) * mm});
            skLineSegment(sketch, "E1285", {"start": v(-2.44, -0.36) * mm, "end": v(-2.26, -0.15) * mm});
            skLineSegment(sketch, "E1286", {"start": v(-2.26, -0.15) * mm, "end": v(-2.09, 0.07) * mm});
            skLineSegment(sketch, "E1287", {"start": v(-2.09, 0.07) * mm, "end": v(-1.84, 0.32) * mm});
            skLineSegment(sketch, "E1288", {"start": v(-1.84, 0.32) * mm, "end": v(-2.15, 0.22) * mm});
            skLineSegment(sketch, "E1289", {"start": v(-2.15, 0.22) * mm, "end": v(-2.5, 0.12) * mm});
            skLineSegment(sketch, "E1290", {"start": v(-2.5, 0.12) * mm, "end": v(-2.81, 0.13) * mm});
            skLineSegment(sketch, "E1291", {"start": v(-2.81, 0.13) * mm, "end": v(-3.03, 0.21) * mm});
            skLineSegment(sketch, "E1292", {"start": v(-3.03, 0.21) * mm, "end": v(-3.23, 0.38) * mm});
            skLineSegment(sketch, "E1293", {"start": v(-3.23, 0.38) * mm, "end": v(-3.16, 0.52) * mm});
            skLineSegment(sketch, "E1294", {"start": v(-3.16, 0.52) * mm, "end": v(-3.02, 0.83) * mm});
            skLineSegment(sketch, "E1295", {"start": v(-3.02, 0.83) * mm, "end": v(-2.95, 1.05) * mm});
            skLineSegment(sketch, "E1296", {"start": v(-2.95, 1.05) * mm, "end": v(-3.32, 1.08) * mm});
            skLineSegment(sketch, "E1297", {"start": v(-3.32, 1.08) * mm, "end": v(-3.65, 1.15) * mm});
            skLineSegment(sketch, "E1298", {"start": v(-3.65, 1.15) * mm, "end": v(-3.97, 1.25) * mm});
            skLineSegment(sketch, "E1299", {"start": v(-3.97, 1.25) * mm, "end": v(-3.57, 1.4) * mm});
            skLineSegment(sketch, "E1300", {"start": v(-3.57, 1.4) * mm, "end": v(-3.38, 1.53) * mm});
            skLineSegment(sketch, "E1301", {"start": v(-3.38, 1.53) * mm, "end": v(-3.18, 1.83) * mm});
            skLineSegment(sketch, "E1302", {"start": v(-3.18, 1.83) * mm, "end": v(-2.96, 2.23) * mm});
            skLineSegment(sketch, "E1303", {"start": v(-2.96, 2.23) * mm, "end": v(-3.14, 2.1) * mm});
            skLineSegment(sketch, "E1304", {"start": v(-3.14, 2.1) * mm, "end": v(-3.42, 1.99) * mm});
            skLineSegment(sketch, "E1305", {"start": v(-3.42, 1.99) * mm, "end": v(-3.77, 1.99) * mm});
            skLineSegment(sketch, "E1306", {"start": v(-3.77, 1.99) * mm, "end": v(-3.54, 1.84) * mm});
            skLineSegment(sketch, "E1307", {"start": v(-3.54, 1.84) * mm, "end": v(-3.76, 1.74) * mm});
            skLineSegment(sketch, "E1308", {"start": v(-3.76, 1.74) * mm, "end": v(-4.07, 1.69) * mm});
            skLineSegment(sketch, "E1309", {"start": v(-4.07, 1.69) * mm, "end": v(-4.38, 1.72) * mm});
            skLineSegment(sketch, "E1310", {"start": v(-4.38, 1.72) * mm, "end": v(-4.68, 1.89) * mm});
            skLineSegment(sketch, "E1311", {"start": v(-4.68, 1.89) * mm, "end": v(-4.55, 1.65) * mm});
            skLineSegment(sketch, "E1312", {"start": v(-4.55, 1.65) * mm, "end": v(-4.67, 1.64) * mm});
            skLineSegment(sketch, "E1313", {"start": v(-4.67, 1.64) * mm, "end": v(-4.9, 1.71) * mm});
            skLineSegment(sketch, "E1314", {"start": v(-4.9, 1.71) * mm, "end": v(-5.14, 1.87) * mm});
            skLineSegment(sketch, "E1315", {"start": v(-5.14, 1.87) * mm, "end": v(-5.4, 2.16) * mm});
            skLineSegment(sketch, "E1316", {"start": v(-5.4, 2.16) * mm, "end": v(-5.63, 2.55) * mm});
            skLineSegment(sketch, "E1317", {"start": v(-5.63, 2.55) * mm, "end": v(-5.66, 2.86) * mm});
            skLineSegment(sketch, "E1318", {"start": v(-5.66, 2.86) * mm, "end": v(-5.64, 3.14) * mm});
            skLineSegment(sketch, "E1319", {"start": v(-5.64, 3.14) * mm, "end": v(-5.57, 3.31) * mm});
            skLineSegment(sketch, "E1320", {"start": v(-5.57, 3.31) * mm, "end": v(-5.47, 3.05) * mm});
            skLineSegment(sketch, "E1321", {"start": v(-5.47, 3.05) * mm, "end": v(-5.4, 2.87) * mm});
            skLineSegment(sketch, "E1322", {"start": v(-5.4, 2.87) * mm, "end": v(-5.28, 2.71) * mm});
            skLineSegment(sketch, "E1323", {"start": v(-5.28, 2.71) * mm, "end": v(-5.14, 2.58) * mm});
            skLineSegment(sketch, "E1324", {"start": v(-5.14, 2.58) * mm, "end": v(-4.9, 2.45) * mm});
            skLineSegment(sketch, "E1325", {"start": v(-4.9, 2.45) * mm, "end": v(-4.62, 2.4) * mm});
            skLineSegment(sketch, "E1326", {"start": v(-4.62, 2.4) * mm, "end": v(-4.25, 2.36) * mm});
            skLineSegment(sketch, "E1327", {"start": v(-4.25, 2.36) * mm, "end": v(-4, 2.43) * mm});
            skLineSegment(sketch, "E1328", {"start": v(-4, 2.43) * mm, "end": v(-3.67, 2.59) * mm});
            skLineSegment(sketch, "E1329", {"start": v(-3.67, 2.59) * mm, "end": v(-3.43, 2.78) * mm});
            skLineSegment(sketch, "E1330", {"start": v(-3.43, 2.78) * mm, "end": v(-3.18, 3.04) * mm});
            skLineSegment(sketch, "E1331", {"start": v(-3.18, 3.04) * mm, "end": v(-2.93, 3.33) * mm});
            skLineSegment(sketch, "E1332", {"start": v(-2.93, 3.33) * mm, "end": v(-2.76, 3.56) * mm});
            skLineSegment(sketch, "E1333", {"start": v(-2.76, 3.56) * mm, "end": v(-2.82, 3.57) * mm});
            skLineSegment(sketch, "E1334", {"start": v(-2.82, 3.57) * mm, "end": v(-3, 3.48) * mm});
            skLineSegment(sketch, "E1335", {"start": v(-3, 3.48) * mm, "end": v(-3.3, 3.4) * mm});
            skLineSegment(sketch, "E1336", {"start": v(-3.3, 3.4) * mm, "end": v(-3.67, 3.4) * mm});
            skLineSegment(sketch, "E1337", {"start": v(-3.67, 3.4) * mm, "end": v(-3.85, 3.46) * mm});
            skLineSegment(sketch, "E1338", {"start": v(-3.85, 3.46) * mm, "end": v(-3.98, 3.55) * mm});
            skLineSegment(sketch, "E1339", {"start": v(-3.98, 3.55) * mm, "end": v(-4.08, 3.69) * mm});
            skLineSegment(sketch, "E1340", {"start": v(-4.08, 3.69) * mm, "end": v(-3.73, 3.7) * mm});
            skLineSegment(sketch, "E1341", {"start": v(-3.73, 3.7) * mm, "end": v(-3.35, 3.77) * mm});
            skLineSegment(sketch, "E1342", {"start": v(-3.35, 3.77) * mm, "end": v(-2.89, 3.93) * mm});
            skLineSegment(sketch, "E1343", {"start": v(-2.89, 3.93) * mm, "end": v(-2.5, 4.16) * mm});
            skLineSegment(sketch, "E1344", {"start": v(-2.5, 4.16) * mm, "end": v(-2.16, 4.46) * mm});
            skLineSegment(sketch, "E1345", {"start": v(-2.16, 4.46) * mm, "end": v(-1.74, 4.9) * mm});
            skLineSegment(sketch, "E1346", {"start": v(-1.74, 4.9) * mm, "end": v(-1.28, 5.32) * mm});
            skLineSegment(sketch, "E1347", {"start": v(-1.28, 5.32) * mm, "end": v(-0.9, 5.57) * mm});
            skLineSegment(sketch, "E1348", {"start": v(-0.9, 5.57) * mm, "end": v(-0.41, 5.7) * mm});
            skLineSegment(sketch, "E1349", {"start": v(-0.41, 5.7) * mm, "end": v(0.02, 5.72) * mm});
            skLineSegment(sketch, "E1350", {"start": v(0.02, 5.72) * mm, "end": v(0.53, 5.65) * mm});
            skLineSegment(sketch, "E1351", {"start": v(0.53, 5.65) * mm, "end": v(0.94, 5.7) * mm});
            skLineSegment(sketch, "E1352", {"start": v(0.94, 5.7) * mm, "end": v(1.35, 5.8) * mm});
            skLineSegment(sketch, "E1353", {"start": v(1.35, 5.8) * mm, "end": v(1.88, 6) * mm});
            skLineSegment(sketch, "E1354", {"start": v(1.88, 6) * mm, "end": v(2.29, 6.07) * mm});
            skLineSegment(sketch, "E1355", {"start": v(2.29, 6.07) * mm, "end": v(2.67, 6.16) * mm});
            skLineSegment(sketch, "E1356", {"start": v(2.67, 6.16) * mm, "end": v(2.88, 6.2) * mm});
            skLineSegment(sketch, "E1357", {"start": v(2.88, 6.2) * mm, "end": v(3.09, 6.19) * mm});
            skLineSegment(sketch, "E1358", {"start": v(3.09, 6.19) * mm, "end": v(3.25, 6.11) * mm});
            skLineSegment(sketch, "E1359", {"start": v(3.25, 6.11) * mm, "end": v(3.4, 5.99) * mm});
            skLineSegment(sketch, "E1360", {"start": v(3.4, 5.99) * mm, "end": v(3.51, 5.8) * mm});
            skLineSegment(sketch, "E1361", {"start": v(3.51, 5.8) * mm, "end": v(3.6, 5.6) * mm});
            skLineSegment(sketch, "E1362", {"start": v(3.6, 5.6) * mm, "end": v(3.7, 5.24) * mm});
            skLineSegment(sketch, "E1363", {"start": v(3.7, 5.24) * mm, "end": v(3.71, 4.93) * mm});
            skLineSegment(sketch, "E1364", {"start": v(3.71, 4.93) * mm, "end": v(3.69, 4.59) * mm});
            skLineSegment(sketch, "E1365", {"start": v(3.69, 4.59) * mm, "end": v(3.53, 4.74) * mm});
            skLineSegment(sketch, "E1366", {"start": v(3.53, 4.74) * mm, "end": v(3.38, 4.9) * mm});
            skLineSegment(sketch, "E1367", {"start": v(3.38, 4.9) * mm, "end": v(3.19, 5) * mm});
            skLineSegment(sketch, "E1368", {"start": v(3.19, 5) * mm, "end": v(3.06, 5.04) * mm});
            skLineSegment(sketch, "E1369", {"start": v(3.06, 5.04) * mm, "end": v(2.76, 5.05) * mm});
            skLineSegment(sketch, "E1370", {"start": v(2.76, 5.05) * mm, "end": v(2.57, 4.97) * mm});
            skLineSegment(sketch, "E1371", {"start": v(2.57, 4.97) * mm, "end": v(2.41, 4.87) * mm});
            skLineSegment(sketch, "E1372", {"start": v(2.41, 4.87) * mm, "end": v(2.29, 4.73) * mm});
            skLineSegment(sketch, "E1373", {"start": v(2.29, 4.73) * mm, "end": v(2.13, 4.51) * mm});
            skLineSegment(sketch, "E1374", {"start": v(2.13, 4.51) * mm, "end": v(2, 4.35) * mm});
            skLineSegment(sketch, "E1375", {"start": v(2, 4.35) * mm, "end": v(1.91, 4.26) * mm});
            skLineSegment(sketch, "E1376", {"start": v(1.91, 4.26) * mm, "end": v(1.81, 4.23) * mm});
            skLineSegment(sketch, "E1377", {"start": v(1.81, 4.23) * mm, "end": v(1.7, 4.22) * mm});
            skLineSegment(sketch, "E1378", {"start": v(1.7, 4.22) * mm, "end": v(1.57, 4.15) * mm});
            skLineSegment(sketch, "E1379", {"start": v(1.57, 4.15) * mm, "end": v(1.48, 4.04) * mm});
            skLineSegment(sketch, "E1380", {"start": v(1.48, 4.04) * mm, "end": v(1.37, 3.85) * mm});
            skLineSegment(sketch, "E1381", {"start": v(1.37, 3.85) * mm, "end": v(1.13, 3.25) * mm});
            skLineSegment(sketch, "E1382", {"start": v(1.13, 3.25) * mm, "end": v(1, 2.84) * mm});
            skLineSegment(sketch, "E1383", {"start": v(1, 2.84) * mm, "end": v(3.3, 3.24) * mm});
            skLineSegment(sketch, "E1384", {"start": v(3.3, 3.24) * mm, "end": v(3.34, 3.23) * mm});
            skLineSegment(sketch, "E1385", {"start": v(3.34, 3.23) * mm, "end": v(3.18, 3.1) * mm});
            skLineSegment(sketch, "E1386", {"start": v(3.18, 3.1) * mm, "end": v(3.05, 3.01) * mm});
            skLineSegment(sketch, "E1387", {"start": v(3.05, 3.01) * mm, "end": v(2.78, 2.85) * mm});
            skLineSegment(sketch, "E1388", {"start": v(2.78, 2.85) * mm, "end": v(2.45, 2.66) * mm});
            skLineSegment(sketch, "E1389", {"start": v(2.45, 2.66) * mm, "end": v(2.23, 2.52) * mm});
            skLineSegment(sketch, "E1390", {"start": v(2.23, 2.52) * mm, "end": v(1.8, 2.16) * mm});
            skLineSegment(sketch, "E1391", {"start": v(1.8, 2.16) * mm, "end": v(1.55, 1.91) * mm});
            skLineSegment(sketch, "E1392", {"start": v(1.55, 1.91) * mm, "end": v(1.4, 1.67) * mm});
            skLineSegment(sketch, "E1393", {"start": v(1.4, 1.67) * mm, "end": v(1.3, 1.43) * mm});
            skLineSegment(sketch, "E1394", {"start": v(1.3, 1.43) * mm, "end": v(1.32, 1.18) * mm});
            skLineSegment(sketch, "E1395", {"start": v(1.32, 1.18) * mm, "end": v(1.45, 0.88) * mm});
            skLineSegment(sketch, "E1396", {"start": v(1.45, 0.88) * mm, "end": v(1.62, 0.64) * mm});
            skLineSegment(sketch, "E1397", {"start": v(1.62, 0.64) * mm, "end": v(1.33, 0.42) * mm});
            skLineSegment(sketch, "E1398", {"start": v(1.33, 0.42) * mm, "end": v(1, 0.3) * mm});
            skLineSegment(sketch, "E1399", {"start": v(1, 0.3) * mm, "end": v(0.62, 0.24) * mm});
            skLineSegment(sketch, "E1400", {"start": v(0.62, 0.24) * mm, "end": v(1.12, -0.1) * mm});
            skLineSegment(sketch, "E1401", {"start": v(1.12, -0.1) * mm, "end": v(0.81, -0.13) * mm});
            skLineSegment(sketch, "E1402", {"start": v(0.81, -0.13) * mm, "end": v(0.44, -0.1) * mm});
            skLineSegment(sketch, "E1403", {"start": v(0.44, -0.1) * mm, "end": v(0.28, -0.06) * mm});
            skLineSegment(sketch, "E1404", {"start": v(0.28, -0.06) * mm, "end": v(0.1, 0.04) * mm});
            skLineSegment(sketch, "E1405", {"start": v(0.1, 0.04) * mm, "end": v(0.09, -0.08) * mm});
            skLineSegment(sketch, "E1406", {"start": v(0.09, -0.08) * mm, "end": v(0.16, -0.72) * mm});
            skLineSegment(sketch, "E1407", {"start": v(0.16, -0.72) * mm, "end": v(0.15, -0.92) * mm});
            skLineSegment(sketch, "E1408", {"start": v(0.15, -0.92) * mm, "end": v(-0.05, -0.66) * mm});
            skLineSegment(sketch, "E1409", {"start": v(-0.05, -0.66) * mm, "end": v(-0.36, -0.24) * mm});
            skLineSegment(sketch, "E1410", {"start": v(-0.36, -0.24) * mm, "end": v(-0.37, -0.41) * mm});
            skLineSegment(sketch, "E1411", {"start": v(-0.37, -0.41) * mm, "end": v(-0.33, -0.7) * mm});
            skLineSegment(sketch, "E1412", {"start": v(-0.33, -0.7) * mm, "end": v(-0.29, -1.4) * mm});
            skLineSegment(sketch, "E1413", {"start": v(-0.29, -1.4) * mm, "end": v(-0.22, -1.94) * mm});
            skLineSegment(sketch, "E1414", {"start": v(-0.22, -1.94) * mm, "end": v(-0.18, -2.74) * mm});
            skLineSegment(sketch, "E1415", {"start": v(-0.18, -2.74) * mm, "end": v(-0.2, -3.24) * mm});
            skLineSegment(sketch, "E1416", {"start": v(-0.2, -3.24) * mm, "end": v(-0.3, -3.72) * mm});
            skSolve(sketch);
        }
        {
            var Q0;
            Q0 = qSketchRegion(id + "F2", true);
            extrude(context, id + "F3", {"entities" : qUnion([Q0]), "operationType" : NewBodyOperationType.REMOVE, "depth" : 6 * mm, "offsetDistance" : 25 * mm});
        }
        {
            var Q0;
            Q0=qCreatedBy(makeId("Front.planeOp"),FACE);
            var sketch = newSketch(context, id + "F4", { "sketchPlane" : qUnion([Q0])});
            skText(sketch, "E1417", { "text": "PHOENIX", "fontName": "OpenSans-Regular.ttf"});
            const initialGuessF4  = {"E1417": [-0.02671, -0.00584, 1, 0, 0.00872]};
            skSetInitialGuess(sketch, initialGuessF4);
            skSolve(sketch);
        }
        {
            var Q0;
            Q0 = qSketchRegion(id + "F4", true);
            extrude(context, id + "F5", {"entities" : qUnion([Q0]), "operationType" : NewBodyOperationType.ADD, "depth" : 7 * mm, "offsetDistance" : 25 * mm, "hasSecondDirection" : true, "secondDirectionOppositeDirection" : false, "secondDirectionDepth" : 4 * mm});
        }
        {
            var Q0;
            Q0=qCreatedBy(makeId("Front.planeOp"),FACE);
            var sketch = newSketch(context, id + "F6", { "sketchPlane" : qUnion([Q0])});
            skCircle(sketch, "E1418", {"center": v(-0.4, 24.68) * mm, "radius": 2.5 * mm});
            skSolve(sketch);
        }
        {
            var Q0;
            Q0 = qSketchRegion(id + "F6", true);
            extrude(context, id + "F7", {"entities" : qUnion([Q0]), "operationType" : NewBodyOperationType.REMOVE, "depth" : 25 * mm, "offsetDistance" : 25 * mm});
        }
        {
            var Q0;
            Q0=makeQuery(id+"F1.opExtrude","CAP_EDGE",EDGE,{"disambiguationData":[OSD([sQuery(id+"F0.wireOp",EDGE,"E2")])],"isStart":true});
            var Q1;
            Q1=makeQuery(id+"F1.opExtrude","CAP_EDGE",EDGE,{"disambiguationData":[OSD([sQuery(id+"F0.wireOp",EDGE,"E2")])],"isStart":false});
            var Q2;
            {var subQ423=sQuery(id+"F0.wireOp",EDGE,"E2");var subQ424=makeQuery(id+"F1.opExtrude","SWEPT_FACE",FACE,{"disambiguationData":[OSD([subQ423])]});Q2=makeQuery(id+"F7.boolean.opBoolean","INTERSECT",EDGE,{"derivedFrom":[makeQuery(id+"F5.boolean.opBoolean","SPLIT",FACE,{"disambiguationData":[TD([subQ424])],"derivedFrom":makeQuery(id+"F3.boolean.opBoolean","SPLIT",FACE,{"disambiguationData":[TD([subQ424])],"derivedFrom":makeQuery(id+"F1.opExtrude","CAP_FACE",FACE,{"disambiguationData":[OSD([subQ423])],"isStart":false})})}),makeQuery(id+"F7.opExtrude","SWEPT_FACE",FACE,{"disambiguationData":[OSD([sQuery(id+"F6.wireOp",EDGE,"E1418")])]})]});}
            var Q3;
            Q3=makeQuery(id+"F7.boolean.opBoolean","COPY",EDGE,{"derivedFrom":makeQuery(id+"F7.opExtrude","CAP_EDGE",EDGE,{"disambiguationData":[OSD([sQuery(id+"F6.wireOp",EDGE,"E1418")])],"isStart":true})});
            chamfer(context, id + "F8", {"entities" : qUnion([Q0, Q1, Q2, Q3]), "width" : 1 * mm, "tangentPropagation" : true});
        }
    });
